FCSTD DOCUMENT  (FreeCAD 1.0R39109 (Git))
Label: handle-5mk3
License: All rights reserved
LicenseURL: https://en.wikipedia.org/wiki/All_rights_reserved
objects: Sketcher::SketchObject×44, PartDesign::Plane×17, PartDesign::Fillet×7, PartDesign::AdditivePipe×4, PartDesign::Pad×2, PartDesign::Body×2, Part::Feature×2, Mesh::Feature×1, PartDesign::SubtractiveLoft×1, PartDesign::Hole×1, Part::Refine×1, PartDesign::Pocket×1
note: 158 computed .brp shape members not serialized (recipe doc carries the construction recipe); baked Part::Feature solids carry a one-line shape summary decoded from their .brp

FEATURE [Sketcher::SketchObject] Sketch  label="draft"
  ArcFitTolerance = 1e-06
  FullyConstrained = false
  MakeInternals = false
  sketch-geometry (31):
    g0: LineSegment StartX=0 StartY=16.8405 StartZ=0 EndX=0 EndY=0 EndZ=0
    g1: ArcOfCircle CenterX=24.2442 CenterY=17 CenterZ=0 NormalX=0 NormalY=0 NormalZ=1 AngleXU=0 Radius=17 StartAngle=4.71239 EndAngle=6.01234
    g2: ArcOfCircle CenterX=12.089 CenterY=21.8405 CenterZ=0 NormalX=0 NormalY=0 NormalZ=1 AngleXU=0 Radius=5 StartAngle=4.71239 EndAngle=6.02249
    g3: ArcOfCircle CenterX=0 CenterY=8.42024 CenterZ=0 NormalX=0 NormalY=0 NormalZ=1 AngleXU=0 Radius=8.42024 StartAngle=1.5708 EndAngle=4.71239
    g4: LineSegment StartX=12.089 StartY=16.8405 StartZ=0 EndX=12.089 EndY=0 EndZ=0
    g5: LineSegment StartX=15.135 StartY=17.8754 StartZ=0 EndX=34.532 EndY=3.46632 EndZ=0
    g6: LineSegment StartX=12.089 StartY=16.8405 StartZ=0 EndX=24.2442 EndY=-0.00123973 EndZ=0
    g7: LineSegment StartX=16.92 StartY=20.5517 StartZ=0 EndX=40.6245 EndY=12.4517 EndZ=0
    g8: LineSegment StartX=12.089 StartY=16.8405 StartZ=0 EndX=17.9725 EndY=-3.6e-15 EndZ=0
    g9: LineSegment StartX=8.25203 StartY=67.8671 StartZ=0 EndX=4.47332 EndY=84.6059 EndZ=0
    g10: ArcOfCircle CenterX=6.36268 CenterY=76.2365 CenterZ=0 NormalX=0 NormalY=0 NormalZ=1 AngleXU=0 Radius=8.58001 StartAngle=1.79282 EndAngle=4.93441
    g11: LineSegment StartX=4.3823 StartY=126.388 StartZ=0 EndX=26.3634 EndY=138.297 EndZ=0
    g12: LineSegment StartX=0 StartY=0 StartZ=0 EndX=24.2442 EndY=0 EndZ=0
    g13: LineSegment StartX=12.089 StartY=16.8405 StartZ=0 EndX=0 EndY=16.8405 EndZ=0
    g14: ArcOfCircle CenterX=-122.373 CenterY=57.711 CenterZ=0 NormalX=0 NormalY=0 NormalZ=1 AngleXU=0 Radius=169.165 StartAngle=6.01234 EndAngle=6.77971
    g15: LineSegment StartX=34.0166 StartY=141.401 StartZ=0 EndX=34.0166 EndY=126.047 EndZ=0
    g16: LineSegment StartX=34.0166 StartY=141.401 StartZ=0 EndX=31.941 EndY=152.351 EndZ=0
    g17: LineSegment StartX=22.7796 StartY=155.606 StartZ=0 EndX=28.011 EndY=155.606 EndZ=0
    g18: LineSegment StartX=18.3769 StartY=88.901 StartZ=0 EndX=4.47332 EndY=84.6059 EndZ=0
    g19: LineSegment StartX=21.1969 StartY=70.7893 StartZ=0 EndX=8.25203 EndY=67.8671 EndZ=0
    g20: LineSegment StartX=18.7796 StartY=146.991 StartZ=0 EndX=18.7796 EndY=151.606 EndZ=0
    g21: LineSegment StartX=15.6305 StartY=135.869 StartZ=0 EndX=18.5135 EndY=145.224 EndZ=0
    g22: ArcOfCircle CenterX=12.7796 CenterY=146.991 CenterZ=0 NormalX=0 NormalY=0 NormalZ=1 AngleXU=0 Radius=6 StartAngle=5.98426 EndAngle=6.28319
    g23: ArcOfCircle CenterX=5.11835 CenterY=139.108 CenterZ=0 NormalX=0 NormalY=0 NormalZ=1 AngleXU=0 Radius=11 StartAngle=5.12409 EndAngle=5.98426
    g24: ArcOfCircle CenterX=27.9086 CenterY=86.9159 CenterZ=0 NormalX=0 NormalY=0 NormalZ=1 AngleXU=0 Radius=45.9511 StartAngle=1.9825 EndAngle=2.10829
    g25: ArcOfCircle CenterX=22.7796 CenterY=151.606 CenterZ=0 NormalX=0 NormalY=0 NormalZ=1 AngleXU=0 Radius=4 StartAngle=1.5708 EndAngle=3.14159
    g26: ArcOfCircle CenterX=28.011 CenterY=151.606 CenterZ=0 NormalX=0 NormalY=0 NormalZ=1 AngleXU=0 Radius=4 StartAngle=0.187333 EndAngle=1.5708
    g27: ArcOfCircle CenterX=54.0166 CenterY=126.047 CenterZ=0 NormalX=0 NormalY=0 NormalZ=1 AngleXU=0 Radius=20 StartAngle=3.14159 EndAngle=3.5112
    g28: ArcOfCircle CenterX=-122.373 CenterY=57.711 CenterZ=0 NormalX=0 NormalY=0 NormalZ=1 AngleXU=0 Radius=144.165 StartAngle=6.02249 EndAngle=6.37403
    g29: ArcOfCircle CenterX=-122.373 CenterY=57.711 CenterZ=0 NormalX=0 NormalY=0 NormalZ=1 AngleXU=0 Radius=144.165 StartAngle=0.218074 EndAngle=0.496528
    g30: ArcOfCircle CenterX=-122.373 CenterY=57.711 CenterZ=0 NormalX=0 NormalY=0 NormalZ=1 AngleXU=0 Radius=156.665 StartAngle=6.01234 EndAngle=6.77971
  constraints (1):
    c: Distance(g6,g6) = 20.77
FEATURE [Sketcher::SketchObject] Sketch001  label="main"
  ArcFitTolerance = 1e-06
  AttachmentSupport = -> [XY_Plane]
  FullyConstrained = false
  MakeInternals = false
  MapMode = 5
  sketch-geometry (33):
    g0: LineSegment StartX=0 StartY=0 StartZ=0 EndX=3e-16 EndY=17 EndZ=0
    g1: LineSegment StartX=3e-16 StartY=17 StartZ=0 EndX=11.9553 EndY=17 EndZ=0
    g2: ArcOfCircle CenterX=0.098169 CenterY=8.5 CenterZ=0 NormalX=0 NormalY=0 NormalZ=1 AngleXU=0 Radius=8.50057 StartAngle=1.58235 EndAngle=4.70084
    g3: LineSegment StartX=4.3731 StartY=126.451 StartZ=0 EndX=26.3546 EndY=138.359 EndZ=0
    g4: ArcOfCircle CenterX=-121.158 CenterY=57.9598 CenterZ=0 NormalX=0 NormalY=0 NormalZ=1 AngleXU=0 Radius=168 StartAngle=6.01838 EndAngle=6.78221
    g5: ArcOfCircle CenterX=-121.158 CenterY=57.9598 CenterZ=0 NormalX=0 NormalY=0 NormalZ=1 AngleXU=0 Radius=143 StartAngle=6.01836 EndAngle=6.78265
    g6: ArcOfCircle CenterX=11.9915 CenterY=22.1177 CenterZ=0 NormalX=0 NormalY=0 NormalZ=1 AngleXU=0 Radius=5.11783 StartAngle=4.70532 EndAngle=5.96793
    g7: LineSegment StartX=40.9861 StartY=13.99 StartZ=0 EndX=16.8571 EndY=20.5309 EndZ=0
    g8: ArcOfCircle CenterX=23.8596 CenterY=17.4727 CenterZ=0 NormalX=0 NormalY=0 NormalZ=1 AngleXU=0 Radius=17.4771 StartAngle=4.73473 EndAngle=6.08257
    g9: LineSegment StartX=33.9499 StartY=141.42 StartZ=0 EndX=32 EndY=152 EndZ=0
    g10: LineSegment StartX=19 StartY=152 StartZ=0 EndX=18.6911 EndY=146 EndZ=0
    g11: LineSegment StartX=22 StartY=155.6 StartZ=0 EndX=29 EndY=155.6 EndZ=0
    g12: ArcOfCircle CenterX=28.2135 CenterY=151.895 CenterZ=0 NormalX=0 NormalY=0 NormalZ=1 AngleXU=0 Radius=3.78792 StartAngle=0.027823 EndAngle=1.36165
    g13: ArcOfCircle CenterX=22.5443 CenterY=152.096 CenterZ=0 NormalX=0 NormalY=0 NormalZ=1 AngleXU=0 Radius=3.5456 StartAngle=1.72492 EndAngle=3.16879
    g14: LineSegment StartX=4.41682 StartY=84.6096 StartZ=0 EndX=8.23235 EndY=68.0434 EndZ=0
    g15: ArcOfCircle CenterX=6.32458 CenterY=76.3265 CenterZ=0 NormalX=0 NormalY=0 NormalZ=1 AngleXU=0 Radius=8.5 StartAngle=1.79717 EndAngle=4.93946
    g16: LineSegment StartX=4.42825 StartY=84.5878 StartZ=0 EndX=18.4319 EndY=88.947 EndZ=0
    g17: LineSegment StartX=8.23235 StartY=68.0434 StartZ=0 EndX=21.1452 EndY=72.063 EndZ=0
    g18: LineSegment StartX=32.5262 StartY=20 StartZ=0 EndX=28.9216 EndY=17.2604 EndZ=0
    g19: LineSegment StartX=11.9553 StartY=17 StartZ=0 EndX=24.25 EndY=5.33e-14 EndZ=0
    g20: LineSegment StartX=14.9929 StartY=17.9724 StartZ=0 EndX=35.0562 EndY=4.05322 EndZ=0
    g21: LineSegment StartX=16.2172 StartY=19.2306 StartZ=0 EndX=39.0494 EndY=8.82884 EndZ=0
    g22: LineSegment StartX=13.6942 StartY=17.2914 StartZ=0 EndX=30.2927 EndY=1.22269 EndZ=0
    g23: LineSegment StartX=10.6374 StartY=17 StartZ=0 EndX=17.3604 EndY=0 EndZ=0
    g24: LineSegment StartX=9.44468 StartY=17 StartZ=0 EndX=12.125 EndY=0 EndZ=0
    g25: LineSegment StartX=8.01497 StartY=17 StartZ=0 EndX=8.01497 EndY=0 EndZ=0
    g26: LineSegment StartX=5.97763 StartY=17 StartZ=0 EndX=5.97763 EndY=0 EndZ=0
    g27: LineSegment StartX=20.8595 StartY=74.6968 StartZ=0 EndX=45.6917 EndY=77.5875 EndZ=0
    g28: LineSegment StartX=0 StartY=0 StartZ=0 EndX=8.01497 EndY=0 EndZ=0
    g29: LineSegment StartX=8.01497 StartY=0 StartZ=0 EndX=24.25 EndY=0 EndZ=0
    g30: LineSegment StartX=15.3638 StartY=132.405 StartZ=0 EndX=18.6911 EndY=146 EndZ=0
    g31: LineSegment StartX=33.9499 StartY=141.42 StartZ=0 EndX=35.5663 EndY=109.757 EndZ=0
    g32: LineSegment StartX=15.3638 StartY=132.405 StartZ=0 EndX=35.5663 EndY=109.757 EndZ=0
  constraints (60):
    c: PointOnObject(g8,g-1)
    c: Distance(g0) = 17
    c: PointOnObject(g0,g-2)
    c: DistanceX(g-1,g8) = 24.25
    c: Coincident(g1,g0)
    c: Horizontal(g1)
    c: Coincident(g2,g0)
    c: Distance(g3) = 25
    c: Coincident(g4,g3)
    c: Radius(g4) = 168
    c: Coincident(g5,g4)
    c: Coincident(g5,g3)
    c: Coincident(g6,g1)
    c: Coincident(g6,g5)
    c: Coincident(g7,g4)
    c: Coincident(g7,g5)
    c: DistanceY(g-1,g4) = 13.99
    c: Coincident(g8,g4)
    c: Horizontal(g11)
    c: Coincident(g12,g11)
    c: Coincident(g12,g9)
    c: Coincident(g13,g11)
    c: Coincident(g13,g10)
    c: Distance(g14) = 17
    c: Symmetric(g14,g14,g15)
    c: Coincident(g15,g14)
    c: Coincident(g17,g14)
    c: PointOnObject(g17,g5)
    c: Parallel(g17,g16)
    c: Symmetric(g7,g7,g18)
    c: Coincident(g19,g1)
    c: PointOnObject(g20,g6)
    c: PointOnObject(g20,g8)
    c: PointOnObject(g21,g6)
    c: PointOnObject(g21,g8)
    c: PointOnObject(g22,g6)
    c: PointOnObject(g22,g8)
    c: PointOnObject(g23,g1)
    c: PointOnObject(g24,g1)
    c: Symmetric(g-1,g8,g24)
    c: PointOnObject(g25,g1)
    c: Vertical(g25)
    c: Symmetric(g1,g1,g26)
    c: Vertical(g26)
    c: PointOnObject(g27,g5)
    c: PointOnObject(g27,g4)
    c: Distance(g19,g19) = 20.98
    c: Distance(g21,g21) = 25.09
    c: Distance(g24,g24) = 17.21
    c: Coincident(g28,g0)
    c: Coincident(g28,g25)
    c: Horizontal(g28)
    c: Coincident(g29,g25)
    c: Coincident(g29,g8)
    c: Horizontal(g29)
    c: Symmetric(g3,g3,g30)
    c: Coincident(g30,g10)
    c: Coincident(g31,g9)
    c: Coincident(g32,g30)
    c: Coincident(g32,g31)
FEATURE [PartDesign::Plane] DatumPlane001
  AttachmentOffset = pos=(0,0,0) rot=(0,1,0;1.5708rad)
  AttachmentSupport = -> [Sketch001]
  Length = 78.1067
  MapMode = 7
  Placement = pos=(40.9861,13.99,0) rot=(0.093727,0.703994,0.703994;2.95468rad)
  ResizeMode = 0
  Width = 61.5385
FEATURE [PartDesign::Plane] DatumPlane002
  AttachmentOffset = pos=(0,0,0) rot=(0,1,0;1.5708rad)
  AttachmentSupport = -> [Sketch001]
  Length = 60
  MapMode = 7
  Placement = pos=(0,0,0) rot=(0.57735,0.57735,0.57735;2.0944rad)
  ResizeMode = 0
  Width = 60
FEATURE [PartDesign::Plane] DatumPlane
  AttachmentOffset = pos=(0,0,0) rot=(0,1,0;1.5708rad)
  AttachmentSupport = -> [Sketch001]
  Length = 111.967
  MapMode = 7
  Placement = pos=(4.3731,126.451,0) rot=(0.941347,0.238607,0.238607;1.6312rad)
  ResizeMode = 0
  Width = 63.9978
FEATURE [Sketcher::SketchObject] Sketch002
  ArcFitTolerance = 1e-06
  AttachmentSupport = -> [DatumPlane]
  FullyConstrained = false
  MakeInternals = false
  MapMode = 5
  Placement = pos=(4.3731,126.451,0) rot=(0.941347,0.238607,0.238607;1.6312rad)
  sketch-geometry (5):
    g0: Ellipse CenterX=12.5 CenterY=0 CenterZ=0 NormalX=0 NormalY=0 NormalZ=1 MajorRadius=18 MinorRadius=12.5 AngleXU=1.5708
    g1: LineSegment [constr] StartX=12.5 StartY=18 StartZ=0 EndX=12.5 EndY=-18 EndZ=0
    g2: LineSegment [constr] StartX=0 StartY=0 StartZ=0 EndX=25 EndY=0 EndZ=0
    g3: GeomPoint [constr] X=12.5 Y=12.9518 Z=0
    g4: GeomPoint [constr] X=12.5 Y=-12.9518 Z=0
  constraints (2):
    c: InternalAlignment(g1-g4 -> g0) x4
    c: PointOnObject(g-1,g0)
FEATURE [Sketcher::SketchObject] Sketch004  label="end"
  ArcFitTolerance = 1e-06
  AttachmentOffset = pos=(0,0,-5) rot=(0,0,1;0rad)
  AttachmentSupport = -> [DatumPlane002]
  FullyConstrained = false
  MakeInternals = false
  MapMode = 5
  Placement = pos=(-5,0,0) rot=(0.57735,0.57735,0.57735;2.0944rad)
  sketch-geometry (5):
    g0: Ellipse CenterX=8.5 CenterY=0 CenterZ=0 NormalX=0 NormalY=0 NormalZ=1 MajorRadius=18 MinorRadius=8.5 AngleXU=1.5708
    g1: LineSegment [constr] StartX=8.5 StartY=18 StartZ=0 EndX=8.5 EndY=-18 EndZ=0
    g2: LineSegment [constr] StartX=0 StartY=0 StartZ=0 EndX=17 EndY=0 EndZ=0
    g3: GeomPoint [constr] X=8.5 Y=15.8666 Z=0
    g4: GeomPoint [constr] X=8.5 Y=-15.8666 Z=0
  constraints (2):
    c: InternalAlignment(g1-g4 -> g0) x4
    c: PointOnObject(g-1,g0)
FEATURE [PartDesign::AdditivePipe] AdditivePipe
  AuxilleryCurvelinear = true
  AuxillerySpineTangent = false
  Binormal = (0,0,0)
  Mode = 0
  Placement = pos=(4.3731,126.451,0) rot=(0.941347,0.238607,0.238607;1.6312rad)
  Profile = -> Sketch002
  Refine = true
  Spine = -> Sketch001 [Edge8]
  SpineTangent = false
  Suppressed = false
  Transformation = 0
  Transition = 0
FEATURE [PartDesign::Plane] DatumPlane004
  AttachmentOffset = pos=(0,0,0) rot=(0,1,0;1.5708rad)
  AttachmentSupport = -> [Sketch001]
  Length = 81.3794
  MapMode = 7
  Placement = pos=(14.9929,17.9724,0) rot=(-0.91446,0.28615,0.28615;4.62309rad)
  ResizeMode = 0
  Width = 61.7968
FEATURE [Sketcher::SketchObject] Sketch006
  ArcFitTolerance = 1e-06
  AttachmentSupport = -> [DatumPlane004]
  FullyConstrained = false
  MakeInternals = false
  MapMode = 5
  Placement = pos=(14.9929,17.9724,0) rot=(0.91446,-0.28615,-0.28615;1.6601rad)
  sketch-geometry (5):
    g0: Ellipse CenterX=12.205 CenterY=0 CenterZ=0 NormalX=0 NormalY=0 NormalZ=1 MajorRadius=18 MinorRadius=12.205 AngleXU=1.5708
    g1: LineSegment [constr] StartX=12.205 StartY=18 StartZ=0 EndX=12.205 EndY=-18 EndZ=0
    g2: LineSegment [constr] StartX=0 StartY=0 StartZ=0 EndX=24.41 EndY=0 EndZ=0
    g3: GeomPoint [constr] X=12.205 Y=13.2302 Z=0
    g4: GeomPoint [constr] X=12.205 Y=-13.2302 Z=0
  constraints (2):
    c: InternalAlignment(g1-g4 -> g0) x4
    c: PointOnObject(g-1,g0)
FEATURE [PartDesign::Plane] DatumPlane005
  AttachmentOffset = pos=(0,0,0) rot=(0,1,0;1.5708rad)
  AttachmentSupport = -> [Sketch001]
  Length = 81.6324
  MapMode = 7
  Placement = pos=(11.9553,17,0) rot=(-0.810565,0.414116,0.414116;4.50389rad)
  ResizeMode = 0
  Width = 61.8166
FEATURE [Sketcher::SketchObject] Sketch007
  ArcFitTolerance = 1e-06
  AttachmentSupport = -> [DatumPlane005]
  FullyConstrained = false
  MakeInternals = false
  MapMode = 5
  Placement = pos=(11.9553,17,0) rot=(0.810565,-0.414116,-0.414116;1.77929rad)
  sketch-geometry (5):
    g0: Ellipse CenterX=10.49 CenterY=0 CenterZ=0 NormalX=0 NormalY=0 NormalZ=1 MajorRadius=18 MinorRadius=10.49 AngleXU=1.5708
    g1: LineSegment [constr] StartX=10.49 StartY=18 StartZ=0 EndX=10.49 EndY=-18 EndZ=0
    g2: LineSegment [constr] StartX=0 StartY=0 StartZ=0 EndX=20.98 EndY=0 EndZ=0
    g3: GeomPoint [constr] X=10.49 Y=14.6274 Z=0
    g4: GeomPoint [constr] X=10.49 Y=-14.6274 Z=0
  constraints (2):
    c: InternalAlignment(g1-g4 -> g0) x4
    c: PointOnObject(g-1,g0)
FEATURE [PartDesign::Plane] DatumPlane006
  AttachmentOffset = pos=(0,0,0) rot=(0,1,0;1.5708rad)
  AttachmentSupport = -> [Sketch001]
  Length = 77.7387
  MapMode = 7
  Placement = pos=(16.2172,19.2306,0) rot=(-0.955975,0.207499,0.207499;4.66738rad)
  ResizeMode = 0
  Width = 61.5091
FEATURE [Sketcher::SketchObject] Sketch008
  ArcFitTolerance = 1e-06
  AttachmentSupport = -> [DatumPlane006]
  FullyConstrained = false
  MakeInternals = false
  MapMode = 5
  Placement = pos=(16.2172,19.2306,0) rot=(0.955975,-0.207499,-0.207499;1.6158rad)
  sketch-geometry (5):
    g0: Ellipse CenterX=12.545 CenterY=0 CenterZ=0 NormalX=0 NormalY=0 NormalZ=1 MajorRadius=18 MinorRadius=12.545 AngleXU=1.5708
    g1: LineSegment [constr] StartX=12.545 StartY=18 StartZ=0 EndX=12.545 EndY=-18 EndZ=0
    g2: LineSegment [constr] StartX=0 StartY=0 StartZ=0 EndX=25.09 EndY=0 EndZ=0
    g3: GeomPoint [constr] X=12.545 Y=12.9083 Z=0
    g4: GeomPoint [constr] X=12.545 Y=-12.9083 Z=0
  constraints (2):
    c: InternalAlignment(g1-g4 -> g0) x4
    c: PointOnObject(g-1,g0)
FEATURE [PartDesign::Plane] DatumPlane007
  AttachmentOffset = pos=(0,0,0) rot=(0,1,0;1.5708rad)
  AttachmentSupport = -> [Sketch001]
  Length = 81.6324
  MapMode = 7
  Placement = pos=(11.9553,17,0) rot=(-0.810565,0.414116,0.414116;4.50389rad)
  ResizeMode = 0
  Width = 61.8166
FEATURE [Sketcher::SketchObject] Sketch009  label="start"
  ArcFitTolerance = 1e-06
  AttachmentSupport = -> [DatumPlane007]
  FullyConstrained = false
  MakeInternals = false
  MapMode = 5
  Placement = pos=(11.9553,17,0) rot=(0.810565,-0.414116,-0.414116;1.77929rad)
  sketch-geometry (5):
    g0: Ellipse CenterX=10.49 CenterY=0 CenterZ=0 NormalX=0 NormalY=0 NormalZ=1 MajorRadius=18 MinorRadius=10.49 AngleXU=1.5708
    g1: LineSegment [constr] StartX=10.49 StartY=18 StartZ=0 EndX=10.49 EndY=-18 EndZ=0
    g2: LineSegment [constr] StartX=0 StartY=0 StartZ=0 EndX=20.98 EndY=0 EndZ=0
    g3: GeomPoint [constr] X=10.49 Y=14.6274 Z=0
    g4: GeomPoint [constr] X=10.49 Y=-14.6274 Z=0
  constraints (2):
    c: InternalAlignment(g1-g4 -> g0) x4
    c: PointOnObject(g-1,g0)
FEATURE [PartDesign::Plane] DatumPlane008
  AttachmentOffset = pos=(0,0,0) rot=(0,1,0;1.5708rad)
  AttachmentSupport = -> [Sketch001]
  Length = 67.8706
  MapMode = 7
  Placement = pos=(9.44468,17,0) rot=(-0.63745,0.54482,0.54482;4.2766rad)
  ResizeMode = 0
  Width = 60.6936
FEATURE [Sketcher::SketchObject] Sketch010
  ArcFitTolerance = 1e-06
  AttachmentOffset = pos=(0,0,2) rot=(0,0,1;0rad)
  AttachmentSupport = -> [DatumPlane008]
  FullyConstrained = false
  MakeInternals = false
  MapMode = 5
  Placement = pos=(7.46909,16.6885,2e-16) rot=(0.63745,-0.54482,-0.54482;2.00659rad)
  sketch-geometry (5):
    g0: Ellipse CenterX=8.605 CenterY=0 CenterZ=0 NormalX=0 NormalY=0 NormalZ=1 MajorRadius=18 MinorRadius=8.605 AngleXU=1.5708
    g1: LineSegment [constr] StartX=8.605 StartY=18 StartZ=0 EndX=8.605 EndY=-18 EndZ=0
    g2: LineSegment [constr] StartX=0 StartY=0 StartZ=0 EndX=17.21 EndY=0 EndZ=0
    g3: GeomPoint [constr] X=8.605 Y=15.8099 Z=0
    g4: GeomPoint [constr] X=8.605 Y=-15.8099 Z=0
  constraints (2):
    c: InternalAlignment(g1-g4 -> g0) x4
    c: PointOnObject(g-1,g0)
FEATURE [PartDesign::Plane] DatumPlane009
  AttachmentOffset = pos=(0,0,0) rot=(0,1,0;1.5708rad)
  AttachmentSupport = -> [Sketch001]
  Length = 60
  MapMode = 7
  Placement = pos=(8.01497,17,0) rot=(-0.57735,0.57735,0.57735;4.18879rad)
  ResizeMode = 0
  Width = 60
FEATURE [Sketcher::SketchObject] Sketch011
  ArcFitTolerance = 1e-06
  AttachmentOffset = pos=(0,0,5) rot=(0,0,1;0rad)
  AttachmentSupport = -> [DatumPlane009]
  FullyConstrained = false
  MakeInternals = false
  MapMode = 5
  Placement = pos=(3.01497,17,0) rot=(0.57735,-0.57735,-0.57735;2.0944rad)
  sketch-geometry (5):
    g0: Ellipse CenterX=8.5 CenterY=0 CenterZ=0 NormalX=0 NormalY=0 NormalZ=1 MajorRadius=18 MinorRadius=8.5 AngleXU=1.5708
    g1: LineSegment [constr] StartX=8.5 StartY=18 StartZ=0 EndX=8.5 EndY=-18 EndZ=0
    g2: LineSegment [constr] StartX=0 StartY=0 StartZ=0 EndX=17 EndY=0 EndZ=0
    g3: GeomPoint [constr] X=8.5 Y=15.8666 Z=0
    g4: GeomPoint [constr] X=8.5 Y=-15.8666 Z=0
  constraints (2):
    c: InternalAlignment(g1-g4 -> g0) x4
    c: PointOnObject(g-1,g0)
FEATURE [Sketcher::SketchObject] Sketch012
  ArcFitTolerance = 1e-06
  AttachmentSupport = -> [XY_Plane]
  FullyConstrained = false
  MakeInternals = false
  MapMode = 5
  sketch-geometry (2):
    g0: ArcOfCircle CenterX=0 CenterY=8.5 CenterZ=0 NormalX=0 NormalY=0 NormalZ=1 AngleXU=0 Radius=8.5 StartAngle=1.5708 EndAngle=4.71239
    g1: LineSegment StartX=-1.6e-15 StartY=17 StartZ=0 EndX=-1.6e-15 EndY=0 EndZ=0
  constraints (4):
    c: Coincident(g0,g-1)
    c: Coincident(g1,g0)
    c: Coincident(g1,g0)
    c: Vertical(g1)
FEATURE [Sketcher::SketchObject] Sketch013  label="hole"
  ArcFitTolerance = 1e-06
  AttachmentOffset = pos=(0,0,19) rot=(0,0,1;0rad)
  AttachmentSupport = -> [XY_Plane]
  FullyConstrained = false
  MakeInternals = false
  MapMode = 5
  Placement = pos=(0,0,19) rot=(0,0,1;0rad)
  sketch-geometry (2):
    g0: Circle CenterX=29.902 CenterY=19.7627 CenterZ=0 NormalX=0 NormalY=0 NormalZ=1 AngleXU=0 Radius=0.75
    g1: Circle CenterX=24.3839 CenterY=114.1 CenterZ=0 NormalX=0 NormalY=0 NormalZ=1 AngleXU=0 Radius=0.75
  constraints (2):
    c: Diameter(g0) = 1.5
    c: Diameter(g1) = 1.5
FEATURE [Sketcher::SketchObject] Sketch014
  ArcFitTolerance = 1e-06
  AttachmentSupport = -> [XY_Plane]
  FullyConstrained = true
  MakeInternals = false
  MapMode = 5
FEATURE [Sketcher::SketchObject] Sketch015
  ArcFitTolerance = 1e-06
  AttachmentSupport = -> [XY_Plane]
  FullyConstrained = false
  MakeInternals = false
  MapMode = 5
  sketch-geometry (8):
    g0: LineSegment StartX=23.8504 StartY=155.6 StartZ=0 EndX=28.2953 EndY=155.6 EndZ=0
    g1: LineSegment StartX=18.9469 StartY=150.935 StartZ=0 EndX=18.7 EndY=145.978 EndZ=0
    g2: LineSegment StartX=18.7 StartY=145.978 StartZ=0 EndX=15.4 EndY=132.3 EndZ=0
    g3: LineSegment StartX=15.4 StartY=132.3 StartZ=0 EndX=34 EndY=110 EndZ=0
    g4: LineSegment StartX=34 StartY=141 StartZ=0 EndX=34 EndY=110 EndZ=0
    g5: LineSegment StartX=34 StartY=141 StartZ=0 EndX=31.8911 EndY=152.599 EndZ=0
    g6: ArcOfCircle CenterX=28.2953 CenterY=151.945 CenterZ=0 NormalX=0 NormalY=0 NormalZ=1 AngleXU=0 Radius=3.65468 StartAngle=0.179853 EndAngle=1.5708
    g7: ArcOfCircle CenterX=23.8504 CenterY=150.69 CenterZ=0 NormalX=0 NormalY=0 NormalZ=1 AngleXU=0 Radius=4.90952 StartAngle=1.5708 EndAngle=3.09181
  constraints (10):
    c: Horizontal(g0)
    c: Coincident(g2,g1)
    c: Coincident(g3,g2)
    c: Coincident(g4,g3)
    c: Vertical(g4)
    c: Coincident(g5,g4)
    c: Tangent(g0,g6) = 1.5708
    c: Tangent(g5,g6) = -1.5708
    c: Tangent(g0,g7) = 1.5708
    c: Tangent(g1,g7) = -1.5708
FEATURE [Sketcher::SketchObject] Sketch016
  ArcFitTolerance = 1e-06
  AttachmentSupport = -> [XY_Plane]
  FullyConstrained = false
  MakeInternals = false
  MapMode = 5
  sketch-geometry (25):
    g0-g6: Circle [constr] x7 (B-spline internal-alignment scaffolding for g7; pole/knot coordinates omitted)
    g7: BSplineCurve PolesCount=7 KnotsCount=5 Degree=3 IsPeriodic=0
    g8-g12: GeomPoint [constr] x5 (B-spline internal-alignment scaffolding for g7; pole/knot coordinates omitted)
    g13-g17: Circle [constr] x5 (B-spline internal-alignment scaffolding for g18; pole/knot coordinates omitted)
    g18: BSplineCurve PolesCount=5 KnotsCount=3 Degree=3 IsPeriodic=0
    g19: GeomPoint [constr] X=-13.6801 Y=65.1223 Z=0
    g20: GeomPoint [constr] X=2.04903 Y=69.1377 Z=0
    g21: GeomPoint [constr] X=32.8092 Y=77.3228 Z=0
    g22: LineSegment StartX=12.6036 StartY=113.182 StartZ=0 EndX=25 EndY=113.182 EndZ=0
    g23: LineSegment StartX=32.8092 StartY=77.3228 StartZ=0 EndX=25 EndY=113.182 EndZ=0
    g24: ArcOfCircle CenterX=27.8804 CenterY=86.9633 CenterZ=0 NormalX=0 NormalY=0 NormalZ=1 AngleXU=0 Radius=46.95 StartAngle=3.20085 EndAngle=3.62545
  constraints (20):
    c: Weight(g0) = 1
    c: Equal(g0, g1-g6) x6
    c: InternalAlignment(g0-g6 -> g7) x7
    c: InternalAlignment(g8-g12 -> g7) x5
    c: Weight(g13) = 1
    c: Equal(g13, g14-g17) x4
    c: InternalAlignment(g13-g17 -> g18) x5
    c: InternalAlignment(g19,g18)
    c: InternalAlignment(g20,g18)
    c: InternalAlignment(g21,g18)
    c: PointOnObject(g15,g-2)
    c: Coincident(g22,g7)
    c: Horizontal(g22)
    c: Coincident(g23,g18)
    c: Coincident(g23,g22)
    c: Coincident(g24,g7)
    c: Coincident(g24,g18)
    c: Radius(g24) = 46.95
    c: DistanceX(g18) = -13.6801
    c: DistanceY(g18) = 65.1223
FEATURE [Mesh::Feature] right_handle
  Placement = pos=(-103,67,0) rot=(0,0,1;0rad)
FEATURE [Sketcher::SketchObject] Sketch017
  ArcFitTolerance = 1e-06
  AttachmentSupport = -> [AdditivePipe]
  FullyConstrained = true
  MakeInternals = false
  MapMode = 5
  Placement = pos=(4.3731,126.451,0) rot=(-0.941347,-0.238607,0.238607;1.6312rad)
FEATURE [Sketcher::SketchObject] Sketch018
  ArcFitTolerance = 1e-06
  AttachmentSupport = -> [DatumPlane001]
  FullyConstrained = false
  MakeInternals = false
  MapMode = 5
  Placement = pos=(40.9861,13.99,0) rot=(0.093727,0.703994,0.703994;2.95468rad)
  sketch-geometry (5):
    g0: Ellipse CenterX=12.5017 CenterY=0 CenterZ=0 NormalX=0 NormalY=0 NormalZ=1 MajorRadius=18 MinorRadius=12.5017 AngleXU=1.5708
    g1: LineSegment [constr] StartX=12.5017 StartY=18 StartZ=0 EndX=12.5017 EndY=-18 EndZ=0
    g2: LineSegment [constr] StartX=0 StartY=0 StartZ=0 EndX=25.0033 EndY=0 EndZ=0
    g3: GeomPoint [constr] X=12.5017 Y=12.9502 Z=0
    g4: GeomPoint [constr] X=12.5017 Y=-12.9502 Z=0
  constraints (3):
    c: InternalAlignment(g1-g4 -> g0) x4
    c: Distance(g0,g1) = 18
    c: PointOnObject(g0,g-1)
FEATURE [PartDesign::AdditivePipe] AdditivePipe001
  AuxilleryCurvelinear = true
  AuxillerySpineTangent = false
  BaseFeature = -> AdditivePipe
  Binormal = (0,0,0)
  Mode = 0
  Placement = pos=(4.3731,126.451,0) rot=(0.941347,0.238607,0.238607;1.6312rad)
  Profile = -> Sketch018
  Refine = true
  Sections = -> [Sketch008,Sketch006,Sketch007]
  Spine = -> Sketch001 [Edge7]
  SpineTangent = false
  Suppressed = false
  Transformation = 1
  Transition = 0
FEATURE [PartDesign::AdditivePipe] AdditivePipe002
  AuxilleryCurvelinear = true
  AuxillerySpineTangent = false
  BaseFeature = -> AdditivePipe001
  Binormal = (0,0,0)
  Mode = 0
  Placement = pos=(4.3731,126.451,0) rot=(0.941347,0.238607,0.238607;1.6312rad)
  Profile = -> Sketch009
  Refine = true
  Sections = -> [Sketch010,Sketch011,Sketch004]
  Spine = -> Sketch001 [Edge6]
  SpineTangent = false
  Suppressed = false
  Transformation = 1
  Transition = 0
FEATURE [PartDesign::Pad] Pad
  BaseFeature = -> AdditivePipe002
  Direction = (0,0,1)
  Length = 25
  Length2 = 10
  Midplane = true
  Placement = pos=(4.3731,126.451,0) rot=(0.941347,0.238607,0.238607;1.6312rad)
  Profile = -> Sketch016
  ReferenceAxis = -> Sketch016 [N_Axis]
  Refine = true
  Suppressed = false
  Type = 0
FEATURE [PartDesign::Fillet] Fillet
  Base = -> Pad [Edge27]
  BaseFeature = -> Pad
  Placement = pos=(4.3731,126.451,0) rot=(0.941347,0.238607,0.238607;1.6312rad)
  Radius = 5
  Refine = true
  SupportTransform = false
  Suppressed = false
  UseAllEdges = false
FEATURE [PartDesign::Fillet] Fillet001
  Base = -> Fillet [Edge26]
  BaseFeature = -> Fillet
  Placement = pos=(4.3731,126.451,0) rot=(0.941347,0.238607,0.238607;1.6312rad)
  Radius = 10
  Refine = true
  SupportTransform = false
  Suppressed = false
  UseAllEdges = false
FEATURE [PartDesign::Fillet] Fillet002
  Base = -> Fillet001 [Edge25]
  BaseFeature = -> Fillet001
  Placement = pos=(4.3731,126.451,0) rot=(0.941347,0.238607,0.238607;1.6312rad)
  Radius = 10
  Refine = true
  SupportTransform = false
  Suppressed = false
  UseAllEdges = false
FEATURE [PartDesign::Fillet] Fillet003
  Base = -> Fillet002 [Edge23]
  BaseFeature = -> Fillet002
  Placement = pos=(4.3731,126.451,0) rot=(0.941347,0.238607,0.238607;1.6312rad)
  Radius = 5
  Refine = true
  SupportTransform = false
  Suppressed = false
  UseAllEdges = false
FEATURE [PartDesign::Fillet] Fillet004
  Base = -> Fillet003 [Edge4]
  BaseFeature = -> Fillet003
  Placement = pos=(4.3731,126.451,0) rot=(0.941347,0.238607,0.238607;1.6312rad)
  Radius = 4
  Refine = true
  SupportTransform = false
  Suppressed = false
  UseAllEdges = false
FEATURE [Sketcher::SketchObject] Sketch020
  ArcFitTolerance = 1e-06
  AttachmentSupport = -> [XY_Plane]
  ExternalGeometry = -> [Sketch004]
  FullyConstrained = false
  MakeInternals = false
  MapMode = 5
  sketch-geometry (8):
    g0: LineSegment StartX=-5 StartY=17 StartZ=0 EndX=-8 EndY=17 EndZ=0
    g1: LineSegment StartX=-5 StartY=0 StartZ=0 EndX=-14 EndY=0 EndZ=0
    g2: ArcOfCircle CenterX=-8.30801 CenterY=31.9434 CenterZ=0 NormalX=0 NormalY=0 NormalZ=1 AngleXU=0 Radius=14.9466 StartAngle=3.50569 EndAngle=4.733
    g3: ArcOfCircle CenterX=-12.819 CenterY=29.0329 CenterZ=0 NormalX=0 NormalY=0 NormalZ=1 AngleXU=0 Radius=29.0569 StartAngle=4.09262 EndAngle=4.67173
    g4: LineSegment StartX=-29.6965 StartY=5.38017 StartZ=0 EndX=-22.2748 EndY=26.6209 EndZ=0
    g5: LineSegment StartX=-15.5855 StartY=18.8882 StartZ=0 EndX=-22.7937 EndY=1.74171 EndZ=0
    g6: LineSegment StartX=-14 StartY=0 StartZ=0 EndX=-10.9422 EndY=17.2308 EndZ=0
    g7: LineSegment StartX=-5 StartY=17 StartZ=0 EndX=-5 EndY=0 EndZ=0
  constraints (19):
    c: Distance(g0) = 3
    c: Coincident(g0,g-3)
    c: Horizontal(g0)
    c: Distance(g1) = 9
    c: Coincident(g1,g-3)
    c: PointOnObject(g1,g-1)
    c: Coincident(g2,g0)
    c: Coincident(g3,g1)
    c: Coincident(g4,g3)
    c: Coincident(g4,g2)
    c: PointOnObject(g5,g2)
    c: PointOnObject(g5,g3)
    c: Coincident(g6,g1)
    c: PointOnObject(g6,g2)
    c: Coincident(g7,g0)
    c: Coincident(g7,g1)
    c: Distance(g6,g6) = 17.5
    c: Distance(g5,g5) = 18.6
    c: Distance(g4,g4) = 22.5
FEATURE [PartDesign::Plane] DatumPlane010
  AttachmentOffset = pos=(0,0,0) rot=(0,1,0;1.5708rad)
  AttachmentSupport = -> [Sketch020]
  Length = 60
  MapMode = 7
  Placement = pos=(-5,17,0) rot=(-0.57735,0.57735,0.57735;4.18879rad)
  ResizeMode = 0
  Width = 60
FEATURE [Sketcher::SketchObject] Sketch022
  ArcFitTolerance = 1e-06
  AttachmentSupport = -> [DatumPlane010]
  FullyConstrained = true
  MakeInternals = false
  MapMode = 5
  Placement = pos=(-5,17,0) rot=(0.57735,-0.57735,-0.57735;2.0944rad)
  sketch-geometry (5):
    g0: Ellipse CenterX=8.5 CenterY=0 CenterZ=0 NormalX=0 NormalY=0 NormalZ=1 MajorRadius=18 MinorRadius=8.5 AngleXU=1.5708
    g1: LineSegment [constr] StartX=8.5 StartY=18 StartZ=0 EndX=8.5 EndY=-18 EndZ=0
    g2: LineSegment [constr] StartX=2.89052e-11 StartY=0 StartZ=0 EndX=17 EndY=0 EndZ=0
    g3: GeomPoint [constr] X=8.5 Y=15.8666 Z=0
    g4: GeomPoint [constr] X=8.5 Y=-15.8666 Z=0
  constraints (6):
    c: InternalAlignment(g1-g4 -> g0) x4
    c: PointOnObject(g-1,g0)
    c: DistanceY(g1,g1) = 36
    c: DistanceX(g2,g2) = 17
    c: DistanceY(g2,g-1) = 0
    c: DistanceY(g-1,g2) = 0
FEATURE [PartDesign::Plane] DatumPlane011
  AttachmentOffset = pos=(0,0,0) rot=(0,1,0;1.5708rad)
  AttachmentSupport = -> [Sketch020]
  Length = 68.7347
  MapMode = 7
  Placement = pos=(-14,-4e-16,0) rot=(0.644821,0.540465,0.540465;1.99614rad)
  ResizeMode = 0
  Width = 60.7673
FEATURE [Sketcher::SketchObject] Sketch023
  ArcFitTolerance = 1e-06
  AttachmentSupport = -> [DatumPlane011]
  FullyConstrained = false
  MakeInternals = false
  MapMode = 5
  Placement = pos=(-14,-4e-16,0) rot=(0.644821,0.540465,0.540465;1.99614rad)
  sketch-geometry (5):
    g0: Ellipse CenterX=8.75 CenterY=0 CenterZ=0 NormalX=0 NormalY=0 NormalZ=1 MajorRadius=10 MinorRadius=8.75 AngleXU=1.56958
    g1: LineSegment [constr] StartX=8.76214 StartY=10 StartZ=0 EndX=8.73786 EndY=-10 EndZ=0
    g2: LineSegment [constr] StartX=7.95936e-06 StartY=0.0106227 StartZ=0 EndX=17.5 EndY=-0.0106227 EndZ=0
    g3: GeomPoint [constr] X=8.75588 Y=4.84124 Z=0
    g4: GeomPoint [constr] X=8.74413 Y=-4.84124 Z=0
  constraints (5):
    c: InternalAlignment(g1-g4 -> g0) x4
    c: PointOnObject(g-1,g0)
    c: DistanceY(g-1,g1) = 10
    c: DistanceX(g-1,g2) = 17.5
    c: DistanceY(g1,g-1) = 10
FEATURE [PartDesign::Plane] DatumPlane012
  AttachmentOffset = pos=(0,0,0) rot=(0,1,0;1.5708rad)
  AttachmentSupport = -> [Sketch020]
  Length = 76.9124
  MapMode = 7
  Placement = pos=(-15.5855,18.8882,0) rot=(-0.425205,0.64,0.64;3.94568rad)
  ResizeMode = 0
  Width = 61.4429
FEATURE [Sketcher::SketchObject] Sketch024
  ArcFitTolerance = 1e-06
  AttachmentSupport = -> [DatumPlane012]
  FullyConstrained = false
  MakeInternals = false
  MapMode = 5
  Placement = pos=(-15.5855,18.8882,0) rot=(-0.425205,0.64,0.64;3.94568rad)
  sketch-geometry (5):
    g0: Ellipse CenterX=9.3 CenterY=0 CenterZ=0 NormalX=0 NormalY=0 NormalZ=1 MajorRadius=9.3 MinorRadius=5 AngleXU=0
    g1: LineSegment [constr] StartX=18.6 StartY=0 StartZ=0 EndX=0 EndY=0 EndZ=0
    g2: LineSegment [constr] StartX=9.3 StartY=5 StartZ=0 EndX=9.3 EndY=-5 EndZ=0
    g3: GeomPoint [constr] X=17.1416 Y=0 Z=0
    g4: GeomPoint [constr] X=1.45844 Y=0 Z=0
  constraints (4):
    c: InternalAlignment(g1-g4 -> g0) x4
    c: PointOnObject(g-1,g0)
    c: DistanceY(g2,g2) = 10
    c: DistanceX(g-1,g1) = 18.6
FEATURE [PartDesign::Plane] DatumPlane013
  AttachmentOffset = pos=(0,0,0) rot=(0,1,0;1.5708rad)
  AttachmentSupport = -> [Sketch020]
  Length = 74.981
  MapMode = 7
  Placement = pos=(-29.6965,5.38017,0) rot=(0.705724,0.500976,0.500976;1.91248rad)
  ResizeMode = 0
  Width = 61.2867
FEATURE [Sketcher::SketchObject] Sketch025
  ArcFitTolerance = 1e-06
  AttachmentSupport = -> [DatumPlane013]
  FullyConstrained = true
  MakeInternals = false
  MapMode = 5
  Placement = pos=(-29.6965,5.38017,0) rot=(0.705724,0.500976,0.500976;1.91248rad)
  sketch-geometry (7):
    g0: LineSegment StartX=0 StartY=0 StartZ=0 EndX=22.5 EndY=0 EndZ=0
    g1: Ellipse CenterX=11.25 CenterY=7.11103e-07 CenterZ=0 NormalX=0 NormalY=0 NormalZ=1 MajorRadius=11.25 MinorRadius=3 AngleXU=-1e-16
    g2: LineSegment [constr] StartX=22.5 StartY=7.11103e-07 StartZ=0 EndX=0 EndY=7.11103e-07 EndZ=0
    g3: LineSegment [constr] StartX=11.25 StartY=3 StartZ=0 EndX=11.25 EndY=-3 EndZ=0
    g4: GeomPoint [constr] X=22.0926 Y=7.11103e-07 Z=0
    g5: GeomPoint [constr] X=0.407376 Y=7.11103e-07 Z=0
    g6: GeomPoint X=11.25 Y=7.11103e-07 Z=0
  constraints (10):
    c: Distance(g0) = 22.5
    c: Coincident(g0,g-1)
    c: Horizontal(g0)
    c: InternalAlignment(g2-g5 -> g1) x4
    c: PointOnObject(g0,g1)
    c: PointOnObject(g0,g1)
    c: Angle(g-1,g3) = 1.5708
    c: DistanceY(g3,g3) = 6
    c: DistanceX(g2,g2) = 22.5
    c: Coincident(g6,g1)
FEATURE [PartDesign::Plane] DatumPlane014
  AttachmentOffset = pos=(0,0,0) rot=(-0.57735,0.57735,0.57735;2.0944rad)
  AttachmentSupport = -> [Fillet004]
  Length = 159.901
  MapMode = 2
  Placement = pos=(15.3638,132.405,-1.1e-15) rot=(-0.388116,-0.651677,0.651677;2.40115rad)
  ResizeMode = 0
  Width = 66.9109
FEATURE [Sketcher::SketchObject] Sketch026
  ArcFitTolerance = 1e-06
  AttachmentSupport = -> [DatumPlane014]
  FullyConstrained = false
  MakeInternals = false
  MapMode = 5
  Placement = pos=(15.3638,132.405,-1.1e-15) rot=(0.388116,0.651677,-0.651677;3.88203rad)
  sketch-geometry (3):
    g0: LineSegment StartX=0 StartY=18.5458 StartZ=0 EndX=-15.6339 EndY=18.5458 EndZ=0
    g1: LineSegment StartX=-15.6339 StartY=18.5458 StartZ=0 EndX=0 EndY=8.71786 EndZ=0
    g2: LineSegment StartX=0 StartY=8.71786 StartZ=0 EndX=0 EndY=18.5458 EndZ=0
  constraints (6):
    c: PointOnObject(g0,g-2)
    c: Horizontal(g0)
    c: Coincident(g0,g1)
    c: PointOnObject(g1,g-2)
    c: Coincident(g1,g2)
    c: Coincident(g2,g0)
FEATURE [PartDesign::Fillet] Fillet005
  Base = -> Fillet004 [Edge11]
  BaseFeature = -> Fillet004
  Placement = pos=(4.3731,126.451,0) rot=(0.941347,0.238607,0.238607;1.6312rad)
  Radius = 7
  Refine = true
  SupportTransform = false
  Suppressed = false
  UseAllEdges = false
FEATURE [PartDesign::Plane] DatumPlane015
  AttachmentOffset = pos=(0,0,0) rot=(0,1,0;1.5708rad)
  AttachmentSupport = -> [Fillet005]
  Length = 159.901
  MapMode = 5
  Placement = pos=(4.3731,126.451,0) rot=(-0.764854,0.455521,-0.455521;1.83571rad)
  ResizeMode = 0
  Width = 66.9109
FEATURE [Sketcher::SketchObject] Sketch027
  ArcFitTolerance = 1e-06
  AttachmentSupport = -> [DatumPlane015]
  FullyConstrained = false
  MakeInternals = false
  MapMode = 5
  Placement = pos=(4.3731,126.451,0) rot=(-0.764854,0.455521,-0.455521;1.83571rad)
  sketch-geometry (3):
    g0: LineSegment StartX=-0.220754 StartY=-5.95898 StartZ=0 EndX=31.1422 EndY=-19.459 EndZ=0
    g1: LineSegment StartX=31.1422 StartY=-19.459 StartZ=0 EndX=-0.220754 EndY=-19.459 EndZ=0
    g2: LineSegment StartX=-0.220754 StartY=-19.459 StartZ=0 EndX=-0.220754 EndY=-5.95898 EndZ=0
  constraints (8):
    c: Coincident(g0,g1)
    c: Horizontal(g1)
    c: Vertical(g2)
    c: DistanceY(g2,g2) = 13.5
    c: DistanceX(g1) = -0.220754
    c: DistanceY(g1) = -19.459
    c: Coincident(g2,g1)
    c: Coincident(g0,g2)
FEATURE [Sketcher::SketchObject] Sketch028
  ArcFitTolerance = 1e-06
  AttachmentOffset = pos=(0,0,25) rot=(0,0,1;0rad)
  AttachmentSupport = -> [DatumPlane015]
  FullyConstrained = false
  MakeInternals = false
  MapMode = 5
  Placement = pos=(26.3546,138.359,0) rot=(-0.764854,0.455521,-0.455521;1.83571rad)
  sketch-geometry (3):
    g0: LineSegment StartX=0 StartY=-5.73 StartZ=0 EndX=29.8293 EndY=-18.73 EndZ=0
    g1: LineSegment StartX=29.8293 StartY=-18.73 StartZ=0 EndX=0 EndY=-18.73 EndZ=0
    g2: LineSegment StartX=0 StartY=-18.73 StartZ=0 EndX=0 EndY=-5.73 EndZ=0
  constraints (8):
    c: Coincident(g0,g1)
    c: Horizontal(g1)
    c: Coincident(g1,g2)
    c: Coincident(g2,g0)
    c: Vertical(g2)
    c: DistanceY(g2,g2) = 13
    c: DistanceX(g1) = 0
    c: DistanceY(g1) = -18.73
FEATURE [PartDesign::SubtractiveLoft] SubtractiveLoft
  BaseFeature = -> Fillet005
  Closed = false
  Placement = pos=(4.3731,126.451,0) rot=(0.941347,0.238607,0.238607;1.6312rad)
  Profile = -> Sketch027
  Refine = true
  Ruled = false
  Sections = -> [Sketch028]
  Suppressed = false
FEATURE [PartDesign::Fillet] Fillet006
  Base = -> SubtractiveLoft [Edge10]
  BaseFeature = -> SubtractiveLoft
  Placement = pos=(4.3731,126.451,0) rot=(0.941347,0.238607,0.238607;1.6312rad)
  Radius = 3
  Refine = true
  SupportTransform = false
  Suppressed = false
  UseAllEdges = false
FEATURE [PartDesign::Hole] Hole
  BaseFeature = -> Fillet006
  CustomThreadClearance = 0
  Depth = 314.154
  DepthType = 1
  Diameter = 3
  DrillForDepth = false
  DrillPoint = 1
  DrillPointAngle = 118
  HoleCutCountersinkAngle = 90
  HoleCutCustomValues = false
  HoleCutDepth = 8
  HoleCutDiameter = 6.1
  HoleCutType = 1
  ModelThread = false
  Placement = pos=(4.3731,126.451,0) rot=(0.941347,0.238607,0.238607;1.6312rad)
  Profile = -> Sketch013
  Refine = true
  Suppressed = false
  Tapered = false
  TaperedAngle = 90
  ThreadClass = 0
  ThreadDepth = 314.154
  ThreadDepthType = 0
  ThreadDirection = 0
  ThreadFit = 0
  ThreadSize = 0
  ThreadType = 0
  Threaded = false
  UseCustomThreadClearance = false
FEATURE [Sketcher::SketchObject] Sketch029
  ArcFitTolerance = 1e-06
  AttachmentSupport = -> [XY_Plane]
  FullyConstrained = true
  MakeInternals = false
  MapMode = 5
FEATURE [Sketcher::SketchObject] Sketch031
  ArcFitTolerance = 1e-06
  AttachmentSupport = -> [XY_Plane]
  FullyConstrained = true
  MakeInternals = false
  MapMode = 5
FEATURE [Sketcher::SketchObject] Sketch032
  ArcFitTolerance = 1e-06
  AttachmentSupport = -> [XY_Plane]
  FullyConstrained = true
  MakeInternals = false
  MapMode = 5
FEATURE [PartDesign::Body] Body
  AllowCompound = false
  Group = -> [Sketch,Sketch001,DatumPlane,DatumPlane001,DatumPlane002,Sketch002,Sketch004,AdditivePipe,DatumPlane004,Sketch006,DatumPlane005,Sketch007,DatumPlane006,Sketch008,DatumPlane007,Sketch009,DatumPlane008,Sketch010,DatumPlane009,Sketch011,Sketch012,Sketch013,Sketch014,Sketch015,Sketch016,Sketch017,Sketch018,AdditivePipe001,AdditivePipe002,Pad,Fillet,Fillet001,Fillet002,Fillet003,Fillet004,Sketch020,+20 more]
  Origin = -> Origin
  Tip = -> Hole
FEATURE [Part::Feature] oledpart001_solid  label="oledpart001 (Solid)"
  shape: bbox 67.74 x 108.1 x 4 mm, 10964 faces (baked)
FEATURE [Part::Refine] oledpart001_solid001  label="oledpart001 (Solid)001"
  Source = -> oledpart001_solid
FEATURE [Sketcher::SketchObject] Sketch035  label="oledsketch"
  ArcFitTolerance = 1e-06
  FullyConstrained = false
  MakeInternals = false
  sketch-geometry (2716):
    g0: LineSegment StartX=-18.9552 StartY=85.2966 StartZ=0 EndX=-18.9671 EndY=88.2448 EndZ=0
    g1: LineSegment StartX=-18.9671 StartY=88.2448 StartZ=0 EndX=-18.7934 EndY=91.1874 EndZ=0
    g2: LineSegment StartX=-18.7934 StartY=91.1874 StartZ=0 EndX=-18.4352 EndY=94.1135 EndZ=0
    g3: LineSegment StartX=-18.4352 StartY=94.1135 StartZ=0 EndX=-17.8933 EndY=97.0116 EndZ=0
    g4: LineSegment StartX=-17.8933 StartY=97.0116 StartZ=0 EndX=-17.1717 EndY=99.8707 EndZ=0
    g5: LineSegment StartX=-17.1717 StartY=99.8707 StartZ=0 EndX=-16.2713 EndY=102.677 EndZ=0
    g6: LineSegment StartX=-16.2713 StartY=102.677 StartZ=0 EndX=-15.197 EndY=105.424 EndZ=0
    g7: LineSegment StartX=-15.197 StartY=105.424 StartZ=0 EndX=-13.9527 EndY=108.096 EndZ=0
    g8: LineSegment StartX=-13.9527 StartY=108.096 StartZ=0 EndX=-12.5424 EndY=110.685 EndZ=0
    g9: LineSegment StartX=-12.5424 StartY=110.685 StartZ=0 EndX=-10.9727 EndY=113.18 EndZ=0
    g10: LineSegment StartX=-10.9727 StartY=113.18 StartZ=0 EndX=-9.24962 EndY=115.572 EndZ=0
    g11: LineSegment StartX=-9.24962 StartY=115.572 StartZ=0 EndX=-7.37994 EndY=117.852 EndZ=0
    g12: LineSegment StartX=-7.37994 StartY=117.852 StartZ=0 EndX=-5.37146 EndY=120.009 EndZ=0
    g13: LineSegment StartX=-5.37146 StartY=120.009 StartZ=0 EndX=-3.23002 EndY=122.037 EndZ=0
    g14: LineSegment StartX=-3.23002 StartY=122.037 StartZ=0 EndX=-0.966374 EndY=123.925 EndZ=0
    g15: LineSegment StartX=-0.966374 StartY=123.925 StartZ=0 EndX=1.41071 EndY=125.669 EndZ=0
    g16: LineSegment StartX=1.41071 StartY=125.669 StartZ=0 EndX=3.89342 EndY=127.258 EndZ=0
    g17: LineSegment StartX=3.89342 StartY=127.258 StartZ=0 EndX=6.47102 EndY=128.689 EndZ=0
    g18: LineSegment StartX=6.47102 StartY=128.689 StartZ=0 EndX=9.13278 EndY=129.957 EndZ=0
    g19: LineSegment StartX=9.13278 StartY=129.957 StartZ=0 EndX=9.6872 EndY=130.22 EndZ=0
    g20: LineSegment StartX=9.6872 StartY=130.22 StartZ=0 EndX=10.225 EndY=130.518 EndZ=0
    g21: LineSegment StartX=10.225 StartY=130.518 StartZ=0 EndX=10.7442 EndY=130.847 EndZ=0
    g22: LineSegment StartX=10.7442 StartY=130.847 StartZ=0 EndX=11.2408 EndY=131.208 EndZ=0
    g23: LineSegment StartX=11.2408 StartY=131.208 StartZ=0 EndX=11.7151 EndY=131.598 EndZ=0
    g24: LineSegment StartX=11.7151 StartY=131.598 StartZ=0 EndX=12.1638 EndY=132.018 EndZ=0
    g25: LineSegment StartX=12.1638 StartY=132.018 StartZ=0 EndX=12.5872 EndY=132.463 EndZ=0
    g26: LineSegment StartX=12.5872 StartY=132.463 StartZ=0 EndX=12.9812 EndY=132.935 EndZ=0
    g27: LineSegment StartX=12.9812 StartY=132.935 StartZ=0 EndX=13.3459 EndY=133.428 EndZ=0
    g28: LineSegment StartX=13.3459 StartY=133.428 StartZ=0 EndX=13.6794 EndY=133.944 EndZ=0
    g29: LineSegment StartX=13.6794 StartY=133.944 StartZ=0 EndX=13.9816 EndY=134.48 EndZ=0
    g30: LineSegment StartX=13.9816 StartY=134.48 StartZ=0 EndX=14.2495 EndY=135.033 EndZ=0
    g31: LineSegment StartX=14.2495 StartY=135.033 StartZ=0 EndX=14.4823 EndY=135.6 EndZ=0
    g32: LineSegment StartX=14.4823 StartY=135.6 StartZ=0 EndX=14.681 EndY=136.181 EndZ=0
    g33: LineSegment StartX=14.681 StartY=136.181 StartZ=0 EndX=17.554 EndY=145.541 EndZ=0
    g34: LineSegment StartX=17.554 StartY=145.541 StartZ=0 EndX=17.6337 EndY=145.832 EndZ=0
    g35: LineSegment StartX=17.6337 StartY=145.832 StartZ=0 EndX=17.6959 EndY=146.128 EndZ=0
    g36: LineSegment StartX=17.6959 StartY=146.128 StartZ=0 EndX=17.7405 EndY=146.427 EndZ=0
    g37: LineSegment StartX=17.7405 StartY=146.427 StartZ=0 EndX=17.7666 EndY=146.728 EndZ=0
    g38: LineSegment StartX=17.7666 StartY=146.728 StartZ=0 EndX=17.7741 EndY=147.029 EndZ=0
    g39: LineSegment StartX=17.7741 StartY=147.029 StartZ=0 EndX=17.764 EndY=147.331 EndZ=0
    g40: LineSegment StartX=17.764 StartY=147.331 StartZ=0 EndX=17.7354 EndY=147.632 EndZ=0
    g41: LineSegment StartX=17.7354 StartY=147.632 StartZ=0 EndX=17.6882 EndY=147.931 EndZ=0
    g42: LineSegment StartX=17.6882 StartY=147.931 StartZ=0 EndX=17.6234 EndY=148.226 EndZ=0
    g43: LineSegment StartX=17.6234 StartY=148.226 StartZ=0 EndX=17.5411 EndY=148.516 EndZ=0
    g44: LineSegment StartX=17.5411 StartY=148.516 StartZ=0 EndX=17.4412 EndY=148.802 EndZ=0
    g45: LineSegment StartX=17.4412 StartY=148.802 StartZ=0 EndX=17.3247 EndY=149.081 EndZ=0
    g46: LineSegment StartX=17.3247 StartY=149.081 StartZ=0 EndX=17.1916 EndY=149.352 EndZ=0
    g47: LineSegment StartX=17.1916 StartY=149.352 StartZ=0 EndX=17.0419 EndY=149.615 EndZ=0
    g48: LineSegment StartX=17.0419 StartY=149.615 StartZ=0 EndX=16.8766 EndY=149.867 EndZ=0
    g49: LineSegment StartX=16.8766 StartY=149.867 StartZ=0 EndX=16.6957 EndY=150.109 EndZ=0
    g50: LineSegment StartX=16.6957 StartY=150.109 StartZ=0 EndX=16.5011 EndY=150.341 EndZ=0
    g51: LineSegment StartX=16.5011 StartY=150.341 StartZ=0 EndX=16.2938 EndY=150.56 EndZ=0
    g52: LineSegment StartX=16.2938 StartY=150.56 StartZ=0 EndX=16.0719 EndY=150.766 EndZ=0
    g53: LineSegment StartX=16.0719 StartY=150.766 StartZ=0 EndX=15.8393 EndY=150.958 EndZ=0
    g54: LineSegment StartX=15.8393 StartY=150.958 StartZ=0 EndX=15.595 EndY=151.137 EndZ=0
    g55: LineSegment StartX=15.595 StartY=151.137 StartZ=0 EndX=15.3409 EndY=151.299 EndZ=0
    g56: LineSegment StartX=15.3409 StartY=151.299 StartZ=0 EndX=15.0771 EndY=151.447 EndZ=0
    g57: LineSegment StartX=15.0771 StartY=151.447 StartZ=0 EndX=14.8045 EndY=151.577 EndZ=0
    g58: LineSegment StartX=14.8045 StartY=151.577 StartZ=0 EndX=14.5251 EndY=151.692 EndZ=0
    g59: LineSegment StartX=14.5251 StartY=151.692 StartZ=0 EndX=0.64951 EndY=156.877 EndZ=0
    g60: LineSegment StartX=0.64951 StartY=156.877 StartZ=0 EndX=0.0887629 EndY=157.068 EndZ=0
    g61: LineSegment StartX=0.0887629 StartY=157.068 StartZ=0 EndX=-0.481714 EndY=157.224 EndZ=0
    g62: LineSegment StartX=-0.481714 StartY=157.224 StartZ=0 EndX=-1.05997 EndY=157.348 EndZ=0
    g63: LineSegment StartX=-1.05997 StartY=157.348 StartZ=0 EndX=-1.64502 EndY=157.436 EndZ=0
    g64: LineSegment StartX=-1.64502 StartY=157.436 StartZ=0 EndX=-2.23395 EndY=157.49 EndZ=0
    g65: LineSegment StartX=-2.23395 StartY=157.49 StartZ=0 EndX=-2.82479 EndY=157.509 EndZ=0
    g66: LineSegment StartX=-2.82479 StartY=157.509 StartZ=0 EndX=-3.41657 EndY=157.494 EndZ=0
    g67: LineSegment StartX=-3.41657 StartY=157.494 StartZ=0 EndX=-4.00636 EndY=157.442 EndZ=0
    g68: LineSegment StartX=-4.00636 StartY=157.442 StartZ=0 EndX=-4.59123 EndY=157.357 EndZ=0
    g69: LineSegment StartX=-4.59123 StartY=157.357 StartZ=0 EndX=-5.17021 EndY=157.237 EndZ=0
    g70: LineSegment StartX=-5.17021 StartY=157.237 StartZ=0 EndX=-5.74133 EndY=157.083 EndZ=0
    g71: LineSegment StartX=-5.74133 StartY=157.083 StartZ=0 EndX=-6.30266 EndY=156.895 EndZ=0
    g72: LineSegment StartX=-6.30266 StartY=156.895 StartZ=0 EndX=-6.85126 EndY=156.675 EndZ=0
    g73: LineSegment StartX=-6.85126 StartY=156.675 StartZ=0 EndX=-7.38615 EndY=156.422 EndZ=0
    g74: LineSegment StartX=-7.38615 StartY=156.422 StartZ=0 EndX=-11.6513 EndY=154.082 EndZ=0
    g75: LineSegment StartX=-11.6513 StartY=154.082 StartZ=0 EndX=-15.7618 EndY=151.48 EndZ=0
    g76: LineSegment StartX=-15.7618 StartY=151.48 StartZ=0 EndX=-19.7012 EndY=148.626 EndZ=0
    g77: LineSegment StartX=-19.7012 StartY=148.626 StartZ=0 EndX=-23.4558 EndY=145.532 EndZ=0
    g78: LineSegment StartX=-23.4558 StartY=145.532 StartZ=0 EndX=-27.01 EndY=142.211 EndZ=0
    g79: LineSegment StartX=-27.01 StartY=142.211 StartZ=0 EndX=-30.35 EndY=138.674 EndZ=0
    g80: LineSegment StartX=-30.35 StartY=138.674 StartZ=0 EndX=-33.4633 EndY=134.936 EndZ=0
    g81: LineSegment StartX=-33.4633 StartY=134.936 StartZ=0 EndX=-36.3371 EndY=131.011 EndZ=0
    g82: LineSegment StartX=-36.3371 StartY=131.011 StartZ=0 EndX=-38.9598 EndY=126.914 EndZ=0
    g83: LineSegment StartX=-38.9598 StartY=126.914 StartZ=0 EndX=-41.3225 EndY=122.662 EndZ=0
    g84: LineSegment StartX=-41.3225 StartY=122.662 StartZ=0 EndX=-43.4156 EndY=118.27 EndZ=0
    g85: LineSegment StartX=-43.4156 StartY=118.27 StartZ=0 EndX=-45.2302 EndY=113.756 EndZ=0
    g86: LineSegment StartX=-45.2302 StartY=113.756 StartZ=0 EndX=-46.7595 EndY=109.139 EndZ=0
    g87: LineSegment StartX=-46.7595 StartY=109.139 StartZ=0 EndX=-47.9987 EndY=104.434 EndZ=0
    g88: LineSegment StartX=-47.9987 StartY=104.434 StartZ=0 EndX=-48.941 EndY=99.6617 EndZ=0
    g89: LineSegment StartX=-48.941 StartY=99.6617 StartZ=0 EndX=-49.5844 EndY=94.8397 EndZ=0
    g90: LineSegment StartX=-49.5844 StartY=94.8397 StartZ=0 EndX=-49.926 EndY=89.9868 EndZ=0
    g91: LineSegment StartX=-49.926 StartY=89.9868 StartZ=0 EndX=-49.9629 EndY=85.1225 EndZ=0
    g92: LineSegment StartX=-49.9629 StartY=85.1225 StartZ=0 EndX=-49.698 EndY=80.2654 EndZ=0
    g93: LineSegment StartX=-49.698 StartY=80.2654 StartZ=0 EndX=-49.1295 EndY=75.4339 EndZ=0
    g94: LineSegment StartX=-49.1295 StartY=75.4339 StartZ=0 EndX=-48.2612 EndY=70.6477 EndZ=0
    g95: LineSegment StartX=-48.2612 StartY=70.6477 StartZ=0 EndX=-47.0961 EndY=65.9243 EndZ=0
    g96: LineSegment StartX=-47.0961 StartY=65.9243 StartZ=0 EndX=-45.6381 EndY=61.2833 EndZ=0
    g97: LineSegment StartX=-45.6381 StartY=61.2833 StartZ=0 EndX=-43.8941 EndY=56.7421 EndZ=0
    g98: LineSegment StartX=-43.8941 StartY=56.7421 StartZ=0 EndX=-43.6347 EndY=56.175 EndZ=0
    g99: LineSegment StartX=-43.6347 StartY=56.175 StartZ=0 EndX=-43.3412 EndY=55.6255 EndZ=0
    g100: LineSegment StartX=-43.3412 StartY=55.6255 StartZ=0 EndX=-43.0125 EndY=55.0956 EndZ=0
    g101: LineSegment StartX=-43.0125 StartY=55.0956 StartZ=0 EndX=-42.6526 EndY=54.5872 EndZ=0
    g102: LineSegment StartX=-42.6526 StartY=54.5872 StartZ=0 EndX=-42.2614 EndY=54.1013 EndZ=0
    g103: LineSegment StartX=-42.2614 StartY=54.1013 StartZ=0 EndX=-41.841 EndY=53.6417 EndZ=0
    g104: LineSegment StartX=-41.841 StartY=53.6417 StartZ=0 EndX=-41.3923 EndY=53.2086 EndZ=0
    g105: LineSegment StartX=-41.3923 StartY=53.2086 StartZ=0 EndX=-40.9183 EndY=52.8048 EndZ=0
    g106: LineSegment StartX=-40.9183 StartY=52.8048 StartZ=0 EndX=-40.4189 EndY=52.4313 EndZ=0
    g107: LineSegment StartX=-40.4189 StartY=52.4313 StartZ=0 EndX=-39.898 EndY=52.0891 EndZ=0
    g108: LineSegment StartX=-39.898 StartY=52.0891 StartZ=0 EndX=-39.3567 EndY=51.7801 EndZ=0
    g109: LineSegment StartX=-39.3567 StartY=51.7801 StartZ=0 EndX=-38.7968 EndY=51.5053 EndZ=0
    g110: LineSegment StartX=-38.7968 StartY=51.5053 StartZ=0 EndX=-38.2214 EndY=51.2666 EndZ=0
    g111: LineSegment StartX=-38.2214 StartY=51.2666 StartZ=0 EndX=-37.6323 EndY=51.0641 EndZ=0
    g112: LineSegment StartX=-37.6323 StartY=51.0641 StartZ=0 EndX=-37.0315 EndY=50.8987 EndZ=0
    g113: LineSegment StartX=-37.0315 StartY=50.8987 StartZ=0 EndX=-36.421 EndY=50.7705 EndZ=0
    g114: LineSegment StartX=-36.421 StartY=50.7705 StartZ=0 EndX=-35.8047 EndY=50.6813 EndZ=0
    g115: LineSegment StartX=-35.8047 StartY=50.6813 StartZ=0 EndX=-25.3386 EndY=49.492 EndZ=0
    g116: LineSegment StartX=-25.3386 StartY=49.492 StartZ=0 EndX=-25.3396 EndY=49.4803 EndZ=0
    g117: LineSegment StartX=-25.3396 StartY=49.4803 StartZ=0 EndX=-25.0339 EndY=49.4552 EndZ=0
    g118: LineSegment StartX=-25.0339 StartY=49.4552 StartZ=0 EndX=-24.7273 EndY=49.4487 EndZ=0
    g119: LineSegment StartX=-24.7273 StartY=49.4487 StartZ=0 EndX=-24.4216 EndY=49.4608 EndZ=0
    g120: LineSegment StartX=-24.4216 StartY=49.4608 StartZ=0 EndX=-24.117 EndY=49.4914 EndZ=0
    g121: LineSegment StartX=-24.117 StartY=49.4914 StartZ=0 EndX=-23.8143 EndY=49.5415 EndZ=0
    g122: LineSegment StartX=-23.8143 StartY=49.5415 StartZ=0 EndX=-23.5155 EndY=49.6092 EndZ=0
    g123: LineSegment StartX=-23.5155 StartY=49.6092 StartZ=0 EndX=-23.2207 EndY=49.6954 EndZ=0
    g124: LineSegment StartX=-23.2207 StartY=49.6954 StartZ=0 EndX=-22.9327 EndY=49.8002 EndZ=0
    g125: LineSegment StartX=-22.9327 StartY=49.8002 StartZ=0 EndX=-22.6516 EndY=49.9216 EndZ=0
    g126: LineSegment StartX=-22.6516 StartY=49.9216 StartZ=0 EndX=-22.3783 EndY=50.0606 EndZ=0
    g127: LineSegment StartX=-22.3783 StartY=50.0606 StartZ=0 EndX=-22.1138 EndY=50.2151 EndZ=0
    g128: LineSegment StartX=-22.1138 StartY=50.2151 StartZ=0 EndX=-21.8591 EndY=50.3863 EndZ=0
    g129: LineSegment StartX=-21.8591 StartY=50.3863 StartZ=0 EndX=-21.6161 EndY=50.5731 EndZ=0
    g130: LineSegment StartX=-21.6161 StartY=50.5731 StartZ=0 EndX=-21.3849 EndY=50.7735 EndZ=0
    g131: LineSegment StartX=-21.3849 StartY=50.7735 StartZ=0 EndX=-21.1654 EndY=50.9886 EndZ=0
    g132: LineSegment StartX=-21.1654 StartY=50.9886 StartZ=0 EndX=-20.9606 EndY=51.2154 EndZ=0
    g133: LineSegment StartX=-20.9606 StartY=51.2154 StartZ=0 EndX=-20.7694 EndY=51.4558 EndZ=0
    g134: LineSegment StartX=-20.7694 StartY=51.4558 StartZ=0 EndX=-14.2327 EndY=60.2058 EndZ=0
    g135: LineSegment StartX=-14.2327 StartY=60.2058 StartZ=0 EndX=-14.0552 EndY=60.4599 EndZ=0
    g136: LineSegment StartX=-14.0552 StartY=60.4599 StartZ=0 EndX=-13.8934 EndY=60.7247 EndZ=0
    g137: LineSegment StartX=-13.8934 StartY=60.7247 StartZ=0 EndX=-13.7481 EndY=60.9983 EndZ=0
    g138: LineSegment StartX=-13.7481 StartY=60.9983 StartZ=0 EndX=-13.6205 EndY=61.2816 EndZ=0
    g139: LineSegment StartX=-13.6205 StartY=61.2816 StartZ=0 EndX=-13.5105 EndY=61.5708 EndZ=0
    g140: LineSegment StartX=-13.5105 StartY=61.5708 StartZ=0 EndX=-13.419 EndY=61.8668 EndZ=0
    g141: LineSegment StartX=-13.419 StartY=61.8668 StartZ=0 EndX=-13.3451 EndY=62.1687 EndZ=0
    g142: LineSegment StartX=-13.3451 StartY=62.1687 StartZ=0 EndX=-13.2907 EndY=62.4734 EndZ=0
    g143: LineSegment StartX=-13.2907 StartY=62.4734 StartZ=0 EndX=-13.2559 EndY=62.782 EndZ=0
    g144: LineSegment StartX=-13.2559 StartY=62.782 StartZ=0 EndX=-13.2396 EndY=63.0916 EndZ=0
    g145: LineSegment StartX=-13.2396 StartY=63.0916 StartZ=0 EndX=-13.2419 EndY=63.4012 EndZ=0
    g146: LineSegment StartX=-13.2419 StartY=63.4012 StartZ=0 EndX=-13.2647 EndY=63.7107 EndZ=0
    g147: LineSegment StartX=-13.2647 StartY=63.7107 StartZ=0 EndX=-13.306 EndY=64.0183 EndZ=0
    g148: LineSegment StartX=-13.306 StartY=64.0183 StartZ=0 EndX=-13.3659 EndY=64.322 EndZ=0
    g149: LineSegment StartX=-13.3659 StartY=64.322 StartZ=0 EndX=-13.4453 EndY=64.6217 EndZ=0
    g150: LineSegment StartX=-13.4453 StartY=64.6217 StartZ=0 EndX=-13.5423 EndY=64.9165 EndZ=0
    g151: LineSegment StartX=-13.5423 StartY=64.9165 StartZ=0 EndX=-13.6578 EndY=65.2045 EndZ=0
    g152: LineSegment StartX=-13.6578 StartY=65.2045 StartZ=0 EndX=-13.7909 EndY=65.4846 EndZ=0
    g153: LineSegment StartX=-13.7909 StartY=65.4846 StartZ=0 EndX=-15.0564 EndY=68.1473 EndZ=0
    g154: LineSegment StartX=-15.0564 StartY=68.1473 StartZ=0 EndX=-16.1511 EndY=70.8845 EndZ=0
    g155: LineSegment StartX=-16.1511 StartY=70.8845 StartZ=0 EndX=-17.072 EndY=73.6853 EndZ=0
    g156: LineSegment StartX=-17.072 StartY=73.6853 StartZ=0 EndX=-17.8162 EndY=76.538 EndZ=0
    g157: LineSegment StartX=-17.8162 StartY=76.538 StartZ=0 EndX=-18.3788 EndY=79.4319 EndZ=0
    g158: LineSegment StartX=-18.3788 StartY=79.4319 StartZ=0 EndX=-18.7598 EndY=82.3554 EndZ=0
    g159: LineSegment StartX=-18.7598 StartY=82.3554 StartZ=0 EndX=-18.9552 EndY=85.2966 EndZ=0
    g160: LineSegment StartX=-20.1558 StartY=79.143 StartZ=0 EndX=-19.5716 EndY=76.1387 EndZ=0
    g161: LineSegment StartX=-19.5716 StartY=76.1387 StartZ=0 EndX=-18.799 EndY=73.1766 EndZ=0
    g162: LineSegment StartX=-18.799 StartY=73.1766 StartZ=0 EndX=-17.8428 EndY=70.2684 EndZ=0
    g163: LineSegment StartX=-17.8428 StartY=70.2684 StartZ=0 EndX=-16.7051 EndY=67.4269 EndZ=0
    g164: LineSegment StartX=-16.7051 StartY=67.4269 StartZ=0 EndX=-15.3916 EndY=64.6616 EndZ=0
    g165: LineSegment StartX=-15.3916 StartY=64.6616 StartZ=0 EndX=-15.3065 EndY=64.482 EndZ=0
    g166: LineSegment StartX=-15.3065 StartY=64.482 StartZ=0 EndX=-15.233 EndY=64.2975 EndZ=0
    g167: LineSegment StartX=-15.233 StartY=64.2975 StartZ=0 EndX=-15.1703 EndY=64.1091 EndZ=0
    g168: LineSegment StartX=-15.1703 StartY=64.1091 StartZ=0 EndX=-15.1203 EndY=63.9178 EndZ=0
    g169: LineSegment StartX=-15.1203 StartY=63.9178 StartZ=0 EndX=-15.0811 EndY=63.7235 EndZ=0
    g170: LineSegment StartX=-15.0811 StartY=63.7235 StartZ=0 EndX=-15.0545 EndY=63.5262 EndZ=0
    g171: LineSegment StartX=-15.0545 StartY=63.5262 StartZ=0 EndX=-15.0406 EndY=63.328 EndZ=0
    g172: LineSegment StartX=-15.0406 StartY=63.328 StartZ=0 EndX=-15.0385 EndY=63.1298 EndZ=0
    g173: LineSegment StartX=-15.0385 StartY=63.1298 StartZ=0 EndX=-15.049 EndY=62.9315 EndZ=0
    g174: LineSegment StartX=-15.049 StartY=62.9315 StartZ=0 EndX=-15.0722 EndY=62.7342 EndZ=0
    g175: LineSegment StartX=-15.0722 StartY=62.7342 StartZ=0 EndX=-15.1072 EndY=62.5389 EndZ=0
    g176: LineSegment StartX=-15.1072 StartY=62.5389 StartZ=0 EndX=-15.1539 EndY=62.3464 EndZ=0
    g177: LineSegment StartX=-15.1539 StartY=62.3464 StartZ=0 EndX=-15.2122 EndY=62.1569 EndZ=0
    g178: LineSegment StartX=-15.2122 StartY=62.1569 StartZ=0 EndX=-15.2824 EndY=61.9713 EndZ=0
    g179: LineSegment StartX=-15.2824 StartY=61.9713 StartZ=0 EndX=-15.3642 EndY=61.7906 EndZ=0
    g180: LineSegment StartX=-15.3642 StartY=61.7906 StartZ=0 EndX=-15.4568 EndY=61.6147 EndZ=0
    g181: LineSegment StartX=-15.4568 StartY=61.6147 StartZ=0 EndX=-15.5611 EndY=61.4456 EndZ=0
    g182: LineSegment StartX=-15.5611 StartY=61.4456 StartZ=0 EndX=-15.6742 EndY=61.2834 EndZ=0
    g183: LineSegment StartX=-15.6742 StartY=61.2834 StartZ=0 EndX=-22.2119 EndY=52.5334 EndZ=0
    g184: LineSegment StartX=-22.2119 StartY=52.5334 StartZ=0 EndX=-22.3338 EndY=52.379 EndZ=0
    g185: LineSegment StartX=-22.3338 StartY=52.379 StartZ=0 EndX=-22.4655 EndY=52.2333 EndZ=0
    g186: LineSegment StartX=-22.4655 StartY=52.2333 StartZ=0 EndX=-22.605 EndY=52.0965 EndZ=0
    g187: LineSegment StartX=-22.605 StartY=52.0965 StartZ=0 EndX=-22.7533 EndY=51.9674 EndZ=0
    g188: LineSegment StartX=-22.7533 StartY=51.9674 StartZ=0 EndX=-22.9095 EndY=51.8481 EndZ=0
    g189: LineSegment StartX=-22.9095 StartY=51.8481 StartZ=0 EndX=-23.0715 EndY=51.7395 EndZ=0
    g190: LineSegment StartX=-23.0715 StartY=51.7395 StartZ=0 EndX=-23.2413 EndY=51.6397 EndZ=0
    g191: LineSegment StartX=-23.2413 StartY=51.6397 StartZ=0 EndX=-23.416 EndY=51.5507 EndZ=0
    g192: LineSegment StartX=-23.416 StartY=51.5507 StartZ=0 EndX=-23.5956 EndY=51.4733 EndZ=0
    g193: LineSegment StartX=-23.5956 StartY=51.4733 StartZ=0 EndX=-23.7801 EndY=51.4067 EndZ=0
    g194: LineSegment StartX=-23.7801 StartY=51.4067 StartZ=0 EndX=-23.9685 EndY=51.3509 EndZ=0
    g195: LineSegment StartX=-23.9685 StartY=51.3509 StartZ=0 EndX=-24.1599 EndY=51.3077 EndZ=0
    g196: LineSegment StartX=-24.1599 StartY=51.3077 StartZ=0 EndX=-24.3532 EndY=51.2763 EndZ=0
    g197: LineSegment StartX=-24.3532 StartY=51.2763 StartZ=0 EndX=-24.5485 EndY=51.2565 EndZ=0
    g198: LineSegment StartX=-24.5485 StartY=51.2565 StartZ=0 EndX=-24.7448 EndY=51.2485 EndZ=0
    g199: LineSegment StartX=-24.7448 StartY=51.2485 StartZ=0 EndX=-24.9411 EndY=51.2522 EndZ=0
    g200: LineSegment StartX=-24.9411 StartY=51.2522 StartZ=0 EndX=-25.1364 EndY=51.2686 EndZ=0
    g201: LineSegment StartX=-25.1364 StartY=51.2686 StartZ=0 EndX=-25.1354 EndY=51.2803 EndZ=0
    g202: LineSegment StartX=-25.1354 StartY=51.2803 StartZ=0 EndX=-35.6015 EndY=52.4696 EndZ=0
    g203: LineSegment StartX=-35.6015 StartY=52.4696 StartZ=0 EndX=-36.1065 EndY=52.5433 EndZ=0
    g204: LineSegment StartX=-36.1065 StartY=52.5433 StartZ=0 EndX=-36.6076 EndY=52.6472 EndZ=0
    g205: LineSegment StartX=-36.6076 StartY=52.6472 StartZ=0 EndX=-37.0999 EndY=52.7834 EndZ=0
    g206: LineSegment StartX=-37.0999 StartY=52.7834 StartZ=0 EndX=-37.5835 EndY=52.9499 EndZ=0
    g207: LineSegment StartX=-37.5835 StartY=52.9499 StartZ=0 EndX=-38.0554 EndY=53.1457 EndZ=0
    g208: LineSegment StartX=-38.0554 StartY=53.1457 StartZ=0 EndX=-38.5136 EndY=53.3708 EndZ=0
    g209: LineSegment StartX=-38.5136 StartY=53.3708 StartZ=0 EndX=-38.9582 EndY=53.6243 EndZ=0
    g210: LineSegment StartX=-38.9582 StartY=53.6243 StartZ=0 EndX=-39.3853 EndY=53.9041 EndZ=0
    g211: LineSegment StartX=-39.3853 StartY=53.9041 StartZ=0 EndX=-39.7948 EndY=54.2113 EndZ=0
    g212: LineSegment StartX=-39.7948 StartY=54.2113 StartZ=0 EndX=-40.1838 EndY=54.5419 EndZ=0
    g213: LineSegment StartX=-40.1838 StartY=54.5419 StartZ=0 EndX=-40.5513 EndY=54.897 EndZ=0
    g214: LineSegment StartX=-40.5513 StartY=54.897 StartZ=0 EndX=-40.8965 EndY=55.2746 EndZ=0
    g215: LineSegment StartX=-40.8965 StartY=55.2746 StartZ=0 EndX=-41.2172 EndY=55.6717 EndZ=0
    g216: LineSegment StartX=-41.2172 StartY=55.6717 StartZ=0 EndX=-41.5125 EndY=56.0894 EndZ=0
    g217: LineSegment StartX=-41.5125 StartY=56.0894 StartZ=0 EndX=-41.7806 EndY=56.5236 EndZ=0
    g218: LineSegment StartX=-41.7806 StartY=56.5236 StartZ=0 EndX=-42.0223 EndY=56.9746 EndZ=0
    g219: LineSegment StartX=-42.0223 StartY=56.9746 StartZ=0 EndX=-42.2347 EndY=57.4392 EndZ=0
    g220: LineSegment StartX=-42.2347 StartY=57.4392 StartZ=0 EndX=-43.9385 EndY=61.8759 EndZ=0
    g221: LineSegment StartX=-43.9385 StartY=61.8759 StartZ=0 EndX=-45.3622 EndY=66.4095 EndZ=0
    g222: LineSegment StartX=-45.3622 StartY=66.4095 StartZ=0 EndX=-46.5008 EndY=71.0236 EndZ=0
    g223: LineSegment StartX=-46.5008 StartY=71.0236 StartZ=0 EndX=-47.3495 EndY=75.6995 EndZ=0
    g224: LineSegment StartX=-47.3495 StartY=75.6995 StartZ=0 EndX=-47.9042 EndY=80.4196 EndZ=0
    g225: LineSegment StartX=-47.9042 StartY=80.4196 StartZ=0 EndX=-48.1641 EndY=85.1644 EndZ=0
    g226: LineSegment StartX=-48.1641 StartY=85.1644 StartZ=0 EndX=-48.1271 EndY=89.9164 EndZ=0
    g227: LineSegment StartX=-48.1271 StartY=89.9164 StartZ=0 EndX=-47.7932 EndY=94.658 EndZ=0
    g228: LineSegment StartX=-47.7932 StartY=94.658 StartZ=0 EndX=-47.1653 EndY=99.3686 EndZ=0
    g229: LineSegment StartX=-47.1653 StartY=99.3686 StartZ=0 EndX=-46.2444 EndY=104.031 EndZ=0
    g230: LineSegment StartX=-46.2444 StartY=104.031 StartZ=0 EndX=-45.0344 EndY=108.626 EndZ=0
    g231: LineSegment StartX=-45.0344 StartY=108.626 StartZ=0 EndX=-43.5401 EndY=113.137 EndZ=0
    g232: LineSegment StartX=-43.5401 StartY=113.137 StartZ=0 EndX=-41.7673 EndY=117.547 EndZ=0
    g233: LineSegment StartX=-41.7673 StartY=117.547 StartZ=0 EndX=-39.723 EndY=121.836 EndZ=0
    g234: LineSegment StartX=-39.723 StartY=121.836 StartZ=0 EndX=-37.4148 EndY=125.991 EndZ=0
    g235: LineSegment StartX=-37.4148 StartY=125.991 StartZ=0 EndX=-34.8517 EndY=129.993 EndZ=0
    g236: LineSegment StartX=-34.8517 StartY=129.993 StartZ=0 EndX=-32.0441 EndY=133.828 EndZ=0
    g237: LineSegment StartX=-32.0441 StartY=133.828 StartZ=0 EndX=-29.004 EndY=137.479 EndZ=0
    g238: LineSegment StartX=-29.004 StartY=137.479 StartZ=0 EndX=-25.741 EndY=140.935 EndZ=0
    g239: LineSegment StartX=-25.741 StartY=140.935 StartZ=0 EndX=-22.2688 EndY=144.18 EndZ=0
    g240: LineSegment StartX=-22.2688 StartY=144.18 StartZ=0 EndX=-18.6011 EndY=147.202 EndZ=0
    g241: LineSegment StartX=-18.6011 StartY=147.202 StartZ=0 EndX=-14.7515 EndY=149.989 EndZ=0
    g242: LineSegment StartX=-14.7515 StartY=149.989 StartZ=0 EndX=-10.7366 EndY=152.531 EndZ=0
    g243: LineSegment StartX=-10.7366 StartY=152.531 StartZ=0 EndX=-6.57002 EndY=154.817 EndZ=0
    g244: LineSegment StartX=-6.57002 StartY=154.817 StartZ=0 EndX=-6.13176 EndY=155.025 EndZ=0
    g245: LineSegment StartX=-6.13176 StartY=155.025 StartZ=0 EndX=-5.68175 EndY=155.205 EndZ=0
    g246: LineSegment StartX=-5.68175 StartY=155.205 StartZ=0 EndX=-5.22097 EndY=155.359 EndZ=0
    g247: LineSegment StartX=-5.22097 StartY=155.359 StartZ=0 EndX=-4.75333 EndY=155.485 EndZ=0
    g248: LineSegment StartX=-4.75333 StartY=155.485 StartZ=0 EndX=-4.27785 EndY=155.584 EndZ=0
    g249: LineSegment StartX=-4.27785 StartY=155.584 StartZ=0 EndX=-3.79843 EndY=155.654 EndZ=0
    g250: LineSegment StartX=-3.79843 StartY=155.654 StartZ=0 EndX=-3.31508 EndY=155.696 EndZ=0
    g251: LineSegment StartX=-3.31508 StartY=155.696 StartZ=0 EndX=-2.82974 EndY=155.709 EndZ=0
    g252: LineSegment StartX=-2.82974 StartY=155.709 StartZ=0 EndX=-2.34535 EndY=155.694 EndZ=0
    g253: LineSegment StartX=-2.34535 StartY=155.694 StartZ=0 EndX=-1.8619 EndY=155.649 EndZ=0
    g254: LineSegment StartX=-1.8619 StartY=155.649 StartZ=0 EndX=-1.38233 EndY=155.577 EndZ=0
    g255: LineSegment StartX=-1.38233 StartY=155.577 StartZ=0 EndX=-0.907618 EndY=155.476 EndZ=0
    g256: LineSegment StartX=-0.907618 StartY=155.476 StartZ=0 EndX=-0.440686 EndY=155.347 EndZ=0
    g257: LineSegment StartX=-0.440686 StartY=155.347 StartZ=0 EndX=0.0194394 EndY=155.191 EndZ=0
    g258: LineSegment StartX=0.0194394 StartY=155.191 StartZ=0 EndX=13.895 EndY=150.006 EndZ=0
    g259: LineSegment StartX=13.895 StartY=150.006 StartZ=0 EndX=14.0738 EndY=149.933 EndZ=0
    g260: LineSegment StartX=14.0738 StartY=149.933 StartZ=0 EndX=14.2477 EndY=149.849 EndZ=0
    g261: LineSegment StartX=14.2477 StartY=149.849 StartZ=0 EndX=14.4167 EndY=149.754 EndZ=0
    g262: LineSegment StartX=14.4167 StartY=149.754 StartZ=0 EndX=14.5799 EndY=149.65 EndZ=0
    g263: LineSegment StartX=14.5799 StartY=149.65 StartZ=0 EndX=14.7363 EndY=149.536 EndZ=0
    g264: LineSegment StartX=14.7363 StartY=149.536 StartZ=0 EndX=14.8849 EndY=149.413 EndZ=0
    g265: LineSegment StartX=14.8849 StartY=149.413 StartZ=0 EndX=15.0266 EndY=149.281 EndZ=0
    g266: LineSegment StartX=15.0266 StartY=149.281 StartZ=0 EndX=15.1596 EndY=149.141 EndZ=0
    g267: LineSegment StartX=15.1596 StartY=149.141 StartZ=0 EndX=15.2847 EndY=148.993 EndZ=0
    g268: LineSegment StartX=15.2847 StartY=148.993 StartZ=0 EndX=15.3991 EndY=148.837 EndZ=0
    g269: LineSegment StartX=15.3991 StartY=148.837 StartZ=0 EndX=15.5058 EndY=148.675 EndZ=0
    g270: LineSegment StartX=15.5058 StartY=148.675 StartZ=0 EndX=15.6007 EndY=148.508 EndZ=0
    g271: LineSegment StartX=15.6007 StartY=148.508 StartZ=0 EndX=15.6868 EndY=148.335 EndZ=0
    g272: LineSegment StartX=15.6868 StartY=148.335 StartZ=0 EndX=15.7612 EndY=148.156 EndZ=0
    g273: LineSegment StartX=15.7612 StartY=148.156 StartZ=0 EndX=15.8249 EndY=147.974 EndZ=0
    g274: LineSegment StartX=15.8249 StartY=147.974 StartZ=0 EndX=15.8778 EndY=147.787 EndZ=0
    g275: LineSegment StartX=15.8778 StartY=147.787 StartZ=0 EndX=15.919 EndY=147.599 EndZ=0
    g276: LineSegment StartX=15.919 StartY=147.599 StartZ=0 EndX=15.9495 EndY=147.407 EndZ=0
    g277: LineSegment StartX=15.9495 StartY=147.407 StartZ=0 EndX=15.9673 EndY=147.215 EndZ=0
    g278: LineSegment StartX=15.9673 StartY=147.215 StartZ=0 EndX=15.9743 EndY=147.022 EndZ=0
    g279: LineSegment StartX=15.9743 StartY=147.022 StartZ=0 EndX=15.9696 EndY=146.828 EndZ=0
    g280: LineSegment StartX=15.9696 StartY=146.828 StartZ=0 EndX=15.9532 EndY=146.636 EndZ=0
    g281: LineSegment StartX=15.9532 StartY=146.636 StartZ=0 EndX=15.9241 EndY=146.444 EndZ=0
    g282: LineSegment StartX=15.9241 StartY=146.444 StartZ=0 EndX=15.8843 EndY=146.255 EndZ=0
    g283: LineSegment StartX=15.8843 StartY=146.255 StartZ=0 EndX=15.8337 EndY=146.068 EndZ=0
    g284: LineSegment StartX=15.8337 StartY=146.068 StartZ=0 EndX=12.9607 EndY=136.71 EndZ=0
    g285: LineSegment StartX=12.9607 StartY=136.71 StartZ=0 EndX=12.7981 EndY=136.233 EndZ=0
    g286: LineSegment StartX=12.7981 StartY=136.233 StartZ=0 EndX=12.6062 EndY=135.767 EndZ=0
    g287: LineSegment StartX=12.6062 StartY=135.767 StartZ=0 EndX=12.3869 EndY=135.314 EndZ=0
    g288: LineSegment StartX=12.3869 StartY=135.314 StartZ=0 EndX=12.1394 EndY=134.875 EndZ=0
    g289: LineSegment StartX=12.1394 StartY=134.875 StartZ=0 EndX=11.8654 EndY=134.452 EndZ=0
    g290: LineSegment StartX=11.8654 StartY=134.452 StartZ=0 EndX=11.566 EndY=134.047 EndZ=0
    g291: LineSegment StartX=11.566 StartY=134.047 StartZ=0 EndX=11.2432 EndY=133.661 EndZ=0
    g292: LineSegment StartX=11.2432 StartY=133.661 StartZ=0 EndX=10.8969 EndY=133.296 EndZ=0
    g293: LineSegment StartX=10.8969 StartY=133.296 StartZ=0 EndX=10.5281 EndY=132.952 EndZ=0
    g294: LineSegment StartX=10.5281 StartY=132.952 StartZ=0 EndX=10.1397 EndY=132.632 EndZ=0
    g295: LineSegment StartX=10.1397 StartY=132.632 StartZ=0 EndX=9.73186 EndY=132.335 EndZ=0
    g296: LineSegment StartX=9.73186 StartY=132.335 StartZ=0 EndX=9.30636 EndY=132.065 EndZ=0
    g297: LineSegment StartX=9.30636 StartY=132.065 StartZ=0 EndX=8.86618 EndY=131.822 EndZ=0
    g298: LineSegment StartX=8.86618 StartY=131.822 StartZ=0 EndX=8.41035 EndY=131.606 EndZ=0
    g299: LineSegment StartX=8.41035 StartY=131.606 StartZ=0 EndX=5.6461 EndY=130.29 EndZ=0
    g300: LineSegment StartX=5.6461 StartY=130.29 StartZ=0 EndX=2.9709 EndY=128.804 EndZ=0
    g301: LineSegment StartX=2.9709 StartY=128.804 StartZ=0 EndX=0.392551 EndY=127.153 EndZ=0
    g302: LineSegment StartX=0.392551 StartY=127.153 StartZ=0 EndX=-2.07626 EndY=125.343 EndZ=0
    g303: LineSegment StartX=-2.07626 StartY=125.343 StartZ=0 EndX=-4.42674 EndY=123.381 EndZ=0
    g304: LineSegment StartX=-4.42674 StartY=123.381 StartZ=0 EndX=-6.64915 EndY=121.277 EndZ=0
    g305: LineSegment StartX=-6.64915 StartY=121.277 StartZ=0 EndX=-8.73567 EndY=119.037 EndZ=0
    g306: LineSegment StartX=-8.73567 StartY=119.037 StartZ=0 EndX=-10.6766 EndY=116.67 EndZ=0
    g307: LineSegment StartX=-10.6766 StartY=116.67 StartZ=0 EndX=-12.4659 EndY=114.186 EndZ=0
    g308: LineSegment StartX=-12.4659 StartY=114.186 StartZ=0 EndX=-14.096 EndY=111.595 EndZ=0
    g309: LineSegment StartX=-14.096 StartY=111.595 StartZ=0 EndX=-15.56 EndY=108.907 EndZ=0
    g310: LineSegment StartX=-15.56 StartY=108.907 StartZ=0 EndX=-16.852 EndY=106.132 EndZ=0
    g311: LineSegment StartX=-16.852 StartY=106.132 StartZ=0 EndX=-17.9672 EndY=103.281 EndZ=0
    g312: LineSegment StartX=-17.9672 StartY=103.281 StartZ=0 EndX=-18.9017 EndY=100.366 EndZ=0
    g313: LineSegment StartX=-18.9017 StartY=100.366 StartZ=0 EndX=-19.6515 EndY=97.3974 EndZ=0
    g314: LineSegment StartX=-19.6515 StartY=97.3974 StartZ=0 EndX=-20.2138 EndY=94.389 EndZ=0
    g315: LineSegment StartX=-20.2138 StartY=94.389 StartZ=0 EndX=-20.5856 EndY=91.3505 EndZ=0
    g316: LineSegment StartX=-20.5856 StartY=91.3505 StartZ=0 EndX=-20.766 EndY=88.2947 EndZ=0
    g317: LineSegment StartX=-20.766 StartY=88.2947 StartZ=0 EndX=-20.755 EndY=85.2332 EndZ=0
    g318: LineSegment StartX=-20.755 StartY=85.2332 StartZ=0 EndX=-20.5506 EndY=82.1787 EndZ=0
    g319: LineSegment StartX=-20.5506 StartY=82.1787 StartZ=0 EndX=-20.1558 EndY=79.143 EndZ=0
    g320: LineSegment StartX=11.6806 StartY=145.84 StartZ=0 EndX=11.6092 EndY=145.912 EndZ=0
    g321: LineSegment StartX=11.6092 StartY=145.912 StartZ=0 EndX=11.5428 EndY=145.987 EndZ=0
    g322: LineSegment StartX=11.5428 StartY=145.987 StartZ=0 EndX=11.4811 EndY=146.066 EndZ=0
    g323: LineSegment StartX=11.4811 StartY=146.066 StartZ=0 EndX=11.4244 EndY=146.149 EndZ=0
    g324: LineSegment StartX=11.4244 StartY=146.149 StartZ=0 EndX=11.3735 EndY=146.236 EndZ=0
    g325: LineSegment StartX=11.3735 StartY=146.236 StartZ=0 EndX=11.3276 EndY=146.325 EndZ=0
    g326: LineSegment StartX=11.3276 StartY=146.325 StartZ=0 EndX=11.2874 EndY=146.417 EndZ=0
    g327: LineSegment StartX=11.2874 StartY=146.417 StartZ=0 EndX=11.2531 EndY=146.512 EndZ=0
    g328: LineSegment StartX=11.2531 StartY=146.512 StartZ=0 EndX=11.2247 EndY=146.608 EndZ=0
    g329: LineSegment StartX=11.2247 StartY=146.608 StartZ=0 EndX=11.2031 EndY=146.706 EndZ=0
    g330: LineSegment StartX=11.2031 StartY=146.706 StartZ=0 EndX=11.1874 EndY=146.806 EndZ=0
    g331: LineSegment StartX=11.1874 StartY=146.806 StartZ=0 EndX=11.1775 EndY=146.905 EndZ=0
    g332: LineSegment StartX=11.1775 StartY=146.905 StartZ=0 EndX=11.1745 EndY=147.006 EndZ=0
    g333: LineSegment StartX=11.1745 StartY=147.006 StartZ=0 EndX=11.1773 EndY=147.106 EndZ=0
    g334: LineSegment StartX=11.1773 StartY=147.106 StartZ=0 EndX=11.187 EndY=147.207 EndZ=0
    g335: LineSegment StartX=11.187 StartY=147.207 StartZ=0 EndX=11.2025 EndY=147.306 EndZ=0
    g336: LineSegment StartX=11.2025 StartY=147.306 StartZ=0 EndX=11.2239 EndY=147.404 EndZ=0
    g337: LineSegment StartX=11.2239 StartY=147.404 StartZ=0 EndX=11.2521 EndY=147.501 EndZ=0
    g338: LineSegment StartX=11.2521 StartY=147.501 StartZ=0 EndX=11.2862 EndY=147.595 EndZ=0
    g339: LineSegment StartX=11.2862 StartY=147.595 StartZ=0 EndX=11.3261 EndY=147.688 EndZ=0
    g340: LineSegment StartX=11.3261 StartY=147.688 StartZ=0 EndX=11.3719 EndY=147.778 EndZ=0
    g341: LineSegment StartX=11.3719 StartY=147.778 StartZ=0 EndX=11.4226 EndY=147.864 EndZ=0
    g342: LineSegment StartX=11.4226 StartY=147.864 StartZ=0 EndX=11.4792 EndY=147.947 EndZ=0
    g343: LineSegment StartX=11.4792 StartY=147.947 StartZ=0 EndX=11.5406 EndY=148.027 EndZ=0
    g344: LineSegment StartX=11.5406 StartY=148.027 StartZ=0 EndX=11.6069 EndY=148.102 EndZ=0
    g345: LineSegment StartX=11.6069 StartY=148.102 StartZ=0 EndX=11.6782 EndY=148.173 EndZ=0
    g346: LineSegment StartX=11.6782 StartY=148.173 StartZ=0 EndX=11.7533 EndY=148.24 EndZ=0
    g347: LineSegment StartX=11.7533 StartY=148.24 StartZ=0 EndX=11.8323 EndY=148.302 EndZ=0
    g348: LineSegment StartX=11.8323 StartY=148.302 StartZ=0 EndX=11.9153 EndY=148.358 EndZ=0
    g349: LineSegment StartX=11.9153 StartY=148.358 StartZ=0 EndX=12.0021 EndY=148.409 EndZ=0
    g350: LineSegment StartX=12.0021 StartY=148.409 StartZ=0 EndX=12.0919 EndY=148.455 EndZ=0
    g351: LineSegment StartX=12.0919 StartY=148.455 StartZ=0 EndX=12.1837 EndY=148.495 EndZ=0
    g352: LineSegment StartX=12.1837 StartY=148.495 StartZ=0 EndX=12.2784 EndY=148.53 EndZ=0
    g353: LineSegment StartX=12.2784 StartY=148.53 StartZ=0 EndX=12.375 EndY=148.557 EndZ=0
    g354: LineSegment StartX=12.375 StartY=148.557 StartZ=0 EndX=12.4727 EndY=148.58 EndZ=0
    g355: LineSegment StartX=12.4727 StartY=148.58 StartZ=0 EndX=12.5723 EndY=148.595 EndZ=0
    g356: LineSegment StartX=12.5723 StartY=148.595 StartZ=0 EndX=12.6719 EndY=148.604 EndZ=0
    g357: LineSegment StartX=12.6719 StartY=148.604 StartZ=0 EndX=12.7724 EndY=148.608 EndZ=0
    g358: LineSegment StartX=12.7724 StartY=148.608 StartZ=0 EndX=12.873 EndY=148.604 EndZ=0
    g359: LineSegment StartX=12.873 StartY=148.604 StartZ=0 EndX=12.9736 EndY=148.596 EndZ=0
    g360: LineSegment StartX=12.9736 StartY=148.596 StartZ=0 EndX=13.0723 EndY=148.58 EndZ=0
    g361: LineSegment StartX=13.0723 StartY=148.58 StartZ=0 EndX=13.1709 EndY=148.558 EndZ=0
    g362: LineSegment StartX=13.1709 StartY=148.558 StartZ=0 EndX=13.2676 EndY=148.531 EndZ=0
    g363: LineSegment StartX=13.2676 StartY=148.531 StartZ=0 EndX=13.3614 EndY=148.496 EndZ=0
    g364: LineSegment StartX=13.3614 StartY=148.496 StartZ=0 EndX=13.4542 EndY=148.457 EndZ=0
    g365: LineSegment StartX=13.4542 StartY=148.457 StartZ=0 EndX=13.5441 EndY=148.411 EndZ=0
    g366: LineSegment StartX=13.5441 StartY=148.411 StartZ=0 EndX=13.6301 EndY=148.36 EndZ=0
    g367: LineSegment StartX=13.6301 StartY=148.36 StartZ=0 EndX=13.7132 EndY=148.303 EndZ=0
    g368: LineSegment StartX=13.7132 StartY=148.303 StartZ=0 EndX=13.7933 EndY=148.242 EndZ=0
    g369: LineSegment StartX=13.7933 StartY=148.242 StartZ=0 EndX=13.8686 EndY=148.176 EndZ=0
    g370: LineSegment StartX=13.8686 StartY=148.176 StartZ=0 EndX=13.94 EndY=148.105 EndZ=0
    g371: LineSegment StartX=13.94 StartY=148.105 StartZ=0 EndX=14.0064 EndY=148.029 EndZ=0
    g372: LineSegment StartX=14.0064 StartY=148.029 StartZ=0 EndX=14.068 EndY=147.949 EndZ=0
    g373: LineSegment StartX=14.068 StartY=147.949 StartZ=0 EndX=14.1248 EndY=147.866 EndZ=0
    g374: LineSegment StartX=14.1248 StartY=147.866 StartZ=0 EndX=14.1756 EndY=147.781 EndZ=0
    g375: LineSegment StartX=14.1756 StartY=147.781 StartZ=0 EndX=14.2216 EndY=147.691 EndZ=0
    g376: LineSegment StartX=14.2216 StartY=147.691 StartZ=0 EndX=14.2618 EndY=147.598 EndZ=0
    g377: LineSegment StartX=14.2618 StartY=147.598 StartZ=0 EndX=14.2961 EndY=147.504 EndZ=0
    g378: LineSegment StartX=14.2961 StartY=147.504 StartZ=0 EndX=14.3235 EndY=147.408 EndZ=0
    g379: LineSegment StartX=14.3235 StartY=147.408 StartZ=0 EndX=14.3461 EndY=147.309 EndZ=0
    g380: LineSegment StartX=14.3461 StartY=147.309 StartZ=0 EndX=14.3618 EndY=147.21 EndZ=0
    g381: LineSegment StartX=14.3618 StartY=147.21 StartZ=0 EndX=14.3717 EndY=147.11 EndZ=0
    g382: LineSegment StartX=14.3717 StartY=147.11 StartZ=0 EndX=14.3747 EndY=147.009 EndZ=0
    g383: LineSegment StartX=14.3747 StartY=147.009 StartZ=0 EndX=14.3719 EndY=146.909 EndZ=0
    g384: LineSegment StartX=14.3719 StartY=146.909 StartZ=0 EndX=14.3622 EndY=146.809 EndZ=0
    g385: LineSegment StartX=14.3622 StartY=146.809 StartZ=0 EndX=14.3467 EndY=146.709 EndZ=0
    g386: LineSegment StartX=14.3467 StartY=146.709 StartZ=0 EndX=14.3243 EndY=146.612 EndZ=0
    g387: LineSegment StartX=14.3243 StartY=146.612 StartZ=0 EndX=14.2971 EndY=146.515 EndZ=0
    g388: LineSegment StartX=14.2971 StartY=146.515 StartZ=0 EndX=14.263 EndY=146.42 EndZ=0
    g389: LineSegment StartX=14.263 StartY=146.42 StartZ=0 EndX=14.2231 EndY=146.328 EndZ=0
    g390: LineSegment StartX=14.2231 StartY=146.328 StartZ=0 EndX=14.1773 EndY=146.239 EndZ=0
    g391: LineSegment StartX=14.1773 StartY=146.239 StartZ=0 EndX=14.1266 EndY=146.152 EndZ=0
    g392: LineSegment StartX=14.1266 StartY=146.152 StartZ=0 EndX=14.07 EndY=146.069 EndZ=0
    g393: LineSegment StartX=14.07 StartY=146.069 StartZ=0 EndX=14.0086 EndY=145.989 EndZ=0
    g394: LineSegment StartX=14.0086 StartY=145.989 StartZ=0 EndX=13.9422 EndY=145.914 EndZ=0
    g395: LineSegment StartX=13.9422 StartY=145.914 StartZ=0 EndX=13.871 EndY=145.843 EndZ=0
    g396: LineSegment StartX=13.871 StartY=145.843 StartZ=0 EndX=13.7959 EndY=145.776 EndZ=0
    g397: LineSegment StartX=13.7959 StartY=145.776 StartZ=0 EndX=13.7159 EndY=145.715 EndZ=0
    g398: LineSegment StartX=13.7159 StartY=145.715 StartZ=0 EndX=13.6329 EndY=145.658 EndZ=0
    g399: LineSegment StartX=13.6329 StartY=145.658 StartZ=0 EndX=13.5471 EndY=145.607 EndZ=0
    ... +2316 more geometry lines
FEATURE [Sketcher::SketchObject] Sketch019  label="mainbodysketch"
  ArcFitTolerance = 1e-06
  FullyConstrained = false
  MakeInternals = false
  Placement = pos=(70.7,403.5,0) rot=(0,0,1;0rad)
  sketch-geometry (2787):
    g0: ArcOfCircle CenterX=-152.069 CenterY=-222.772 CenterZ=0 NormalX=0 NormalY=0 NormalZ=1 AngleXU=0 Radius=77.3239 StartAngle=4.75433 EndAngle=5.19077
    g1: ArcOfCircle CenterX=-280.471 CenterY=-386.318 CenterZ=0 NormalX=0 NormalY=0 NormalZ=1 AngleXU=0 Radius=17 StartAngle=3.40529 EndAngle=4.71239
    g2: LineSegment StartX=-244.178 StartY=-403.318 StartZ=0 EndX=-280.471 EndY=-403.318 EndZ=0
    g3: ArcOfCircle CenterX=-244.178 CenterY=-373.318 CenterZ=0 NormalX=0 NormalY=0 NormalZ=1 AngleXU=0 Radius=30 StartAngle=4.71239 EndAngle=5.10704
    g4: ArcOfCircle CenterX=-288.174 CenterY=-267.685 CenterZ=0 NormalX=0 NormalY=0 NormalZ=1 AngleXU=0 Radius=144.429 StartAngle=5.10704 EndAngle=5.1698
    g5: ArcOfCircle CenterX=-215.558 CenterY=-415.211 CenterZ=0 NormalX=0 NormalY=0 NormalZ=1 AngleXU=0 Radius=20 StartAngle=1.66649 EndAngle=2.0282
    g6: ArcOfCircle CenterX=-163.5 CenterY=-957.553 CenterZ=0 NormalX=0 NormalY=0 NormalZ=1 AngleXU=0 Radius=564.835 StartAngle=1.47229 EndAngle=1.66649
    g7: Circle CenterX=-163.5 CenterY=-354.5 CenterZ=0 NormalX=0 NormalY=0 NormalZ=-1 AngleXU=0 Radius=14.3449
    g8: ArcOfCircle CenterX=-46.5291 CenterY=-386.318 CenterZ=0 NormalX=0 NormalY=0 NormalZ=1 AngleXU=0 Radius=17 StartAngle=4.71239 EndAngle=6.01949
    g9: LineSegment StartX=-82.8222 StartY=-403.318 StartZ=0 EndX=-46.5291 EndY=-403.318 EndZ=0
    g10: ArcOfCircle CenterX=-46.5291 CenterY=-386.318 CenterZ=0 NormalX=0 NormalY=0 NormalZ=1 AngleXU=0 Radius=17 StartAngle=4.71239 EndAngle=6.01949
    g11: ArcOfCircle CenterX=-38.8263 CenterY=-267.685 CenterZ=0 NormalX=0 NormalY=0 NormalZ=1 AngleXU=0 Radius=144.429 StartAngle=4.25498 EndAngle=4.31774
    g12: ArcOfCircle CenterX=-82.8222 CenterY=-373.318 CenterZ=0 NormalX=0 NormalY=0 NormalZ=1 AngleXU=0 Radius=30 StartAngle=4.31774 EndAngle=4.71239
    g13: ArcOfCircle CenterX=-111.442 CenterY=-415.211 CenterZ=0 NormalX=0 NormalY=0 NormalZ=1 AngleXU=0 Radius=20 StartAngle=1.11339 EndAngle=1.4751
    g14: ArcOfCircle CenterX=-248.227 CenterY=-371.478 CenterZ=0 NormalX=0 NormalY=0 NormalZ=1 AngleXU=0 Radius=15 StartAngle=4.71239 EndAngle=6.22689
    g15: ArcOfCircle CenterX=-174.931 CenterY=-222.772 CenterZ=0 NormalX=0 NormalY=0 NormalZ=1 AngleXU=0 Radius=77.3239 StartAngle=4.23401 EndAngle=4.67045
    g16: ArcOfCircle CenterX=-78.7734 CenterY=-371.478 CenterZ=0 NormalX=0 NormalY=0 NormalZ=1 AngleXU=0 Radius=15 StartAngle=3.19789 EndAngle=4.71239
    g17: LineSegment StartX=-148.827 StartY=-300.028 StartZ=0 EndX=-178.173 EndY=-300.028 EndZ=0
    g18: LineSegment StartX=-58.6961 StartY=-386.478 StartZ=0 EndX=-78.7734 EndY=-386.478 EndZ=0
    g19: ArcOfCircle CenterX=-58.6961 CenterY=-381.478 CenterZ=0 NormalX=0 NormalY=0 NormalZ=1 AngleXU=0 Radius=5 StartAngle=4.71239 EndAngle=6.02246
    g20: Circle CenterX=-163.5 CenterY=-382.5 CenterZ=0 NormalX=0 NormalY=0 NormalZ=-1 AngleXU=0 Radius=2.5
    g21: Circle CenterX=-139.251 CenterY=-368.5 CenterZ=0 NormalX=0 NormalY=0 NormalZ=-1 AngleXU=0 Radius=2.5
    g22: Circle CenterX=-139.251 CenterY=-340.5 CenterZ=0 NormalX=0 NormalY=0 NormalZ=-1 AngleXU=0 Radius=2.5
    g23: Circle CenterX=-163.5 CenterY=-326.5 CenterZ=0 NormalX=0 NormalY=0 NormalZ=-1 AngleXU=0 Radius=2.5
    g24: Circle CenterX=-187.749 CenterY=-340.5 CenterZ=0 NormalX=0 NormalY=0 NormalZ=-1 AngleXU=0 Radius=2.5
    g25: Circle CenterX=-187.749 CenterY=-368.5 CenterZ=0 NormalX=0 NormalY=0 NormalZ=-1 AngleXU=0 Radius=2.5
    g26: LineSegment StartX=-56.0985 StartY=-267.155 StartZ=0 EndX=-53.2155 EndY=-257.799 EndZ=0
    g27: ArcOfCircle CenterX=-65.6551 CenterY=-264.21 CenterZ=0 NormalX=0 NormalY=0 NormalZ=1 AngleXU=0 Radius=10 StartAngle=5.12409 EndAngle=5.98426
    g28: ArcOfCircle CenterX=-57.9938 CenterY=-256.327 CenterZ=0 NormalX=0 NormalY=0 NormalZ=1 AngleXU=0 Radius=5 StartAngle=5.98426 EndAngle=8.10068
    g29: ArcOfCircle CenterX=-42.8649 CenterY=-316.402 CenterZ=0 NormalX=0 NormalY=0 NormalZ=1 AngleXU=0 Radius=66.9511 StartAngle=1.8175 EndAngle=3.69281
    g30: ArcOfCircle CenterX=-42.8649 CenterY=-316.402 CenterZ=0 NormalX=0 NormalY=0 NormalZ=1 AngleXU=0 Radius=68.9511 StartAngle=1.8031 EndAngle=2.51892
    g31: ArcOfCircle CenterX=-193.147 CenterY=-345.607 CenterZ=0 NormalX=0 NormalY=0 NormalZ=1 AngleXU=0 Radius=169.165 StartAngle=6.01194 EndAngle=6.87087
    g32: ArcOfCircle CenterX=-193.147 CenterY=-345.607 CenterZ=0 NormalX=0 NormalY=0 NormalZ=1 AngleXU=0 Radius=144.165 StartAngle=6.02246 EndAngle=6.87647
    g33: ArcOfCircle CenterX=-42.8649 CenterY=-316.402 CenterZ=0 NormalX=0 NormalY=0 NormalZ=1 AngleXU=0 Radius=46.9511 StartAngle=1.9825 EndAngle=3.61535
    g34: ArcOfCircle CenterX=-95.6403 CenterY=-348.847 CenterZ=0 NormalX=0 NormalY=0 NormalZ=1 AngleXU=0 Radius=5 StartAngle=3.69281 EndAngle=5.64052
    g35: LineSegment StartX=-85.0916 StartY=-343.1 StartZ=0 EndX=-91.6378 EndY=-351.844 EndZ=0
    g36: ArcOfCircle CenterX=-89.0941 CenterY=-340.104 CenterZ=0 NormalX=0 NormalY=0 NormalZ=1 AngleXU=0 Radius=5 StartAngle=5.64052 EndAngle=6.75694
    g37: ArcOfCircle CenterX=-60.2975 CenterY=-368.87 CenterZ=0 NormalX=0 NormalY=0 NormalZ=1 AngleXU=0 Radius=33.6298 StartAngle=2.9338 EndAngle=3.24442
    g38: LineSegment StartX=-48.5854 StartY=-313.24 StartZ=0 EndX=-88.8881 EndY=-325.69 EndZ=0
    g39: LineSegment StartX=-48.175 StartY=-332.212 StartZ=0 EndX=-74.392 EndY=-338.131 EndZ=0
    g40: LineSegment StartX=-83.0964 StartY=-343.773 StartZ=0 EndX=-87.8643 EndY=-350.141 EndZ=0
    g41: LineSegment StartX=-57.0129 StartY=-247.712 StartZ=0 EndX=-33.4816 EndY=-247.712 EndZ=0
    g42: LineSegment StartX=-36.7568 StartY=-261.917 StartZ=0 EndX=-40.5225 EndY=-242.051 EndZ=0
    g43: LineSegment StartX=-36.7568 StartY=-261.917 StartZ=0 EndX=-36.7568 EndY=-284.959 EndZ=0
    g44: ArcOfCircle CenterX=-284.135 CenterY=-316.402 CenterZ=0 NormalX=0 NormalY=0 NormalZ=1 AngleXU=0 Radius=66.9511 StartAngle=5.73197 EndAngle=7.60728
    g45: ArcOfCircle CenterX=-284.135 CenterY=-316.402 CenterZ=0 NormalX=0 NormalY=0 NormalZ=1 AngleXU=0 Radius=46.9511 StartAngle=5.80943 EndAngle=7.44228
    g46: LineSegment StartX=-241.908 StartY=-343.1 StartZ=0 EndX=-235.362 EndY=-351.844 EndZ=0
    g47: ArcOfCircle CenterX=-237.906 CenterY=-340.104 CenterZ=0 NormalX=0 NormalY=0 NormalZ=1 AngleXU=0 Radius=5 StartAngle=2.66784 EndAngle=3.78426
    g48: ArcOfCircle CenterX=-231.36 CenterY=-348.847 CenterZ=0 NormalX=0 NormalY=0 NormalZ=1 AngleXU=0 Radius=5 StartAngle=3.78426 EndAngle=5.73197
    g49: Circle CenterX=-231.444 CenterY=-338.014 CenterZ=0 NormalX=0 NormalY=0 NormalZ=-1 AngleXU=0 Radius=5
    g50: Circle CenterX=-227.384 CenterY=-321.17 CenterZ=0 NormalX=0 NormalY=0 NormalZ=-1 AngleXU=0 Radius=5
    g51: Circle CenterX=-228.577 CenterY=-303.884 CenterZ=0 NormalX=0 NormalY=0 NormalZ=-1 AngleXU=0 Radius=5
    g52: Circle CenterX=-234.913 CenterY=-287.756 CenterZ=0 NormalX=0 NormalY=0 NormalZ=-1 AngleXU=0 Radius=5
    g53: Circle CenterX=-245.805 CenterY=-274.281 CenterZ=0 NormalX=0 NormalY=0 NormalZ=-1 AngleXU=0 Radius=5
    g54: Circle CenterX=-260.245 CenterY=-264.704 CenterZ=0 NormalX=0 NormalY=0 NormalZ=-1 AngleXU=0 Radius=5
    g55: LineSegment StartX=-270.901 StartY=-267.155 StartZ=0 EndX=-273.784 EndY=-257.799 EndZ=0
    g56: ArcOfCircle CenterX=-269.006 CenterY=-256.327 CenterZ=0 NormalX=0 NormalY=0 NormalZ=1 AngleXU=0 Radius=5 StartAngle=1.32409 EndAngle=3.44052
    g57: ArcOfCircle CenterX=-261.345 CenterY=-264.21 CenterZ=0 NormalX=0 NormalY=0 NormalZ=1 AngleXU=0 Radius=10 StartAngle=3.44052 EndAngle=4.30068
    g58: ArcOfCircle CenterX=-284.135 CenterY=-316.402 CenterZ=0 NormalX=0 NormalY=0 NormalZ=1 AngleXU=0 Radius=68.9511 StartAngle=0.622676 EndAngle=1.3385
    g59: ArcOfCircle CenterX=-284.135 CenterY=-316.402 CenterZ=0 NormalX=0 NormalY=0 NormalZ=1 AngleXU=0 Radius=66.9511 StartAngle=5.73197 EndAngle=7.60728
    g60: LineSegment StartX=-269.987 StartY=-247.712 StartZ=0 EndX=-293.518 EndY=-247.712 EndZ=0
    g61: ArcOfCircle CenterX=-133.853 CenterY=-345.607 CenterZ=0 NormalX=0 NormalY=0 NormalZ=1 AngleXU=0 Radius=169.165 StartAngle=2.5539 EndAngle=3.41284
    g62: ArcOfCircle CenterX=-133.853 CenterY=-345.607 CenterZ=0 NormalX=0 NormalY=0 NormalZ=1 AngleXU=0 Radius=144.165 StartAngle=2.5483 EndAngle=3.40231
    g63: LineSegment StartX=-278.415 StartY=-313.24 StartZ=0 EndX=-238.112 EndY=-325.69 EndZ=0
    g64: LineSegment StartX=-278.825 StartY=-332.212 StartZ=0 EndX=-252.608 EndY=-338.131 EndZ=0
    g65: LineSegment StartX=-243.904 StartY=-343.773 StartZ=0 EndX=-239.136 EndY=-350.141 EndZ=0
    g66: ArcOfCircle CenterX=-266.703 CenterY=-368.87 CenterZ=0 NormalX=0 NormalY=0 NormalZ=1 AngleXU=0 Radius=33.6298 StartAngle=6.18035 EndAngle=6.49098
    g67: LineSegment StartX=-268.304 StartY=-386.478 StartZ=0 EndX=-248.227 EndY=-386.478 EndZ=0
    g68: ArcOfCircle CenterX=-268.304 CenterY=-381.478 CenterZ=0 NormalX=0 NormalY=0 NormalZ=1 AngleXU=0 Radius=5 StartAngle=3.40231 EndAngle=4.71239
    g69: LineSegment StartX=-290.243 StartY=-261.917 StartZ=0 EndX=-286.478 EndY=-242.051 EndZ=0
    g70: LineSegment StartX=-290.243 StartY=-261.917 StartZ=0 EndX=-290.243 EndY=-284.959 EndZ=0
    g71: LineSegment StartX=-18.9552 StartY=85.2966 StartZ=0 EndX=-18.9671 EndY=88.2448 EndZ=0
    g72: LineSegment StartX=-18.9671 StartY=88.2448 StartZ=0 EndX=-18.7934 EndY=91.1874 EndZ=0
    g73: LineSegment StartX=-18.7934 StartY=91.1874 StartZ=0 EndX=-18.4352 EndY=94.1135 EndZ=0
    g74: LineSegment StartX=-18.4352 StartY=94.1135 StartZ=0 EndX=-17.8933 EndY=97.0116 EndZ=0
    g75: LineSegment StartX=-17.8933 StartY=97.0116 StartZ=0 EndX=-17.1717 EndY=99.8707 EndZ=0
    g76: LineSegment StartX=-17.1717 StartY=99.8707 StartZ=0 EndX=-16.2713 EndY=102.677 EndZ=0
    g77: LineSegment StartX=-16.2713 StartY=102.677 StartZ=0 EndX=-15.197 EndY=105.424 EndZ=0
    g78: LineSegment StartX=-15.197 StartY=105.424 StartZ=0 EndX=-13.9527 EndY=108.096 EndZ=0
    g79: LineSegment StartX=-13.9527 StartY=108.096 StartZ=0 EndX=-12.5424 EndY=110.685 EndZ=0
    g80: LineSegment StartX=-12.5424 StartY=110.685 StartZ=0 EndX=-10.9727 EndY=113.18 EndZ=0
    g81: LineSegment StartX=-10.9727 StartY=113.18 StartZ=0 EndX=-9.24962 EndY=115.572 EndZ=0
    g82: LineSegment StartX=-9.24962 StartY=115.572 StartZ=0 EndX=-7.37994 EndY=117.852 EndZ=0
    g83: LineSegment StartX=-7.37994 StartY=117.852 StartZ=0 EndX=-5.37146 EndY=120.009 EndZ=0
    g84: LineSegment StartX=-5.37146 StartY=120.009 StartZ=0 EndX=-3.23002 EndY=122.037 EndZ=0
    g85: LineSegment StartX=-3.23002 StartY=122.037 StartZ=0 EndX=-0.966374 EndY=123.925 EndZ=0
    g86: LineSegment StartX=-0.966374 StartY=123.925 StartZ=0 EndX=1.41071 EndY=125.669 EndZ=0
    g87: LineSegment StartX=1.41071 StartY=125.669 StartZ=0 EndX=3.89342 EndY=127.258 EndZ=0
    g88: LineSegment StartX=3.89342 StartY=127.258 StartZ=0 EndX=6.47102 EndY=128.689 EndZ=0
    g89: LineSegment StartX=6.47102 StartY=128.689 StartZ=0 EndX=9.13278 EndY=129.957 EndZ=0
    g90: LineSegment StartX=9.13278 StartY=129.957 StartZ=0 EndX=9.6872 EndY=130.22 EndZ=0
    g91: LineSegment StartX=9.6872 StartY=130.22 StartZ=0 EndX=10.225 EndY=130.518 EndZ=0
    g92: LineSegment StartX=10.225 StartY=130.518 StartZ=0 EndX=10.7442 EndY=130.847 EndZ=0
    g93: LineSegment StartX=10.7442 StartY=130.847 StartZ=0 EndX=11.2408 EndY=131.208 EndZ=0
    g94: LineSegment StartX=11.2408 StartY=131.208 StartZ=0 EndX=11.7151 EndY=131.598 EndZ=0
    g95: LineSegment StartX=11.7151 StartY=131.598 StartZ=0 EndX=12.1638 EndY=132.018 EndZ=0
    g96: LineSegment StartX=12.1638 StartY=132.018 StartZ=0 EndX=12.5872 EndY=132.463 EndZ=0
    g97: LineSegment StartX=12.5872 StartY=132.463 StartZ=0 EndX=12.9812 EndY=132.935 EndZ=0
    g98: LineSegment StartX=12.9812 StartY=132.935 StartZ=0 EndX=13.3459 EndY=133.428 EndZ=0
    g99: LineSegment StartX=13.3459 StartY=133.428 StartZ=0 EndX=13.6794 EndY=133.944 EndZ=0
    g100: LineSegment StartX=13.6794 StartY=133.944 StartZ=0 EndX=13.9816 EndY=134.48 EndZ=0
    g101: LineSegment StartX=13.9816 StartY=134.48 StartZ=0 EndX=14.2495 EndY=135.033 EndZ=0
    g102: LineSegment StartX=14.2495 StartY=135.033 StartZ=0 EndX=14.4823 EndY=135.6 EndZ=0
    g103: LineSegment StartX=14.4823 StartY=135.6 StartZ=0 EndX=14.681 EndY=136.181 EndZ=0
    g104: LineSegment StartX=14.681 StartY=136.181 StartZ=0 EndX=17.554 EndY=145.541 EndZ=0
    g105: LineSegment StartX=17.554 StartY=145.541 StartZ=0 EndX=17.6337 EndY=145.832 EndZ=0
    g106: LineSegment StartX=17.6337 StartY=145.832 StartZ=0 EndX=17.6959 EndY=146.128 EndZ=0
    g107: LineSegment StartX=17.6959 StartY=146.128 StartZ=0 EndX=17.7405 EndY=146.427 EndZ=0
    g108: LineSegment StartX=17.7405 StartY=146.427 StartZ=0 EndX=17.7666 EndY=146.728 EndZ=0
    g109: LineSegment StartX=17.7666 StartY=146.728 StartZ=0 EndX=17.7741 EndY=147.029 EndZ=0
    g110: LineSegment StartX=17.7741 StartY=147.029 StartZ=0 EndX=17.764 EndY=147.331 EndZ=0
    g111: LineSegment StartX=17.764 StartY=147.331 StartZ=0 EndX=17.7354 EndY=147.632 EndZ=0
    g112: LineSegment StartX=17.7354 StartY=147.632 StartZ=0 EndX=17.6882 EndY=147.931 EndZ=0
    g113: LineSegment StartX=17.6882 StartY=147.931 StartZ=0 EndX=17.6234 EndY=148.226 EndZ=0
    g114: LineSegment StartX=17.6234 StartY=148.226 StartZ=0 EndX=17.5411 EndY=148.516 EndZ=0
    g115: LineSegment StartX=17.5411 StartY=148.516 StartZ=0 EndX=17.4412 EndY=148.802 EndZ=0
    g116: LineSegment StartX=17.4412 StartY=148.802 StartZ=0 EndX=17.3247 EndY=149.081 EndZ=0
    g117: LineSegment StartX=17.3247 StartY=149.081 StartZ=0 EndX=17.1916 EndY=149.352 EndZ=0
    g118: LineSegment StartX=17.1916 StartY=149.352 StartZ=0 EndX=17.0419 EndY=149.615 EndZ=0
    g119: LineSegment StartX=17.0419 StartY=149.615 StartZ=0 EndX=16.8766 EndY=149.867 EndZ=0
    g120: LineSegment StartX=16.8766 StartY=149.867 StartZ=0 EndX=16.6957 EndY=150.109 EndZ=0
    g121: LineSegment StartX=16.6957 StartY=150.109 StartZ=0 EndX=16.5011 EndY=150.341 EndZ=0
    g122: LineSegment StartX=16.5011 StartY=150.341 StartZ=0 EndX=16.2938 EndY=150.56 EndZ=0
    g123: LineSegment StartX=16.2938 StartY=150.56 StartZ=0 EndX=16.0719 EndY=150.766 EndZ=0
    g124: LineSegment StartX=16.0719 StartY=150.766 StartZ=0 EndX=15.8393 EndY=150.958 EndZ=0
    g125: LineSegment StartX=15.8393 StartY=150.958 StartZ=0 EndX=15.595 EndY=151.137 EndZ=0
    g126: LineSegment StartX=15.595 StartY=151.137 StartZ=0 EndX=15.3409 EndY=151.299 EndZ=0
    g127: LineSegment StartX=15.3409 StartY=151.299 StartZ=0 EndX=15.0771 EndY=151.447 EndZ=0
    g128: LineSegment StartX=15.0771 StartY=151.447 StartZ=0 EndX=14.8045 EndY=151.577 EndZ=0
    g129: LineSegment StartX=14.8045 StartY=151.577 StartZ=0 EndX=14.5251 EndY=151.692 EndZ=0
    g130: LineSegment StartX=14.5251 StartY=151.692 StartZ=0 EndX=0.64951 EndY=156.877 EndZ=0
    g131: LineSegment StartX=0.64951 StartY=156.877 StartZ=0 EndX=0.0887629 EndY=157.068 EndZ=0
    g132: LineSegment StartX=0.0887629 StartY=157.068 StartZ=0 EndX=-0.481714 EndY=157.224 EndZ=0
    g133: LineSegment StartX=-0.481714 StartY=157.224 StartZ=0 EndX=-1.05997 EndY=157.348 EndZ=0
    g134: LineSegment StartX=-1.05997 StartY=157.348 StartZ=0 EndX=-1.64502 EndY=157.436 EndZ=0
    g135: LineSegment StartX=-1.64502 StartY=157.436 StartZ=0 EndX=-2.23395 EndY=157.49 EndZ=0
    g136: LineSegment StartX=-2.23395 StartY=157.49 StartZ=0 EndX=-2.82479 EndY=157.509 EndZ=0
    g137: LineSegment StartX=-2.82479 StartY=157.509 StartZ=0 EndX=-3.41657 EndY=157.494 EndZ=0
    g138: LineSegment StartX=-3.41657 StartY=157.494 StartZ=0 EndX=-4.00636 EndY=157.442 EndZ=0
    g139: LineSegment StartX=-4.00636 StartY=157.442 StartZ=0 EndX=-4.59123 EndY=157.357 EndZ=0
    g140: LineSegment StartX=-4.59123 StartY=157.357 StartZ=0 EndX=-5.17021 EndY=157.237 EndZ=0
    g141: LineSegment StartX=-5.17021 StartY=157.237 StartZ=0 EndX=-5.74133 EndY=157.083 EndZ=0
    g142: LineSegment StartX=-5.74133 StartY=157.083 StartZ=0 EndX=-6.30266 EndY=156.895 EndZ=0
    g143: LineSegment StartX=-6.30266 StartY=156.895 StartZ=0 EndX=-6.85126 EndY=156.675 EndZ=0
    g144: LineSegment StartX=-6.85126 StartY=156.675 StartZ=0 EndX=-7.38615 EndY=156.422 EndZ=0
    g145: LineSegment StartX=-7.38615 StartY=156.422 StartZ=0 EndX=-11.6513 EndY=154.082 EndZ=0
    g146: LineSegment StartX=-11.6513 StartY=154.082 StartZ=0 EndX=-15.7618 EndY=151.48 EndZ=0
    g147: LineSegment StartX=-15.7618 StartY=151.48 StartZ=0 EndX=-19.7012 EndY=148.626 EndZ=0
    g148: LineSegment StartX=-19.7012 StartY=148.626 StartZ=0 EndX=-23.4558 EndY=145.532 EndZ=0
    g149: LineSegment StartX=-23.4558 StartY=145.532 StartZ=0 EndX=-27.01 EndY=142.211 EndZ=0
    g150: LineSegment StartX=-27.01 StartY=142.211 StartZ=0 EndX=-30.35 EndY=138.674 EndZ=0
    g151: LineSegment StartX=-30.35 StartY=138.674 StartZ=0 EndX=-33.4633 EndY=134.936 EndZ=0
    g152: LineSegment StartX=-33.4633 StartY=134.936 StartZ=0 EndX=-36.3371 EndY=131.011 EndZ=0
    g153: LineSegment StartX=-36.3371 StartY=131.011 StartZ=0 EndX=-38.9598 EndY=126.914 EndZ=0
    g154: LineSegment StartX=-38.9598 StartY=126.914 StartZ=0 EndX=-41.3225 EndY=122.662 EndZ=0
    g155: LineSegment StartX=-41.3225 StartY=122.662 StartZ=0 EndX=-43.4156 EndY=118.27 EndZ=0
    g156: LineSegment StartX=-43.4156 StartY=118.27 StartZ=0 EndX=-45.2302 EndY=113.756 EndZ=0
    g157: LineSegment StartX=-45.2302 StartY=113.756 StartZ=0 EndX=-46.7595 EndY=109.139 EndZ=0
    g158: LineSegment StartX=-46.7595 StartY=109.139 StartZ=0 EndX=-47.9987 EndY=104.434 EndZ=0
    g159: LineSegment StartX=-47.9987 StartY=104.434 StartZ=0 EndX=-48.941 EndY=99.6617 EndZ=0
    g160: LineSegment StartX=-48.941 StartY=99.6617 StartZ=0 EndX=-49.5844 EndY=94.8397 EndZ=0
    g161: LineSegment StartX=-49.5844 StartY=94.8397 StartZ=0 EndX=-49.926 EndY=89.9868 EndZ=0
    g162: LineSegment StartX=-49.926 StartY=89.9868 StartZ=0 EndX=-49.9629 EndY=85.1225 EndZ=0
    g163: LineSegment StartX=-49.9629 StartY=85.1225 StartZ=0 EndX=-49.698 EndY=80.2654 EndZ=0
    g164: LineSegment StartX=-49.698 StartY=80.2654 StartZ=0 EndX=-49.1295 EndY=75.4339 EndZ=0
    g165: LineSegment StartX=-49.1295 StartY=75.4339 StartZ=0 EndX=-48.2612 EndY=70.6477 EndZ=0
    g166: LineSegment StartX=-48.2612 StartY=70.6477 StartZ=0 EndX=-47.0961 EndY=65.9243 EndZ=0
    g167: LineSegment StartX=-47.0961 StartY=65.9243 StartZ=0 EndX=-45.6381 EndY=61.2833 EndZ=0
    g168: LineSegment StartX=-45.6381 StartY=61.2833 StartZ=0 EndX=-43.8941 EndY=56.7421 EndZ=0
    g169: LineSegment StartX=-43.8941 StartY=56.7421 StartZ=0 EndX=-43.6347 EndY=56.175 EndZ=0
    g170: LineSegment StartX=-43.6347 StartY=56.175 StartZ=0 EndX=-43.3412 EndY=55.6255 EndZ=0
    g171: LineSegment StartX=-43.3412 StartY=55.6255 StartZ=0 EndX=-43.0125 EndY=55.0956 EndZ=0
    g172: LineSegment StartX=-43.0125 StartY=55.0956 StartZ=0 EndX=-42.6526 EndY=54.5872 EndZ=0
    g173: LineSegment StartX=-42.6526 StartY=54.5872 StartZ=0 EndX=-42.2614 EndY=54.1013 EndZ=0
    g174: LineSegment StartX=-42.2614 StartY=54.1013 StartZ=0 EndX=-41.841 EndY=53.6417 EndZ=0
    g175: LineSegment StartX=-41.841 StartY=53.6417 StartZ=0 EndX=-41.3923 EndY=53.2086 EndZ=0
    g176: LineSegment StartX=-41.3923 StartY=53.2086 StartZ=0 EndX=-40.9183 EndY=52.8048 EndZ=0
    g177: LineSegment StartX=-40.9183 StartY=52.8048 StartZ=0 EndX=-40.4189 EndY=52.4313 EndZ=0
    g178: LineSegment StartX=-40.4189 StartY=52.4313 StartZ=0 EndX=-39.898 EndY=52.0891 EndZ=0
    g179: LineSegment StartX=-39.898 StartY=52.0891 StartZ=0 EndX=-39.3567 EndY=51.7801 EndZ=0
    g180: LineSegment StartX=-39.3567 StartY=51.7801 StartZ=0 EndX=-38.7968 EndY=51.5053 EndZ=0
    g181: LineSegment StartX=-38.7968 StartY=51.5053 StartZ=0 EndX=-38.2214 EndY=51.2666 EndZ=0
    g182: LineSegment StartX=-38.2214 StartY=51.2666 StartZ=0 EndX=-37.6323 EndY=51.0641 EndZ=0
    g183: LineSegment StartX=-37.6323 StartY=51.0641 StartZ=0 EndX=-37.0315 EndY=50.8987 EndZ=0
    g184: LineSegment StartX=-37.0315 StartY=50.8987 StartZ=0 EndX=-36.421 EndY=50.7705 EndZ=0
    g185: LineSegment StartX=-36.421 StartY=50.7705 StartZ=0 EndX=-35.8047 EndY=50.6813 EndZ=0
    g186: LineSegment StartX=-35.8047 StartY=50.6813 StartZ=0 EndX=-25.3386 EndY=49.492 EndZ=0
    g187: LineSegment StartX=-25.3386 StartY=49.492 StartZ=0 EndX=-25.3396 EndY=49.4803 EndZ=0
    g188: LineSegment StartX=-25.3396 StartY=49.4803 StartZ=0 EndX=-25.0339 EndY=49.4552 EndZ=0
    g189: LineSegment StartX=-25.0339 StartY=49.4552 StartZ=0 EndX=-24.7273 EndY=49.4487 EndZ=0
    g190: LineSegment StartX=-24.7273 StartY=49.4487 StartZ=0 EndX=-24.4216 EndY=49.4608 EndZ=0
    g191: LineSegment StartX=-24.4216 StartY=49.4608 StartZ=0 EndX=-24.117 EndY=49.4914 EndZ=0
    g192: LineSegment StartX=-24.117 StartY=49.4914 StartZ=0 EndX=-23.8143 EndY=49.5415 EndZ=0
    g193: LineSegment StartX=-23.8143 StartY=49.5415 StartZ=0 EndX=-23.5155 EndY=49.6092 EndZ=0
    g194: LineSegment StartX=-23.5155 StartY=49.6092 StartZ=0 EndX=-23.2207 EndY=49.6954 EndZ=0
    g195: LineSegment StartX=-23.2207 StartY=49.6954 StartZ=0 EndX=-22.9327 EndY=49.8002 EndZ=0
    g196: LineSegment StartX=-22.9327 StartY=49.8002 StartZ=0 EndX=-22.6516 EndY=49.9216 EndZ=0
    g197: LineSegment StartX=-22.6516 StartY=49.9216 StartZ=0 EndX=-22.3783 EndY=50.0606 EndZ=0
    g198: LineSegment StartX=-22.3783 StartY=50.0606 StartZ=0 EndX=-22.1138 EndY=50.2151 EndZ=0
    g199: LineSegment StartX=-22.1138 StartY=50.2151 StartZ=0 EndX=-21.8591 EndY=50.3863 EndZ=0
    g200: LineSegment StartX=-21.8591 StartY=50.3863 StartZ=0 EndX=-21.6161 EndY=50.5731 EndZ=0
    g201: LineSegment StartX=-21.6161 StartY=50.5731 StartZ=0 EndX=-21.3849 EndY=50.7735 EndZ=0
    g202: LineSegment StartX=-21.3849 StartY=50.7735 StartZ=0 EndX=-21.1654 EndY=50.9886 EndZ=0
    g203: LineSegment StartX=-21.1654 StartY=50.9886 StartZ=0 EndX=-20.9606 EndY=51.2154 EndZ=0
    g204: LineSegment StartX=-20.9606 StartY=51.2154 StartZ=0 EndX=-20.7694 EndY=51.4558 EndZ=0
    g205: LineSegment StartX=-20.7694 StartY=51.4558 StartZ=0 EndX=-14.2327 EndY=60.2058 EndZ=0
    g206: LineSegment StartX=-14.2327 StartY=60.2058 StartZ=0 EndX=-14.0552 EndY=60.4599 EndZ=0
    g207: LineSegment StartX=-14.0552 StartY=60.4599 StartZ=0 EndX=-13.8934 EndY=60.7247 EndZ=0
    g208: LineSegment StartX=-13.8934 StartY=60.7247 StartZ=0 EndX=-13.7481 EndY=60.9983 EndZ=0
    g209: LineSegment StartX=-13.7481 StartY=60.9983 StartZ=0 EndX=-13.6205 EndY=61.2816 EndZ=0
    g210: LineSegment StartX=-13.6205 StartY=61.2816 StartZ=0 EndX=-13.5105 EndY=61.5708 EndZ=0
    g211: LineSegment StartX=-13.5105 StartY=61.5708 StartZ=0 EndX=-13.419 EndY=61.8668 EndZ=0
    g212: LineSegment StartX=-13.419 StartY=61.8668 StartZ=0 EndX=-13.3451 EndY=62.1687 EndZ=0
    g213: LineSegment StartX=-13.3451 StartY=62.1687 StartZ=0 EndX=-13.2907 EndY=62.4734 EndZ=0
    g214: LineSegment StartX=-13.2907 StartY=62.4734 StartZ=0 EndX=-13.2559 EndY=62.782 EndZ=0
    g215: LineSegment StartX=-13.2559 StartY=62.782 StartZ=0 EndX=-13.2396 EndY=63.0916 EndZ=0
    g216: LineSegment StartX=-13.2396 StartY=63.0916 StartZ=0 EndX=-13.2419 EndY=63.4012 EndZ=0
    g217: LineSegment StartX=-13.2419 StartY=63.4012 StartZ=0 EndX=-13.2647 EndY=63.7107 EndZ=0
    g218: LineSegment StartX=-13.2647 StartY=63.7107 StartZ=0 EndX=-13.306 EndY=64.0183 EndZ=0
    g219: LineSegment StartX=-13.306 StartY=64.0183 StartZ=0 EndX=-13.3659 EndY=64.322 EndZ=0
    g220: LineSegment StartX=-13.3659 StartY=64.322 StartZ=0 EndX=-13.4453 EndY=64.6217 EndZ=0
    g221: LineSegment StartX=-13.4453 StartY=64.6217 StartZ=0 EndX=-13.5423 EndY=64.9165 EndZ=0
    g222: LineSegment StartX=-13.5423 StartY=64.9165 StartZ=0 EndX=-13.6578 EndY=65.2045 EndZ=0
    g223: LineSegment StartX=-13.6578 StartY=65.2045 StartZ=0 EndX=-13.7909 EndY=65.4846 EndZ=0
    g224: LineSegment StartX=-13.7909 StartY=65.4846 StartZ=0 EndX=-15.0564 EndY=68.1473 EndZ=0
    g225: LineSegment StartX=-15.0564 StartY=68.1473 StartZ=0 EndX=-16.1511 EndY=70.8845 EndZ=0
    g226: LineSegment StartX=-16.1511 StartY=70.8845 StartZ=0 EndX=-17.072 EndY=73.6853 EndZ=0
    g227: LineSegment StartX=-17.072 StartY=73.6853 StartZ=0 EndX=-17.8162 EndY=76.538 EndZ=0
    g228: LineSegment StartX=-17.8162 StartY=76.538 StartZ=0 EndX=-18.3788 EndY=79.4319 EndZ=0
    g229: LineSegment StartX=-18.3788 StartY=79.4319 StartZ=0 EndX=-18.7598 EndY=82.3554 EndZ=0
    g230: LineSegment StartX=-18.7598 StartY=82.3554 StartZ=0 EndX=-18.9552 EndY=85.2966 EndZ=0
    g231: LineSegment StartX=-20.1558 StartY=79.143 StartZ=0 EndX=-19.5716 EndY=76.1387 EndZ=0
    g232: LineSegment StartX=-19.5716 StartY=76.1387 StartZ=0 EndX=-18.799 EndY=73.1766 EndZ=0
    g233: LineSegment StartX=-18.799 StartY=73.1766 StartZ=0 EndX=-17.8428 EndY=70.2684 EndZ=0
    g234: LineSegment StartX=-17.8428 StartY=70.2684 StartZ=0 EndX=-16.7051 EndY=67.4269 EndZ=0
    g235: LineSegment StartX=-16.7051 StartY=67.4269 StartZ=0 EndX=-15.3916 EndY=64.6616 EndZ=0
    g236: LineSegment StartX=-15.3916 StartY=64.6616 StartZ=0 EndX=-15.3065 EndY=64.482 EndZ=0
    g237: LineSegment StartX=-15.3065 StartY=64.482 StartZ=0 EndX=-15.233 EndY=64.2975 EndZ=0
    g238: LineSegment StartX=-15.233 StartY=64.2975 StartZ=0 EndX=-15.1703 EndY=64.1091 EndZ=0
    g239: LineSegment StartX=-15.1703 StartY=64.1091 StartZ=0 EndX=-15.1203 EndY=63.9178 EndZ=0
    g240: LineSegment StartX=-15.1203 StartY=63.9178 StartZ=0 EndX=-15.0811 EndY=63.7235 EndZ=0
    g241: LineSegment StartX=-15.0811 StartY=63.7235 StartZ=0 EndX=-15.0545 EndY=63.5262 EndZ=0
    g242: LineSegment StartX=-15.0545 StartY=63.5262 StartZ=0 EndX=-15.0406 EndY=63.328 EndZ=0
    g243: LineSegment StartX=-15.0406 StartY=63.328 StartZ=0 EndX=-15.0385 EndY=63.1298 EndZ=0
    g244: LineSegment StartX=-15.0385 StartY=63.1298 StartZ=0 EndX=-15.049 EndY=62.9315 EndZ=0
    g245: LineSegment StartX=-15.049 StartY=62.9315 StartZ=0 EndX=-15.0722 EndY=62.7342 EndZ=0
    g246: LineSegment StartX=-15.0722 StartY=62.7342 StartZ=0 EndX=-15.1072 EndY=62.5389 EndZ=0
    g247: LineSegment StartX=-15.1072 StartY=62.5389 StartZ=0 EndX=-15.1539 EndY=62.3464 EndZ=0
    g248: LineSegment StartX=-15.1539 StartY=62.3464 StartZ=0 EndX=-15.2122 EndY=62.1569 EndZ=0
    g249: LineSegment StartX=-15.2122 StartY=62.1569 StartZ=0 EndX=-15.2824 EndY=61.9713 EndZ=0
    g250: LineSegment StartX=-15.2824 StartY=61.9713 StartZ=0 EndX=-15.3642 EndY=61.7906 EndZ=0
    g251: LineSegment StartX=-15.3642 StartY=61.7906 StartZ=0 EndX=-15.4568 EndY=61.6147 EndZ=0
    g252: LineSegment StartX=-15.4568 StartY=61.6147 StartZ=0 EndX=-15.5611 EndY=61.4456 EndZ=0
    g253: LineSegment StartX=-15.5611 StartY=61.4456 StartZ=0 EndX=-15.6742 EndY=61.2834 EndZ=0
    g254: LineSegment StartX=-15.6742 StartY=61.2834 StartZ=0 EndX=-22.2119 EndY=52.5334 EndZ=0
    g255: LineSegment StartX=-22.2119 StartY=52.5334 StartZ=0 EndX=-22.3338 EndY=52.379 EndZ=0
    g256: LineSegment StartX=-22.3338 StartY=52.379 StartZ=0 EndX=-22.4655 EndY=52.2333 EndZ=0
    g257: LineSegment StartX=-22.4655 StartY=52.2333 StartZ=0 EndX=-22.605 EndY=52.0965 EndZ=0
    g258: LineSegment StartX=-22.605 StartY=52.0965 StartZ=0 EndX=-22.7533 EndY=51.9674 EndZ=0
    g259: LineSegment StartX=-22.7533 StartY=51.9674 StartZ=0 EndX=-22.9095 EndY=51.8481 EndZ=0
    g260: LineSegment StartX=-22.9095 StartY=51.8481 StartZ=0 EndX=-23.0715 EndY=51.7395 EndZ=0
    g261: LineSegment StartX=-23.0715 StartY=51.7395 StartZ=0 EndX=-23.2413 EndY=51.6397 EndZ=0
    g262: LineSegment StartX=-23.2413 StartY=51.6397 StartZ=0 EndX=-23.416 EndY=51.5507 EndZ=0
    g263: LineSegment StartX=-23.416 StartY=51.5507 StartZ=0 EndX=-23.5956 EndY=51.4733 EndZ=0
    g264: LineSegment StartX=-23.5956 StartY=51.4733 StartZ=0 EndX=-23.7801 EndY=51.4067 EndZ=0
    g265: LineSegment StartX=-23.7801 StartY=51.4067 StartZ=0 EndX=-23.9685 EndY=51.3509 EndZ=0
    g266: LineSegment StartX=-23.9685 StartY=51.3509 StartZ=0 EndX=-24.1599 EndY=51.3077 EndZ=0
    g267: LineSegment StartX=-24.1599 StartY=51.3077 StartZ=0 EndX=-24.3532 EndY=51.2763 EndZ=0
    g268: LineSegment StartX=-24.3532 StartY=51.2763 StartZ=0 EndX=-24.5485 EndY=51.2565 EndZ=0
    g269: LineSegment StartX=-24.5485 StartY=51.2565 StartZ=0 EndX=-24.7448 EndY=51.2485 EndZ=0
    g270: LineSegment StartX=-24.7448 StartY=51.2485 StartZ=0 EndX=-24.9411 EndY=51.2522 EndZ=0
    g271: LineSegment StartX=-24.9411 StartY=51.2522 StartZ=0 EndX=-25.1364 EndY=51.2686 EndZ=0
    g272: LineSegment StartX=-25.1364 StartY=51.2686 StartZ=0 EndX=-25.1354 EndY=51.2803 EndZ=0
    g273: LineSegment StartX=-25.1354 StartY=51.2803 StartZ=0 EndX=-35.6015 EndY=52.4696 EndZ=0
    g274: LineSegment StartX=-35.6015 StartY=52.4696 StartZ=0 EndX=-36.1065 EndY=52.5433 EndZ=0
    g275: LineSegment StartX=-36.1065 StartY=52.5433 StartZ=0 EndX=-36.6076 EndY=52.6472 EndZ=0
    g276: LineSegment StartX=-36.6076 StartY=52.6472 StartZ=0 EndX=-37.0999 EndY=52.7834 EndZ=0
    g277: LineSegment StartX=-37.0999 StartY=52.7834 StartZ=0 EndX=-37.5835 EndY=52.9499 EndZ=0
    g278: LineSegment StartX=-37.5835 StartY=52.9499 StartZ=0 EndX=-38.0554 EndY=53.1457 EndZ=0
    g279: LineSegment StartX=-38.0554 StartY=53.1457 StartZ=0 EndX=-38.5136 EndY=53.3708 EndZ=0
    g280: LineSegment StartX=-38.5136 StartY=53.3708 StartZ=0 EndX=-38.9582 EndY=53.6243 EndZ=0
    g281: LineSegment StartX=-38.9582 StartY=53.6243 StartZ=0 EndX=-39.3853 EndY=53.9041 EndZ=0
    g282: LineSegment StartX=-39.3853 StartY=53.9041 StartZ=0 EndX=-39.7948 EndY=54.2113 EndZ=0
    g283: LineSegment StartX=-39.7948 StartY=54.2113 StartZ=0 EndX=-40.1838 EndY=54.5419 EndZ=0
    g284: LineSegment StartX=-40.1838 StartY=54.5419 StartZ=0 EndX=-40.5513 EndY=54.897 EndZ=0
    g285: LineSegment StartX=-40.5513 StartY=54.897 StartZ=0 EndX=-40.8965 EndY=55.2746 EndZ=0
    g286: LineSegment StartX=-40.8965 StartY=55.2746 StartZ=0 EndX=-41.2172 EndY=55.6717 EndZ=0
    g287: LineSegment StartX=-41.2172 StartY=55.6717 StartZ=0 EndX=-41.5125 EndY=56.0894 EndZ=0
    g288: LineSegment StartX=-41.5125 StartY=56.0894 StartZ=0 EndX=-41.7806 EndY=56.5236 EndZ=0
    g289: LineSegment StartX=-41.7806 StartY=56.5236 StartZ=0 EndX=-42.0223 EndY=56.9746 EndZ=0
    g290: LineSegment StartX=-42.0223 StartY=56.9746 StartZ=0 EndX=-42.2347 EndY=57.4392 EndZ=0
    g291: LineSegment StartX=-42.2347 StartY=57.4392 StartZ=0 EndX=-43.9385 EndY=61.8759 EndZ=0
    g292: LineSegment StartX=-43.9385 StartY=61.8759 StartZ=0 EndX=-45.3622 EndY=66.4095 EndZ=0
    g293: LineSegment StartX=-45.3622 StartY=66.4095 StartZ=0 EndX=-46.5008 EndY=71.0236 EndZ=0
    g294: LineSegment StartX=-46.5008 StartY=71.0236 StartZ=0 EndX=-47.3495 EndY=75.6995 EndZ=0
    g295: LineSegment StartX=-47.3495 StartY=75.6995 StartZ=0 EndX=-47.9042 EndY=80.4196 EndZ=0
    g296: LineSegment StartX=-47.9042 StartY=80.4196 StartZ=0 EndX=-48.1641 EndY=85.1644 EndZ=0
    g297: LineSegment StartX=-48.1641 StartY=85.1644 StartZ=0 EndX=-48.1271 EndY=89.9164 EndZ=0
    g298: LineSegment StartX=-48.1271 StartY=89.9164 StartZ=0 EndX=-47.7932 EndY=94.658 EndZ=0
    g299: LineSegment StartX=-47.7932 StartY=94.658 StartZ=0 EndX=-47.1653 EndY=99.3686 EndZ=0
    g300: LineSegment StartX=-47.1653 StartY=99.3686 StartZ=0 EndX=-46.2444 EndY=104.031 EndZ=0
    g301: LineSegment StartX=-46.2444 StartY=104.031 StartZ=0 EndX=-45.0344 EndY=108.626 EndZ=0
    g302: LineSegment StartX=-45.0344 StartY=108.626 StartZ=0 EndX=-43.5401 EndY=113.137 EndZ=0
    g303: LineSegment StartX=-43.5401 StartY=113.137 StartZ=0 EndX=-41.7673 EndY=117.547 EndZ=0
    g304: LineSegment StartX=-41.7673 StartY=117.547 StartZ=0 EndX=-39.723 EndY=121.836 EndZ=0
    g305: LineSegment StartX=-39.723 StartY=121.836 StartZ=0 EndX=-37.4148 EndY=125.991 EndZ=0
    g306: LineSegment StartX=-37.4148 StartY=125.991 StartZ=0 EndX=-34.8517 EndY=129.993 EndZ=0
    g307: LineSegment StartX=-34.8517 StartY=129.993 StartZ=0 EndX=-32.0441 EndY=133.828 EndZ=0
    g308: LineSegment StartX=-32.0441 StartY=133.828 StartZ=0 EndX=-29.004 EndY=137.479 EndZ=0
    g309: LineSegment StartX=-29.004 StartY=137.479 StartZ=0 EndX=-25.741 EndY=140.935 EndZ=0
    g310: LineSegment StartX=-25.741 StartY=140.935 StartZ=0 EndX=-22.2688 EndY=144.18 EndZ=0
    g311: LineSegment StartX=-22.2688 StartY=144.18 StartZ=0 EndX=-18.6011 EndY=147.202 EndZ=0
    g312: LineSegment StartX=-18.6011 StartY=147.202 StartZ=0 EndX=-14.7515 EndY=149.989 EndZ=0
    g313: LineSegment StartX=-14.7515 StartY=149.989 StartZ=0 EndX=-10.7366 EndY=152.531 EndZ=0
    g314: LineSegment StartX=-10.7366 StartY=152.531 StartZ=0 EndX=-6.57002 EndY=154.817 EndZ=0
    g315: LineSegment StartX=-6.57002 StartY=154.817 StartZ=0 EndX=-6.13176 EndY=155.025 EndZ=0
    g316: LineSegment StartX=-6.13176 StartY=155.025 StartZ=0 EndX=-5.68175 EndY=155.205 EndZ=0
    g317: LineSegment StartX=-5.68175 StartY=155.205 StartZ=0 EndX=-5.22097 EndY=155.359 EndZ=0
    g318: LineSegment StartX=-5.22097 StartY=155.359 StartZ=0 EndX=-4.75333 EndY=155.485 EndZ=0
    g319: LineSegment StartX=-4.75333 StartY=155.485 StartZ=0 EndX=-4.27785 EndY=155.584 EndZ=0
    g320: LineSegment StartX=-4.27785 StartY=155.584 StartZ=0 EndX=-3.79843 EndY=155.654 EndZ=0
    g321: LineSegment StartX=-3.79843 StartY=155.654 StartZ=0 EndX=-3.31508 EndY=155.696 EndZ=0
    g322: LineSegment StartX=-3.31508 StartY=155.696 StartZ=0 EndX=-2.82974 EndY=155.709 EndZ=0
    g323: LineSegment StartX=-2.82974 StartY=155.709 StartZ=0 EndX=-2.34535 EndY=155.694 EndZ=0
    g324: LineSegment StartX=-2.34535 StartY=155.694 StartZ=0 EndX=-1.8619 EndY=155.649 EndZ=0
    g325: LineSegment StartX=-1.8619 StartY=155.649 StartZ=0 EndX=-1.38233 EndY=155.577 EndZ=0
    g326: LineSegment StartX=-1.38233 StartY=155.577 StartZ=0 EndX=-0.907618 EndY=155.476 EndZ=0
    g327: LineSegment StartX=-0.907618 StartY=155.476 StartZ=0 EndX=-0.440686 EndY=155.347 EndZ=0
    g328: LineSegment StartX=-0.440686 StartY=155.347 StartZ=0 EndX=0.0194394 EndY=155.191 EndZ=0
    g329: LineSegment StartX=0.0194394 StartY=155.191 StartZ=0 EndX=13.895 EndY=150.006 EndZ=0
    g330: LineSegment StartX=13.895 StartY=150.006 StartZ=0 EndX=14.0738 EndY=149.933 EndZ=0
    g331: LineSegment StartX=14.0738 StartY=149.933 StartZ=0 EndX=14.2477 EndY=149.849 EndZ=0
    g332: LineSegment StartX=14.2477 StartY=149.849 StartZ=0 EndX=14.4167 EndY=149.754 EndZ=0
    g333: LineSegment StartX=14.4167 StartY=149.754 StartZ=0 EndX=14.5799 EndY=149.65 EndZ=0
    g334: LineSegment StartX=14.5799 StartY=149.65 StartZ=0 EndX=14.7363 EndY=149.536 EndZ=0
    g335: LineSegment StartX=14.7363 StartY=149.536 StartZ=0 EndX=14.8849 EndY=149.413 EndZ=0
    g336: LineSegment StartX=14.8849 StartY=149.413 StartZ=0 EndX=15.0266 EndY=149.281 EndZ=0
    g337: LineSegment StartX=15.0266 StartY=149.281 StartZ=0 EndX=15.1596 EndY=149.141 EndZ=0
    g338: LineSegment StartX=15.1596 StartY=149.141 StartZ=0 EndX=15.2847 EndY=148.993 EndZ=0
    g339: LineSegment StartX=15.2847 StartY=148.993 StartZ=0 EndX=15.3991 EndY=148.837 EndZ=0
    g340: LineSegment StartX=15.3991 StartY=148.837 StartZ=0 EndX=15.5058 EndY=148.675 EndZ=0
    g341: LineSegment StartX=15.5058 StartY=148.675 StartZ=0 EndX=15.6007 EndY=148.508 EndZ=0
    g342: LineSegment StartX=15.6007 StartY=148.508 StartZ=0 EndX=15.6868 EndY=148.335 EndZ=0
    g343: LineSegment StartX=15.6868 StartY=148.335 StartZ=0 EndX=15.7612 EndY=148.156 EndZ=0
    g344: LineSegment StartX=15.7612 StartY=148.156 StartZ=0 EndX=15.8249 EndY=147.974 EndZ=0
    g345: LineSegment StartX=15.8249 StartY=147.974 StartZ=0 EndX=15.8778 EndY=147.787 EndZ=0
    g346: LineSegment StartX=15.8778 StartY=147.787 StartZ=0 EndX=15.919 EndY=147.599 EndZ=0
    g347: LineSegment StartX=15.919 StartY=147.599 StartZ=0 EndX=15.9495 EndY=147.407 EndZ=0
    g348: LineSegment StartX=15.9495 StartY=147.407 StartZ=0 EndX=15.9673 EndY=147.215 EndZ=0
    g349: LineSegment StartX=15.9673 StartY=147.215 StartZ=0 EndX=15.9743 EndY=147.022 EndZ=0
    g350: LineSegment StartX=15.9743 StartY=147.022 StartZ=0 EndX=15.9696 EndY=146.828 EndZ=0
    g351: LineSegment StartX=15.9696 StartY=146.828 StartZ=0 EndX=15.9532 EndY=146.636 EndZ=0
    g352: LineSegment StartX=15.9532 StartY=146.636 StartZ=0 EndX=15.9241 EndY=146.444 EndZ=0
    g353: LineSegment StartX=15.9241 StartY=146.444 StartZ=0 EndX=15.8843 EndY=146.255 EndZ=0
    g354: LineSegment StartX=15.8843 StartY=146.255 StartZ=0 EndX=15.8337 EndY=146.068 EndZ=0
    g355: LineSegment StartX=15.8337 StartY=146.068 StartZ=0 EndX=12.9607 EndY=136.71 EndZ=0
    g356: LineSegment StartX=12.9607 StartY=136.71 StartZ=0 EndX=12.7981 EndY=136.233 EndZ=0
    g357: LineSegment StartX=12.7981 StartY=136.233 StartZ=0 EndX=12.6062 EndY=135.767 EndZ=0
    g358: LineSegment StartX=12.6062 StartY=135.767 StartZ=0 EndX=12.3869 EndY=135.314 EndZ=0
    g359: LineSegment StartX=12.3869 StartY=135.314 StartZ=0 EndX=12.1394 EndY=134.875 EndZ=0
    g360: LineSegment StartX=12.1394 StartY=134.875 StartZ=0 EndX=11.8654 EndY=134.452 EndZ=0
    g361: LineSegment StartX=11.8654 StartY=134.452 StartZ=0 EndX=11.566 EndY=134.047 EndZ=0
    g362: LineSegment StartX=11.566 StartY=134.047 StartZ=0 EndX=11.2432 EndY=133.661 EndZ=0
    g363: LineSegment StartX=11.2432 StartY=133.661 StartZ=0 EndX=10.8969 EndY=133.296 EndZ=0
    g364: LineSegment StartX=10.8969 StartY=133.296 StartZ=0 EndX=10.5281 EndY=132.952 EndZ=0
    g365: LineSegment StartX=10.5281 StartY=132.952 StartZ=0 EndX=10.1397 EndY=132.632 EndZ=0
    g366: LineSegment StartX=10.1397 StartY=132.632 StartZ=0 EndX=9.73186 EndY=132.335 EndZ=0
    g367: LineSegment StartX=9.73186 StartY=132.335 StartZ=0 EndX=9.30636 EndY=132.065 EndZ=0
    g368: LineSegment StartX=9.30636 StartY=132.065 StartZ=0 EndX=8.86618 EndY=131.822 EndZ=0
    g369: LineSegment StartX=8.86618 StartY=131.822 StartZ=0 EndX=8.41035 EndY=131.606 EndZ=0
    g370: LineSegment StartX=8.41035 StartY=131.606 StartZ=0 EndX=5.6461 EndY=130.29 EndZ=0
    g371: LineSegment StartX=5.6461 StartY=130.29 StartZ=0 EndX=2.9709 EndY=128.804 EndZ=0
    g372: LineSegment StartX=2.9709 StartY=128.804 StartZ=0 EndX=0.392551 EndY=127.153 EndZ=0
    g373: LineSegment StartX=0.392551 StartY=127.153 StartZ=0 EndX=-2.07626 EndY=125.343 EndZ=0
    g374: LineSegment StartX=-2.07626 StartY=125.343 StartZ=0 EndX=-4.42674 EndY=123.381 EndZ=0
    g375: LineSegment StartX=-4.42674 StartY=123.381 StartZ=0 EndX=-6.64915 EndY=121.277 EndZ=0
    g376: LineSegment StartX=-6.64915 StartY=121.277 StartZ=0 EndX=-8.73567 EndY=119.037 EndZ=0
    g377: LineSegment StartX=-8.73567 StartY=119.037 StartZ=0 EndX=-10.6766 EndY=116.67 EndZ=0
    g378: LineSegment StartX=-10.6766 StartY=116.67 StartZ=0 EndX=-12.4659 EndY=114.186 EndZ=0
    g379: LineSegment StartX=-12.4659 StartY=114.186 StartZ=0 EndX=-14.096 EndY=111.595 EndZ=0
    g380: LineSegment StartX=-14.096 StartY=111.595 StartZ=0 EndX=-15.56 EndY=108.907 EndZ=0
    g381: LineSegment StartX=-15.56 StartY=108.907 StartZ=0 EndX=-16.852 EndY=106.132 EndZ=0
    g382: LineSegment StartX=-16.852 StartY=106.132 StartZ=0 EndX=-17.9672 EndY=103.281 EndZ=0
    g383: LineSegment StartX=-17.9672 StartY=103.281 StartZ=0 EndX=-18.9017 EndY=100.366 EndZ=0
    g384: LineSegment StartX=-18.9017 StartY=100.366 StartZ=0 EndX=-19.6515 EndY=97.3974 EndZ=0
    g385: LineSegment StartX=-19.6515 StartY=97.3974 StartZ=0 EndX=-20.2138 EndY=94.389 EndZ=0
    g386: LineSegment StartX=-20.2138 StartY=94.389 StartZ=0 EndX=-20.5856 EndY=91.3505 EndZ=0
    g387: LineSegment StartX=-20.5856 StartY=91.3505 StartZ=0 EndX=-20.766 EndY=88.2947 EndZ=0
    g388: LineSegment StartX=-20.766 StartY=88.2947 StartZ=0 EndX=-20.755 EndY=85.2332 EndZ=0
    g389: LineSegment StartX=-20.755 StartY=85.2332 StartZ=0 EndX=-20.5506 EndY=82.1787 EndZ=0
    g390: LineSegment StartX=-20.5506 StartY=82.1787 StartZ=0 EndX=-20.1558 EndY=79.143 EndZ=0
    g391: LineSegment StartX=11.6806 StartY=145.84 StartZ=0 EndX=11.6092 EndY=145.912 EndZ=0
    g392: LineSegment StartX=11.6092 StartY=145.912 StartZ=0 EndX=11.5428 EndY=145.987 EndZ=0
    g393: LineSegment StartX=11.5428 StartY=145.987 StartZ=0 EndX=11.4811 EndY=146.066 EndZ=0
    g394: LineSegment StartX=11.4811 StartY=146.066 StartZ=0 EndX=11.4244 EndY=146.149 EndZ=0
    g395: LineSegment StartX=11.4244 StartY=146.149 StartZ=0 EndX=11.3735 EndY=146.236 EndZ=0
    g396: LineSegment StartX=11.3735 StartY=146.236 StartZ=0 EndX=11.3276 EndY=146.325 EndZ=0
    g397: LineSegment StartX=11.3276 StartY=146.325 StartZ=0 EndX=11.2874 EndY=146.417 EndZ=0
    g398: LineSegment StartX=11.2874 StartY=146.417 StartZ=0 EndX=11.2531 EndY=146.512 EndZ=0
    g399: LineSegment StartX=11.2531 StartY=146.512 StartZ=0 EndX=11.2247 EndY=146.608 EndZ=0
    ... +2387 more geometry lines
FEATURE [Sketcher::SketchObject] Sketch037  label="new-main-orig"
  ArcFitTolerance = 1e-06
  FullyConstrained = false
  MakeInternals = false
  sketch-geometry (151):
    g0: ArcOfCircle CenterX=6.91631 CenterY=35.2156 CenterZ=0 NormalX=0 NormalY=0 NormalZ=1 AngleXU=0 Radius=30 StartAngle=2.49893 EndAngle=2.9338
    g1: ArcOfCircle CenterX=13.4083 CenterY=148.194 CenterZ=0 NormalX=0 NormalY=0 NormalZ=1 AngleXU=0 Radius=6 StartAngle=0.587689 EndAngle=1.8031
    g2: ArcOfCircle CenterX=-116.743 CenterY=156.308 CenterZ=0 NormalX=0 NormalY=0 NormalZ=1 AngleXU=0 Radius=50 StartAngle=3.76427 EndAngle=4.23401
    g3: ArcOfCircle CenterX=-198.877 CenterY=148.194 CenterZ=0 NormalX=0 NormalY=0 NormalZ=1 AngleXU=0 Radius=6 StartAngle=1.3385 EndAngle=2.5539
    g4: ArcOfCircle CenterX=-185.146 CenterY=50.5737 CenterZ=0 NormalX=0 NormalY=0 NormalZ=1 AngleXU=0 Radius=15 StartAngle=0.642664 EndAngle=1.34877
    g5: ArcOfCircle CenterX=-192.385 CenterY=35.2156 CenterZ=0 NormalX=0 NormalY=0 NormalZ=1 AngleXU=0 Radius=30 StartAngle=0.207795 EndAngle=0.642664
    g6: Circle CenterX=12.7717 CenterY=147.009 CenterZ=0 NormalX=0 NormalY=0 NormalZ=-1 AngleXU=0 Radius=1.6
    g7: Circle CenterX=-7.97108 CenterY=132.586 CenterZ=0 NormalX=0 NormalY=0 NormalZ=-1 AngleXU=0 Radius=0.4
    g8: Circle CenterX=-2.3874 CenterY=136.467 CenterZ=0 NormalX=0 NormalY=0 NormalZ=-1 AngleXU=0 Radius=0.4
    g9: Circle CenterX=-16.7911 CenterY=144.662 CenterZ=0 NormalX=0 NormalY=0 NormalZ=-1 AngleXU=0 Radius=0.3
    g10: Circle CenterX=-14.7382 CenterY=146.089 CenterZ=0 NormalX=0 NormalY=0 NormalZ=-1 AngleXU=0 Radius=0.3
    g11: Circle CenterX=-12.6854 CenterY=147.516 CenterZ=0 NormalX=0 NormalY=0 NormalZ=-1 AngleXU=0 Radius=0.3
    g12: Circle CenterX=-10.6326 CenterY=148.943 CenterZ=0 NormalX=0 NormalY=0 NormalZ=-1 AngleXU=0 Radius=0.3
    g13: Circle CenterX=-32.5224 CenterY=127.909 CenterZ=0 NormalX=0 NormalY=0 NormalZ=-1 AngleXU=0 Radius=0.3
    g14: Circle CenterX=-33.8174 CenterY=125.77 CenterZ=0 NormalX=0 NormalY=0 NormalZ=-1 AngleXU=0 Radius=0.3
    g15: Circle CenterX=-36.4074 CenterY=121.494 CenterZ=0 NormalX=0 NormalY=0 NormalZ=-1 AngleXU=0 Radius=0.3
    g16: Circle CenterX=-35.1124 CenterY=123.632 CenterZ=0 NormalX=0 NormalY=0 NormalZ=-1 AngleXU=0 Radius=0.3
    g17: Circle CenterX=-19.9157 CenterY=119.865 CenterZ=0 NormalX=0 NormalY=0 NormalZ=-1 AngleXU=0 Radius=0.4
    g18: Circle CenterX=-23.4381 CenterY=114.049 CenterZ=0 NormalX=0 NormalY=0 NormalZ=-1 AngleXU=0 Radius=0.4
    g19: Circle CenterX=-43.9645 CenterY=99.7902 CenterZ=0 NormalX=0 NormalY=0 NormalZ=-1 AngleXU=0 Radius=0.3
    g20: Circle CenterX=-44.2777 CenterY=97.3099 CenterZ=0 NormalX=0 NormalY=0 NormalZ=-1 AngleXU=0 Radius=0.3
    g21: Circle CenterX=-44.591 CenterY=94.8296 CenterZ=0 NormalX=0 NormalY=0 NormalZ=-1 AngleXU=0 Radius=0.3
    g22: Circle CenterX=-44.9042 CenterY=92.3493 CenterZ=0 NormalX=0 NormalY=0 NormalZ=-1 AngleXU=0 Radius=0.3
    g23: Circle CenterX=-29.1761 CenterY=97.5697 CenterZ=0 NormalX=0 NormalY=0 NormalZ=-1 AngleXU=0 Radius=0.4
    g24: Circle CenterX=-30.0282 CenterY=90.8233 CenterZ=0 NormalX=0 NormalY=0 NormalZ=-1 AngleXU=0 Radius=0.4
    g25: Circle CenterX=-28.5675 CenterY=73.435 CenterZ=0 NormalX=0 NormalY=0 NormalZ=-1 AngleXU=0 Radius=0.4
    g26: Circle CenterX=-26.6018 CenterY=66.9252 CenterZ=0 NormalX=0 NormalY=0 NormalZ=-1 AngleXU=0 Radius=0.4
    g27: Circle CenterX=-24.8748 CenterY=54.489 CenterZ=0 NormalX=0 NormalY=0 NormalZ=-1 AngleXU=0 Radius=1.6
    g28: Circle CenterX=-40.8125 CenterY=62.2687 CenterZ=0 NormalX=0 NormalY=0 NormalZ=-1 AngleXU=0 Radius=0.3
    g29: Circle CenterX=-41.5351 CenterY=64.662 CenterZ=0 NormalX=0 NormalY=0 NormalZ=-1 AngleXU=0 Radius=0.3
    g30: Circle CenterX=-42.2578 CenterY=67.0552 CenterZ=0 NormalX=0 NormalY=0 NormalZ=-1 AngleXU=0 Radius=0.3
    g31: Circle CenterX=-42.9804 CenterY=69.4485 CenterZ=0 NormalX=0 NormalY=0 NormalZ=-1 AngleXU=0 Radius=0.3
    g32: LineSegment StartX=-6.24247 StartY=153.577 StartZ=0 EndX=8.02604 EndY=133.049 EndZ=0
    g33: LineSegment StartX=-6.24247 StartY=153.577 StartZ=0 EndX=-22.6651 EndY=142.162 EndZ=0
    g34: LineSegment StartX=-22.6651 StartY=142.162 StartZ=0 EndX=-8.39657 EndY=121.634 EndZ=0
    g35: LineSegment StartX=8.02604 StartY=133.049 StartZ=0 EndX=-8.39657 EndY=121.634 EndZ=0
    g36: LineSegment StartX=-30.3969 StartY=133.928 StartZ=0 EndX=-9.01234 EndY=120.978 EndZ=0
    g37: LineSegment StartX=-9.01234 StartY=120.978 StartZ=0 EndX=-19.3723 EndY=103.871 EndZ=0
    g38: LineSegment StartX=-40.7568 StartY=116.821 StartZ=0 EndX=-19.3723 EndY=103.871 EndZ=0
    g39: LineSegment StartX=-21.6198 StartY=120.43 StartZ=0 EndX=-24.7278 EndY=115.297 EndZ=0
    g40: LineSegment StartX=-21.6198 StartY=120.43 StartZ=0 EndX=-18.626 EndY=118.617 EndZ=0
    g41: LineSegment StartX=-18.626 StartY=118.617 StartZ=0 EndX=-21.734 EndY=113.484 EndZ=0
    g42: LineSegment StartX=-24.7278 StartY=115.297 StartZ=0 EndX=-21.734 EndY=113.484 EndZ=0
    g43: LineSegment StartX=-30.3969 StartY=133.928 StartZ=0 EndX=-40.7568 EndY=116.821 EndZ=0
    g44: LineSegment StartX=-44.4711 StartY=106.154 StartZ=0 EndX=-19.6681 EndY=103.021 EndZ=0
    g45: LineSegment StartX=-19.6681 StartY=103.021 StartZ=0 EndX=-22.1741 EndY=83.1789 EndZ=0
    g46: LineSegment StartX=-27.4901 StartY=96.9536 StartZ=0 EndX=-28.2419 EndY=91.0008 EndZ=0
    g47: LineSegment StartX=-30.9625 StartY=97.3921 StartZ=0 EndX=-27.4901 EndY=96.9536 EndZ=0
    g48: LineSegment StartX=-30.9625 StartY=97.3921 StartZ=0 EndX=-31.7143 EndY=91.4394 EndZ=0
    g49: LineSegment StartX=-31.7143 StartY=91.4394 StartZ=0 EndX=-28.2419 EndY=91.0008 EndZ=0
    g50: LineSegment StartX=-44.4711 StartY=106.154 StartZ=0 EndX=-46.9771 EndY=86.3114 EndZ=0
    g51: LineSegment StartX=-46.9771 StartY=86.3114 StartZ=0 EndX=-22.1741 EndY=83.1789 EndZ=0
    g52: LineSegment StartX=-46.0316 StartY=75.0559 StartZ=0 EndX=-22.0988 EndY=82.2825 EndZ=0
    g53: LineSegment StartX=-22.0988 StartY=82.2825 StartZ=0 EndX=-16.3176 EndY=63.1363 EndZ=0
    g54: LineSegment StartX=-40.2503 StartY=55.9097 StartZ=0 EndX=-16.3176 EndY=63.1363 EndZ=0
    g55: LineSegment StartX=-28.3928 StartY=66.8023 StartZ=0 EndX=-25.0422 EndY=67.814 EndZ=0
    g56: LineSegment StartX=-30.1271 StartY=72.5462 StartZ=0 EndX=-28.3928 EndY=66.8023 EndZ=0
    g57: LineSegment StartX=-26.7766 StartY=73.5579 StartZ=0 EndX=-25.0422 EndY=67.814 EndZ=0
    g58: LineSegment StartX=-30.1271 StartY=72.5462 StartZ=0 EndX=-26.7766 EndY=73.5579 EndZ=0
    g59: LineSegment StartX=-46.0316 StartY=75.0559 StartZ=0 EndX=-40.2503 EndY=55.9097 EndZ=0
    g60: LineSegment StartX=-35.7029 StartY=52.5216 StartZ=0 EndX=-25.238 EndY=51.3215 EndZ=0
    g61: ArcOfCircle CenterX=-24.8748 CenterY=54.489 CenterZ=0 NormalX=0 NormalY=0 NormalZ=1 AngleXU=0 Radius=3.2 StartAngle=4.59821 EndAngle=5.64052
    g62: ArcOfCircle CenterX=-34.7687 CenterY=60.6682 CenterZ=0 NormalX=0 NormalY=0 NormalZ=1 AngleXU=0 Radius=8.2 StartAngle=3.53847 EndAngle=4.59821
    g63: LineSegment StartX=-15.767 StartY=61.3147 StartZ=0 EndX=-22.3132 EndY=52.5712 EndZ=0
    g64: ArcOfCircle CenterX=-18.3286 CenterY=63.2325 CenterZ=0 NormalX=0 NormalY=0 NormalZ=1 AngleXU=0 Radius=3.2 StartAngle=5.64052 EndAngle=6.75694
    g65: ArcOfCircle CenterX=27.9007 CenterY=86.9341 CenterZ=0 NormalX=0 NormalY=0 NormalZ=1 AngleXU=0 Radius=48.7511 StartAngle=1.9825 EndAngle=3.61535
    g66: ArcOfCircle CenterX=27.9007 CenterY=86.9341 CenterZ=0 NormalX=0 NormalY=0 NormalZ=1 AngleXU=0 Radius=76.1511 StartAngle=2.04047 EndAngle=3.53847
    g67: ArcOfCircle CenterX=-2.85354 CenterY=147.527 CenterZ=0 NormalX=0 NormalY=0 NormalZ=1 AngleXU=0 Radius=8.2 StartAngle=1.21213 EndAngle=2.04047
    g68: LineSegment StartX=0.0248341 StartY=155.205 StartZ=0 EndX=13.895 EndY=150.006 EndZ=0
    g69: ArcOfCircle CenterX=12.7717 CenterY=147.009 CenterZ=0 NormalX=0 NormalY=0 NormalZ=1 AngleXU=0 Radius=3.2 StartAngle=5.98426 EndAngle=7.49532
    g70: LineSegment StartX=12.9468 StartY=136.711 StartZ=0 EndX=15.8298 EndY=146.067 EndZ=0
    g71: ArcOfCircle CenterX=5.11046 CenterY=139.126 CenterZ=0 NormalX=0 NormalY=0 NormalZ=1 AngleXU=0 Radius=8.2 StartAngle=5.12409 EndAngle=5.98426
    g72: LineSegment StartX=14.667 StartY=136.181 StartZ=0 EndX=17.55 EndY=145.537 EndZ=0
    g73: ArcOfCircle CenterX=5.11046 CenterY=139.126 CenterZ=0 NormalX=0 NormalY=0 NormalZ=1 AngleXU=0 Radius=10 StartAngle=5.12409 EndAngle=5.98426
    g74: ArcOfCircle CenterX=12.7717 CenterY=147.009 CenterZ=0 NormalX=0 NormalY=0 NormalZ=1 AngleXU=0 Radius=5 StartAngle=5.98426 EndAngle=7.49532
    g75: ArcOfCircle CenterX=27.9007 CenterY=86.9341 CenterZ=0 NormalX=0 NormalY=0 NormalZ=1 AngleXU=0 Radius=46.9511 StartAngle=1.9825 EndAngle=3.61535
    g76: ArcOfCircle CenterX=-24.8748 CenterY=54.489 CenterZ=0 NormalX=0 NormalY=0 NormalZ=1 AngleXU=0 Radius=5 StartAngle=4.59821 EndAngle=5.64052
    g77: LineSegment StartX=-14.3261 StartY=60.2359 StartZ=0 EndX=-20.8723 EndY=51.4924 EndZ=0
    g78: ArcOfCircle CenterX=-18.3286 CenterY=63.2325 CenterZ=0 NormalX=0 NormalY=0 NormalZ=1 AngleXU=0 Radius=5 StartAngle=5.64052 EndAngle=6.75694
    g79: ArcOfCircle CenterX=27.9007 CenterY=86.9341 CenterZ=0 NormalX=0 NormalY=0 NormalZ=1 AngleXU=0 Radius=77.9511 StartAngle=2.04047 EndAngle=3.53847
    g80: LineSegment StartX=0.656673 StartY=156.891 StartZ=0 EndX=14.5268 EndY=151.691 EndZ=0
    g81: ArcOfCircle CenterX=-2.85354 CenterY=147.527 CenterZ=0 NormalX=0 NormalY=0 NormalZ=1 AngleXU=0 Radius=10 StartAngle=1.21213 EndAngle=2.04047
    g82: LineSegment StartX=-35.908 StartY=50.7333 StartZ=0 EndX=-25.4431 EndY=49.5332 EndZ=0
    g83: ArcOfCircle CenterX=-34.7687 CenterY=60.6682 CenterZ=0 NormalX=0 NormalY=0 NormalZ=1 AngleXU=0 Radius=10 StartAngle=3.53847 EndAngle=4.59821
    g84: ArcOfCircle CenterX=-81.3039 CenterY=180.564 CenterZ=0 NormalX=0 NormalY=0 NormalZ=1 AngleXU=0 Radius=77.3239 StartAngle=4.75433 EndAngle=5.19077
    g85: ArcOfCircle CenterX=-209.705 CenterY=17.0182 CenterZ=0 NormalX=0 NormalY=0 NormalZ=1 AngleXU=0 Radius=17 StartAngle=3.40529 EndAngle=4.71239
    g86: LineSegment StartX=-173.412 StartY=0.0182067 StartZ=0 EndX=-209.705 EndY=0.0182067 EndZ=0
    g87: ArcOfCircle CenterX=-173.412 CenterY=30.0182 CenterZ=0 NormalX=0 NormalY=0 NormalZ=1 AngleXU=0 Radius=30 StartAngle=4.71239 EndAngle=5.10704
    g88: ArcOfCircle CenterX=-217.408 CenterY=135.651 CenterZ=0 NormalX=0 NormalY=0 NormalZ=1 AngleXU=0 Radius=144.429 StartAngle=5.10704 EndAngle=5.1698
    g89: ArcOfCircle CenterX=-144.792 CenterY=-11.8744 CenterZ=0 NormalX=0 NormalY=0 NormalZ=1 AngleXU=0 Radius=20 StartAngle=1.66649 EndAngle=2.0282
    g90: ArcOfCircle CenterX=-92.7345 CenterY=-554.217 CenterZ=0 NormalX=0 NormalY=0 NormalZ=1 AngleXU=0 Radius=564.835 StartAngle=1.47229 EndAngle=1.66649
    g91: Circle CenterX=-92.7345 CenterY=48.8363 CenterZ=0 NormalX=0 NormalY=0 NormalZ=-1 AngleXU=0 Radius=14.3449
    g92: ArcOfCircle CenterX=24.2365 CenterY=17.0182 CenterZ=0 NormalX=0 NormalY=0 NormalZ=1 AngleXU=0 Radius=17 StartAngle=4.71239 EndAngle=6.01949
    g93: LineSegment StartX=-12.0567 StartY=0.0182067 StartZ=0 EndX=24.2365 EndY=0.0182067 EndZ=0
    g94: ArcOfCircle CenterX=24.2365 CenterY=17.0182 CenterZ=0 NormalX=0 NormalY=0 NormalZ=1 AngleXU=0 Radius=17 StartAngle=4.71239 EndAngle=6.01949
    g95: ArcOfCircle CenterX=31.9393 CenterY=135.651 CenterZ=0 NormalX=0 NormalY=0 NormalZ=1 AngleXU=0 Radius=144.429 StartAngle=4.25498 EndAngle=4.31774
    g96: ArcOfCircle CenterX=-12.0567 CenterY=30.0182 CenterZ=0 NormalX=0 NormalY=0 NormalZ=1 AngleXU=0 Radius=30 StartAngle=4.31774 EndAngle=4.71239
    g97: ArcOfCircle CenterX=-40.6765 CenterY=-11.8744 CenterZ=0 NormalX=0 NormalY=0 NormalZ=1 AngleXU=0 Radius=20 StartAngle=1.11339 EndAngle=1.4751
    g98: ArcOfCircle CenterX=-177.461 CenterY=31.8587 CenterZ=0 NormalX=0 NormalY=0 NormalZ=1 AngleXU=0 Radius=15 StartAngle=4.71239 EndAngle=6.22689
    g99: ArcOfCircle CenterX=-104.165 CenterY=180.564 CenterZ=0 NormalX=0 NormalY=0 NormalZ=1 AngleXU=0 Radius=77.3239 StartAngle=4.23401 EndAngle=4.67045
    g100: ArcOfCircle CenterX=-8.0079 CenterY=31.8587 CenterZ=0 NormalX=0 NormalY=0 NormalZ=1 AngleXU=0 Radius=15 StartAngle=3.19789 EndAngle=4.71239
    g101: LineSegment StartX=-78.0619 StartY=103.308 StartZ=0 EndX=-107.407 EndY=103.308 EndZ=0
    g102: LineSegment StartX=12.0694 StartY=16.8587 StartZ=0 EndX=-8.0079 EndY=16.8587 EndZ=0
    g103: ArcOfCircle CenterX=12.0694 CenterY=21.8587 CenterZ=0 NormalX=0 NormalY=0 NormalZ=1 AngleXU=0 Radius=5 StartAngle=4.71239 EndAngle=6.02246
    g104: Circle CenterX=-92.7345 CenterY=20.8363 CenterZ=0 NormalX=0 NormalY=0 NormalZ=-1 AngleXU=0 Radius=2.5
    g105: Circle CenterX=-68.4858 CenterY=34.8363 CenterZ=0 NormalX=0 NormalY=0 NormalZ=-1 AngleXU=0 Radius=2.5
    g106: Circle CenterX=-68.4858 CenterY=62.8363 CenterZ=0 NormalX=0 NormalY=0 NormalZ=-1 AngleXU=0 Radius=2.5
    g107: Circle CenterX=-92.7345 CenterY=76.8363 CenterZ=0 NormalX=0 NormalY=0 NormalZ=-1 AngleXU=0 Radius=2.5
    g108: Circle CenterX=-116.983 CenterY=62.8363 CenterZ=0 NormalX=0 NormalY=0 NormalZ=-1 AngleXU=0 Radius=2.5
    g109: Circle CenterX=-116.983 CenterY=34.8363 CenterZ=0 NormalX=0 NormalY=0 NormalZ=-1 AngleXU=0 Radius=2.5
    g110: LineSegment StartX=14.667 StartY=136.181 StartZ=0 EndX=17.55 EndY=145.537 EndZ=0
    g111: ArcOfCircle CenterX=5.11046 CenterY=139.126 CenterZ=0 NormalX=0 NormalY=0 NormalZ=1 AngleXU=0 Radius=10 StartAngle=5.12409 EndAngle=5.98426
    g112: ArcOfCircle CenterX=12.7717 CenterY=147.009 CenterZ=0 NormalX=0 NormalY=0 NormalZ=1 AngleXU=0 Radius=5 StartAngle=5.98426 EndAngle=8.10068
    g113: ArcOfCircle CenterX=-122.381 CenterY=57.7293 CenterZ=0 NormalX=0 NormalY=0 NormalZ=1 AngleXU=0 Radius=169.165 StartAngle=6.01194 EndAngle=6.87087
    g114: ArcOfCircle CenterX=-122.381 CenterY=57.7293 CenterZ=0 NormalX=0 NormalY=0 NormalZ=1 AngleXU=0 Radius=144.165 StartAngle=6.02246 EndAngle=6.87647
    g115: ArcOfCircle CenterX=27.9007 CenterY=86.9341 CenterZ=0 NormalX=0 NormalY=0 NormalZ=1 AngleXU=0 Radius=46.9511 StartAngle=1.9825 EndAngle=3.61535
    g116: ArcOfCircle CenterX=-24.8748 CenterY=54.489 CenterZ=0 NormalX=0 NormalY=0 NormalZ=1 AngleXU=0 Radius=5 StartAngle=3.69281 EndAngle=5.64052
    g117: LineSegment StartX=-14.3261 StartY=60.2359 StartZ=0 EndX=-20.8723 EndY=51.4924 EndZ=0
    g118: ArcOfCircle CenterX=-18.3286 CenterY=63.2325 CenterZ=0 NormalX=0 NormalY=0 NormalZ=1 AngleXU=0 Radius=5 StartAngle=5.64052 EndAngle=6.75694
    g119: ArcOfCircle CenterX=10.468 CenterY=34.4667 CenterZ=0 NormalX=0 NormalY=0 NormalZ=1 AngleXU=0 Radius=33.6298 StartAngle=2.9338 EndAngle=3.24442
    g120: LineSegment StartX=22.1801 StartY=90.0965 StartZ=0 EndX=-18.1225 EndY=77.6462 EndZ=0
    g121: LineSegment StartX=13.7526 StartY=155.624 StartZ=0 EndX=37.2839 EndY=155.624 EndZ=0
    g122: LineSegment StartX=34.0087 StartY=141.42 StartZ=0 EndX=30.243 EndY=161.285 EndZ=0
    g123: LineSegment StartX=34.0087 StartY=141.42 StartZ=0 EndX=34.0087 EndY=118.377 EndZ=0
    g124: ArcOfCircle CenterX=-213.37 CenterY=86.9341 CenterZ=0 NormalX=0 NormalY=0 NormalZ=1 AngleXU=0 Radius=66.9511 StartAngle=5.73197 EndAngle=7.60728
    g125: ArcOfCircle CenterX=-213.37 CenterY=86.9341 CenterZ=0 NormalX=0 NormalY=0 NormalZ=1 AngleXU=0 Radius=46.9511 StartAngle=5.80943 EndAngle=7.44228
    g126: LineSegment StartX=-171.143 StartY=60.2359 StartZ=0 EndX=-164.597 EndY=51.4924 EndZ=0
    g127: ArcOfCircle CenterX=-167.14 CenterY=63.2325 CenterZ=0 NormalX=0 NormalY=0 NormalZ=1 AngleXU=0 Radius=5 StartAngle=2.66784 EndAngle=3.78426
    g128: ArcOfCircle CenterX=-160.594 CenterY=54.489 CenterZ=0 NormalX=0 NormalY=0 NormalZ=1 AngleXU=0 Radius=5 StartAngle=3.78426 EndAngle=5.73197
    g129: Circle CenterX=-160.679 CenterY=65.3219 CenterZ=0 NormalX=0 NormalY=0 NormalZ=-1 AngleXU=0 Radius=5
    g130: Circle CenterX=-156.618 CenterY=82.1667 CenterZ=0 NormalX=0 NormalY=0 NormalZ=-1 AngleXU=0 Radius=5
    g131: Circle CenterX=-157.811 CenterY=99.4527 CenterZ=0 NormalX=0 NormalY=0 NormalZ=-1 AngleXU=0 Radius=5
    g132: Circle CenterX=-164.147 CenterY=115.58 CenterZ=0 NormalX=0 NormalY=0 NormalZ=-1 AngleXU=0 Radius=5
    g133: Circle CenterX=-175.039 CenterY=129.056 CenterZ=0 NormalX=0 NormalY=0 NormalZ=-1 AngleXU=0 Radius=5
    g134: Circle CenterX=-189.48 CenterY=138.632 CenterZ=0 NormalX=0 NormalY=0 NormalZ=-1 AngleXU=0 Radius=5
    g135: LineSegment StartX=-200.136 StartY=136.181 StartZ=0 EndX=-203.019 EndY=145.537 EndZ=0
    g136: ArcOfCircle CenterX=-198.241 CenterY=147.009 CenterZ=0 NormalX=0 NormalY=0 NormalZ=1 AngleXU=0 Radius=5 StartAngle=1.32409 EndAngle=3.44052
    g137: ArcOfCircle CenterX=-190.579 CenterY=139.126 CenterZ=0 NormalX=0 NormalY=0 NormalZ=1 AngleXU=0 Radius=10 StartAngle=3.44052 EndAngle=4.30068
    g138: ArcOfCircle CenterX=-213.37 CenterY=86.9341 CenterZ=0 NormalX=0 NormalY=0 NormalZ=1 AngleXU=0 Radius=68.9511 StartAngle=0.622676 EndAngle=1.3385
    g139: ArcOfCircle CenterX=-213.37 CenterY=86.9341 CenterZ=0 NormalX=0 NormalY=0 NormalZ=1 AngleXU=0 Radius=66.9511 StartAngle=5.73197 EndAngle=7.60728
    g140: LineSegment StartX=-199.222 StartY=155.624 StartZ=0 EndX=-222.753 EndY=155.624 EndZ=0
    g141: ArcOfCircle CenterX=-63.0876 CenterY=57.7293 CenterZ=0 NormalX=0 NormalY=0 NormalZ=1 AngleXU=0 Radius=169.165 StartAngle=2.5539 EndAngle=3.41284
    g142: ArcOfCircle CenterX=-63.0876 CenterY=57.7293 CenterZ=0 NormalX=0 NormalY=0 NormalZ=1 AngleXU=0 Radius=144.165 StartAngle=2.5483 EndAngle=3.40231
    g143: LineSegment StartX=-207.649 StartY=90.0965 StartZ=0 EndX=-167.346 EndY=77.6462 EndZ=0
    g144: LineSegment StartX=-208.059 StartY=71.1239 StartZ=0 EndX=-181.843 EndY=65.2056 EndZ=0
    g145: LineSegment StartX=-173.138 StartY=59.5637 StartZ=0 EndX=-168.37 EndY=53.1955 EndZ=0
    g146: ArcOfCircle CenterX=-195.937 CenterY=34.4667 CenterZ=0 NormalX=0 NormalY=0 NormalZ=1 AngleXU=0 Radius=33.6298 StartAngle=6.18035 EndAngle=6.49098
    g147: LineSegment StartX=-197.538 StartY=16.8587 StartZ=0 EndX=-177.461 EndY=16.8587 EndZ=0
    g148: ArcOfCircle CenterX=-197.538 CenterY=21.8587 CenterZ=0 NormalX=0 NormalY=0 NormalZ=1 AngleXU=0 Radius=5 StartAngle=3.40231 EndAngle=4.71239
    g149: LineSegment StartX=-219.478 StartY=141.42 StartZ=0 EndX=-215.712 EndY=161.285 EndZ=0
    g150: LineSegment StartX=-219.478 StartY=141.42 StartZ=0 EndX=-219.478 EndY=118.377 EndZ=0
FEATURE [Sketcher::SketchObject] Sketch039  label="new-main002"
  ArcFitTolerance = 1e-06
  FullyConstrained = false
  MakeInternals = false
  sketch-geometry (151):
    g0: ArcOfCircle CenterX=6.91631 CenterY=35.2156 CenterZ=0 NormalX=0 NormalY=0 NormalZ=1 AngleXU=0 Radius=30 StartAngle=2.49893 EndAngle=2.9338
    g1: ArcOfCircle CenterX=13.4083 CenterY=148.194 CenterZ=0 NormalX=0 NormalY=0 NormalZ=1 AngleXU=0 Radius=6 StartAngle=0.587689 EndAngle=1.8031
    g2: ArcOfCircle CenterX=-116.743 CenterY=156.308 CenterZ=0 NormalX=0 NormalY=0 NormalZ=1 AngleXU=0 Radius=50 StartAngle=3.76427 EndAngle=4.23401
    g3: ArcOfCircle CenterX=-198.877 CenterY=148.194 CenterZ=0 NormalX=0 NormalY=0 NormalZ=1 AngleXU=0 Radius=6 StartAngle=1.3385 EndAngle=2.5539
    g4: ArcOfCircle CenterX=-185.146 CenterY=50.5737 CenterZ=0 NormalX=0 NormalY=0 NormalZ=1 AngleXU=0 Radius=15 StartAngle=0.642664 EndAngle=1.34877
    g5: ArcOfCircle CenterX=-192.385 CenterY=35.2156 CenterZ=0 NormalX=0 NormalY=0 NormalZ=1 AngleXU=0 Radius=30 StartAngle=0.207795 EndAngle=0.642664
    g6: Circle CenterX=12.7717 CenterY=147.009 CenterZ=0 NormalX=0 NormalY=0 NormalZ=-1 AngleXU=0 Radius=1.6
    g7: Circle CenterX=-7.97108 CenterY=132.586 CenterZ=0 NormalX=0 NormalY=0 NormalZ=-1 AngleXU=0 Radius=0.4
    g8: Circle CenterX=-2.3874 CenterY=136.467 CenterZ=0 NormalX=0 NormalY=0 NormalZ=-1 AngleXU=0 Radius=0.4
    g9: Circle CenterX=-16.7911 CenterY=144.662 CenterZ=0 NormalX=0 NormalY=0 NormalZ=-1 AngleXU=0 Radius=0.3
    g10: Circle CenterX=-14.7382 CenterY=146.089 CenterZ=0 NormalX=0 NormalY=0 NormalZ=-1 AngleXU=0 Radius=0.3
    g11: Circle CenterX=-12.6854 CenterY=147.516 CenterZ=0 NormalX=0 NormalY=0 NormalZ=-1 AngleXU=0 Radius=0.3
    g12: Circle CenterX=-10.6326 CenterY=148.943 CenterZ=0 NormalX=0 NormalY=0 NormalZ=-1 AngleXU=0 Radius=0.3
    g13: Circle CenterX=-32.5224 CenterY=127.909 CenterZ=0 NormalX=0 NormalY=0 NormalZ=-1 AngleXU=0 Radius=0.3
    g14: Circle CenterX=-33.8174 CenterY=125.77 CenterZ=0 NormalX=0 NormalY=0 NormalZ=-1 AngleXU=0 Radius=0.3
    g15: Circle CenterX=-36.4074 CenterY=121.494 CenterZ=0 NormalX=0 NormalY=0 NormalZ=-1 AngleXU=0 Radius=0.3
    g16: Circle CenterX=-35.1124 CenterY=123.632 CenterZ=0 NormalX=0 NormalY=0 NormalZ=-1 AngleXU=0 Radius=0.3
    g17: Circle CenterX=-19.9157 CenterY=119.865 CenterZ=0 NormalX=0 NormalY=0 NormalZ=-1 AngleXU=0 Radius=0.4
    g18: Circle CenterX=-23.4381 CenterY=114.049 CenterZ=0 NormalX=0 NormalY=0 NormalZ=-1 AngleXU=0 Radius=0.4
    g19: Circle CenterX=-43.9645 CenterY=99.7902 CenterZ=0 NormalX=0 NormalY=0 NormalZ=-1 AngleXU=0 Radius=0.3
    g20: Circle CenterX=-44.2777 CenterY=97.3099 CenterZ=0 NormalX=0 NormalY=0 NormalZ=-1 AngleXU=0 Radius=0.3
    g21: Circle CenterX=-44.591 CenterY=94.8296 CenterZ=0 NormalX=0 NormalY=0 NormalZ=-1 AngleXU=0 Radius=0.3
    g22: Circle CenterX=-44.9042 CenterY=92.3493 CenterZ=0 NormalX=0 NormalY=0 NormalZ=-1 AngleXU=0 Radius=0.3
    g23: Circle CenterX=-29.1761 CenterY=97.5697 CenterZ=0 NormalX=0 NormalY=0 NormalZ=-1 AngleXU=0 Radius=0.4
    g24: Circle CenterX=-30.0282 CenterY=90.8233 CenterZ=0 NormalX=0 NormalY=0 NormalZ=-1 AngleXU=0 Radius=0.4
    g25: Circle CenterX=-28.5675 CenterY=73.435 CenterZ=0 NormalX=0 NormalY=0 NormalZ=-1 AngleXU=0 Radius=0.4
    g26: Circle CenterX=-26.6018 CenterY=66.9252 CenterZ=0 NormalX=0 NormalY=0 NormalZ=-1 AngleXU=0 Radius=0.4
    g27: Circle CenterX=-24.8748 CenterY=54.489 CenterZ=0 NormalX=0 NormalY=0 NormalZ=-1 AngleXU=0 Radius=1.6
    g28: Circle CenterX=-40.8125 CenterY=62.2687 CenterZ=0 NormalX=0 NormalY=0 NormalZ=-1 AngleXU=0 Radius=0.3
    g29: Circle CenterX=-41.5351 CenterY=64.662 CenterZ=0 NormalX=0 NormalY=0 NormalZ=-1 AngleXU=0 Radius=0.3
    g30: Circle CenterX=-42.2578 CenterY=67.0552 CenterZ=0 NormalX=0 NormalY=0 NormalZ=-1 AngleXU=0 Radius=0.3
    g31: Circle CenterX=-42.9804 CenterY=69.4485 CenterZ=0 NormalX=0 NormalY=0 NormalZ=-1 AngleXU=0 Radius=0.3
    g32: LineSegment StartX=-6.24247 StartY=153.577 StartZ=0 EndX=8.02604 EndY=133.049 EndZ=0
    g33: LineSegment StartX=-6.24247 StartY=153.577 StartZ=0 EndX=-22.6651 EndY=142.162 EndZ=0
    g34: LineSegment StartX=-22.6651 StartY=142.162 StartZ=0 EndX=-8.39657 EndY=121.634 EndZ=0
    g35: LineSegment StartX=8.02604 StartY=133.049 StartZ=0 EndX=-8.39657 EndY=121.634 EndZ=0
    g36: LineSegment StartX=-30.3969 StartY=133.928 StartZ=0 EndX=-9.01234 EndY=120.978 EndZ=0
    g37: LineSegment StartX=-9.01234 StartY=120.978 StartZ=0 EndX=-19.3723 EndY=103.871 EndZ=0
    g38: LineSegment StartX=-40.7568 StartY=116.821 StartZ=0 EndX=-19.3723 EndY=103.871 EndZ=0
    g39: LineSegment StartX=-21.6198 StartY=120.43 StartZ=0 EndX=-24.7278 EndY=115.297 EndZ=0
    g40: LineSegment StartX=-21.6198 StartY=120.43 StartZ=0 EndX=-18.626 EndY=118.617 EndZ=0
    g41: LineSegment StartX=-18.626 StartY=118.617 StartZ=0 EndX=-21.734 EndY=113.484 EndZ=0
    g42: LineSegment StartX=-24.7278 StartY=115.297 StartZ=0 EndX=-21.734 EndY=113.484 EndZ=0
    g43: LineSegment StartX=-30.3969 StartY=133.928 StartZ=0 EndX=-40.7568 EndY=116.821 EndZ=0
    g44: LineSegment StartX=-44.4711 StartY=106.154 StartZ=0 EndX=-19.6681 EndY=103.021 EndZ=0
    g45: LineSegment StartX=-19.6681 StartY=103.021 StartZ=0 EndX=-22.1741 EndY=83.1789 EndZ=0
    g46: LineSegment StartX=-27.4901 StartY=96.9536 StartZ=0 EndX=-28.2419 EndY=91.0008 EndZ=0
    g47: LineSegment StartX=-30.9625 StartY=97.3921 StartZ=0 EndX=-27.4901 EndY=96.9536 EndZ=0
    g48: LineSegment StartX=-30.9625 StartY=97.3921 StartZ=0 EndX=-31.7143 EndY=91.4394 EndZ=0
    g49: LineSegment StartX=-31.7143 StartY=91.4394 StartZ=0 EndX=-28.2419 EndY=91.0008 EndZ=0
    g50: LineSegment StartX=-44.4711 StartY=106.154 StartZ=0 EndX=-46.9771 EndY=86.3114 EndZ=0
    g51: LineSegment StartX=-46.9771 StartY=86.3114 StartZ=0 EndX=-22.1741 EndY=83.1789 EndZ=0
    g52: LineSegment StartX=-46.0316 StartY=75.0559 StartZ=0 EndX=-22.0988 EndY=82.2825 EndZ=0
    g53: LineSegment StartX=-22.0988 StartY=82.2825 StartZ=0 EndX=-16.3176 EndY=63.1363 EndZ=0
    g54: LineSegment StartX=-40.2503 StartY=55.9097 StartZ=0 EndX=-16.3176 EndY=63.1363 EndZ=0
    g55: LineSegment StartX=-28.3928 StartY=66.8023 StartZ=0 EndX=-25.0422 EndY=67.814 EndZ=0
    g56: LineSegment StartX=-30.1271 StartY=72.5462 StartZ=0 EndX=-28.3928 EndY=66.8023 EndZ=0
    g57: LineSegment StartX=-26.7766 StartY=73.5579 StartZ=0 EndX=-25.0422 EndY=67.814 EndZ=0
    g58: LineSegment StartX=-30.1271 StartY=72.5462 StartZ=0 EndX=-26.7766 EndY=73.5579 EndZ=0
    g59: LineSegment StartX=-46.0316 StartY=75.0559 StartZ=0 EndX=-40.2503 EndY=55.9097 EndZ=0
    g60: LineSegment StartX=-35.7029 StartY=52.5216 StartZ=0 EndX=-25.238 EndY=51.3215 EndZ=0
    g61: ArcOfCircle CenterX=-24.8748 CenterY=54.489 CenterZ=0 NormalX=0 NormalY=0 NormalZ=1 AngleXU=0 Radius=3.2 StartAngle=4.59821 EndAngle=5.64052
    g62: ArcOfCircle CenterX=-34.7687 CenterY=60.6682 CenterZ=0 NormalX=0 NormalY=0 NormalZ=1 AngleXU=0 Radius=8.2 StartAngle=3.53847 EndAngle=4.59821
    g63: LineSegment StartX=-15.767 StartY=61.3147 StartZ=0 EndX=-22.3132 EndY=52.5712 EndZ=0
    g64: ArcOfCircle CenterX=-18.3286 CenterY=63.2325 CenterZ=0 NormalX=0 NormalY=0 NormalZ=1 AngleXU=0 Radius=3.2 StartAngle=5.64052 EndAngle=6.75694
    g65: ArcOfCircle CenterX=27.9007 CenterY=86.9341 CenterZ=0 NormalX=0 NormalY=0 NormalZ=1 AngleXU=0 Radius=48.7511 StartAngle=1.9825 EndAngle=3.61535
    g66: ArcOfCircle CenterX=27.9007 CenterY=86.9341 CenterZ=0 NormalX=0 NormalY=0 NormalZ=1 AngleXU=0 Radius=76.1511 StartAngle=2.04047 EndAngle=3.53847
    g67: ArcOfCircle CenterX=-2.85354 CenterY=147.527 CenterZ=0 NormalX=0 NormalY=0 NormalZ=1 AngleXU=0 Radius=8.2 StartAngle=1.21213 EndAngle=2.04047
    g68: LineSegment StartX=0.0248341 StartY=155.205 StartZ=0 EndX=13.895 EndY=150.006 EndZ=0
    g69: ArcOfCircle CenterX=12.7717 CenterY=147.009 CenterZ=0 NormalX=0 NormalY=0 NormalZ=1 AngleXU=0 Radius=3.2 StartAngle=5.98426 EndAngle=7.49532
    g70: LineSegment StartX=12.9468 StartY=136.711 StartZ=0 EndX=15.8298 EndY=146.067 EndZ=0
    g71: ArcOfCircle CenterX=5.11046 CenterY=139.126 CenterZ=0 NormalX=0 NormalY=0 NormalZ=1 AngleXU=0 Radius=8.2 StartAngle=5.12409 EndAngle=5.98426
    g72: LineSegment StartX=14.667 StartY=136.181 StartZ=0 EndX=17.55 EndY=145.537 EndZ=0
    g73: ArcOfCircle CenterX=5.11046 CenterY=139.126 CenterZ=0 NormalX=0 NormalY=0 NormalZ=1 AngleXU=0 Radius=10 StartAngle=5.12409 EndAngle=5.98426
    g74: ArcOfCircle CenterX=12.7717 CenterY=147.009 CenterZ=0 NormalX=0 NormalY=0 NormalZ=1 AngleXU=0 Radius=5 StartAngle=5.98426 EndAngle=7.49532
    g75: ArcOfCircle CenterX=27.9007 CenterY=86.9341 CenterZ=0 NormalX=0 NormalY=0 NormalZ=1 AngleXU=0 Radius=46.9511 StartAngle=1.9825 EndAngle=3.61535
    g76: ArcOfCircle CenterX=-24.8748 CenterY=54.489 CenterZ=0 NormalX=0 NormalY=0 NormalZ=1 AngleXU=0 Radius=5 StartAngle=4.59821 EndAngle=5.64052
    g77: LineSegment StartX=-14.3261 StartY=60.2359 StartZ=0 EndX=-20.8723 EndY=51.4924 EndZ=0
    g78: ArcOfCircle CenterX=-18.3286 CenterY=63.2325 CenterZ=0 NormalX=0 NormalY=0 NormalZ=1 AngleXU=0 Radius=5 StartAngle=5.64052 EndAngle=6.75694
    g79: ArcOfCircle CenterX=27.9007 CenterY=86.9341 CenterZ=0 NormalX=0 NormalY=0 NormalZ=1 AngleXU=0 Radius=77.9511 StartAngle=2.04047 EndAngle=3.53847
    g80: LineSegment StartX=0.656673 StartY=156.891 StartZ=0 EndX=14.5268 EndY=151.691 EndZ=0
    g81: ArcOfCircle CenterX=-2.85354 CenterY=147.527 CenterZ=0 NormalX=0 NormalY=0 NormalZ=1 AngleXU=0 Radius=10 StartAngle=1.21213 EndAngle=2.04047
    g82: LineSegment StartX=-35.908 StartY=50.7333 StartZ=0 EndX=-25.4431 EndY=49.5332 EndZ=0
    g83: ArcOfCircle CenterX=-34.7687 CenterY=60.6682 CenterZ=0 NormalX=0 NormalY=0 NormalZ=1 AngleXU=0 Radius=10 StartAngle=3.53847 EndAngle=4.59821
    g84: ArcOfCircle CenterX=-81.3039 CenterY=180.564 CenterZ=0 NormalX=0 NormalY=0 NormalZ=1 AngleXU=0 Radius=77.3239 StartAngle=4.75433 EndAngle=5.19077
    g85: ArcOfCircle CenterX=-209.705 CenterY=17.0182 CenterZ=0 NormalX=0 NormalY=0 NormalZ=1 AngleXU=0 Radius=17 StartAngle=3.40529 EndAngle=4.71239
    g86: LineSegment StartX=-173.412 StartY=0.0182067 StartZ=0 EndX=-209.705 EndY=0.0182067 EndZ=0
    g87: ArcOfCircle CenterX=-173.412 CenterY=30.0182 CenterZ=0 NormalX=0 NormalY=0 NormalZ=1 AngleXU=0 Radius=30 StartAngle=4.71239 EndAngle=5.10704
    g88: ArcOfCircle CenterX=-217.408 CenterY=135.651 CenterZ=0 NormalX=0 NormalY=0 NormalZ=1 AngleXU=0 Radius=144.429 StartAngle=5.10704 EndAngle=5.1698
    g89: ArcOfCircle CenterX=-144.792 CenterY=-11.8744 CenterZ=0 NormalX=0 NormalY=0 NormalZ=1 AngleXU=0 Radius=20 StartAngle=1.66649 EndAngle=2.0282
    g90: ArcOfCircle CenterX=-92.7345 CenterY=-554.217 CenterZ=0 NormalX=0 NormalY=0 NormalZ=1 AngleXU=0 Radius=564.835 StartAngle=1.47229 EndAngle=1.66649
    g91: Circle CenterX=-92.7345 CenterY=48.8363 CenterZ=0 NormalX=0 NormalY=0 NormalZ=-1 AngleXU=0 Radius=14.3449
    g92: ArcOfCircle CenterX=24.2365 CenterY=17.0182 CenterZ=0 NormalX=0 NormalY=0 NormalZ=1 AngleXU=0 Radius=17 StartAngle=4.71239 EndAngle=6.01949
    g93: LineSegment StartX=-12.0567 StartY=0.0182067 StartZ=0 EndX=24.2365 EndY=0.0182067 EndZ=0
    g94: ArcOfCircle CenterX=24.2365 CenterY=17.0182 CenterZ=0 NormalX=0 NormalY=0 NormalZ=1 AngleXU=0 Radius=17 StartAngle=4.71239 EndAngle=6.01949
    g95: ArcOfCircle CenterX=31.9393 CenterY=135.651 CenterZ=0 NormalX=0 NormalY=0 NormalZ=1 AngleXU=0 Radius=144.429 StartAngle=4.25498 EndAngle=4.31774
    g96: ArcOfCircle CenterX=-12.0567 CenterY=30.0182 CenterZ=0 NormalX=0 NormalY=0 NormalZ=1 AngleXU=0 Radius=30 StartAngle=4.31774 EndAngle=4.71239
    g97: ArcOfCircle CenterX=-40.6765 CenterY=-11.8744 CenterZ=0 NormalX=0 NormalY=0 NormalZ=1 AngleXU=0 Radius=20 StartAngle=1.11339 EndAngle=1.4751
    g98: ArcOfCircle CenterX=-177.461 CenterY=31.8587 CenterZ=0 NormalX=0 NormalY=0 NormalZ=1 AngleXU=0 Radius=15 StartAngle=4.71239 EndAngle=6.22689
    g99: ArcOfCircle CenterX=-104.165 CenterY=180.564 CenterZ=0 NormalX=0 NormalY=0 NormalZ=1 AngleXU=0 Radius=77.3239 StartAngle=4.23401 EndAngle=4.67045
    g100: ArcOfCircle CenterX=-8.0079 CenterY=31.8587 CenterZ=0 NormalX=0 NormalY=0 NormalZ=1 AngleXU=0 Radius=15 StartAngle=3.19789 EndAngle=4.71239
    g101: LineSegment StartX=-78.0619 StartY=103.308 StartZ=0 EndX=-107.407 EndY=103.308 EndZ=0
    g102: LineSegment StartX=12.0694 StartY=16.8587 StartZ=0 EndX=-8.0079 EndY=16.8587 EndZ=0
    g103: ArcOfCircle CenterX=12.0694 CenterY=21.8587 CenterZ=0 NormalX=0 NormalY=0 NormalZ=1 AngleXU=0 Radius=5 StartAngle=4.71239 EndAngle=6.02246
    g104: Circle CenterX=-92.7345 CenterY=20.8363 CenterZ=0 NormalX=0 NormalY=0 NormalZ=-1 AngleXU=0 Radius=2.5
    g105: Circle CenterX=-68.4858 CenterY=34.8363 CenterZ=0 NormalX=0 NormalY=0 NormalZ=-1 AngleXU=0 Radius=2.5
    g106: Circle CenterX=-68.4858 CenterY=62.8363 CenterZ=0 NormalX=0 NormalY=0 NormalZ=-1 AngleXU=0 Radius=2.5
    g107: Circle CenterX=-92.7345 CenterY=76.8363 CenterZ=0 NormalX=0 NormalY=0 NormalZ=-1 AngleXU=0 Radius=2.5
    g108: Circle CenterX=-116.983 CenterY=62.8363 CenterZ=0 NormalX=0 NormalY=0 NormalZ=-1 AngleXU=0 Radius=2.5
    g109: Circle CenterX=-116.983 CenterY=34.8363 CenterZ=0 NormalX=0 NormalY=0 NormalZ=-1 AngleXU=0 Radius=2.5
    g110: LineSegment StartX=14.667 StartY=136.181 StartZ=0 EndX=17.55 EndY=145.537 EndZ=0
    g111: ArcOfCircle CenterX=5.11046 CenterY=139.126 CenterZ=0 NormalX=0 NormalY=0 NormalZ=1 AngleXU=0 Radius=10 StartAngle=5.12409 EndAngle=5.98426
    g112: ArcOfCircle CenterX=12.7717 CenterY=147.009 CenterZ=0 NormalX=0 NormalY=0 NormalZ=1 AngleXU=0 Radius=5 StartAngle=5.98426 EndAngle=8.10068
    g113: ArcOfCircle CenterX=-122.381 CenterY=57.7293 CenterZ=0 NormalX=0 NormalY=0 NormalZ=1 AngleXU=0 Radius=169.165 StartAngle=6.01194 EndAngle=6.87087
    g114: ArcOfCircle CenterX=-122.381 CenterY=57.7293 CenterZ=0 NormalX=0 NormalY=0 NormalZ=1 AngleXU=0 Radius=144.165 StartAngle=6.02246 EndAngle=6.87647
    g115: ArcOfCircle CenterX=27.9007 CenterY=86.9341 CenterZ=0 NormalX=0 NormalY=0 NormalZ=1 AngleXU=0 Radius=46.9511 StartAngle=1.9825 EndAngle=3.61535
    g116: ArcOfCircle CenterX=-24.8748 CenterY=54.489 CenterZ=0 NormalX=0 NormalY=0 NormalZ=1 AngleXU=0 Radius=5 StartAngle=3.69281 EndAngle=5.64052
    g117: LineSegment StartX=-14.3261 StartY=60.2359 StartZ=0 EndX=-20.8723 EndY=51.4924 EndZ=0
    g118: ArcOfCircle CenterX=-18.3286 CenterY=63.2325 CenterZ=0 NormalX=0 NormalY=0 NormalZ=1 AngleXU=0 Radius=5 StartAngle=5.64052 EndAngle=6.75694
    g119: ArcOfCircle CenterX=10.468 CenterY=34.4667 CenterZ=0 NormalX=0 NormalY=0 NormalZ=1 AngleXU=0 Radius=33.6298 StartAngle=2.9338 EndAngle=3.24442
    g120: LineSegment StartX=22.1801 StartY=90.0965 StartZ=0 EndX=-18.1225 EndY=77.6462 EndZ=0
    g121: LineSegment StartX=13.7526 StartY=155.624 StartZ=0 EndX=37.2839 EndY=155.624 EndZ=0
    g122: LineSegment StartX=34.0087 StartY=141.42 StartZ=0 EndX=30.243 EndY=161.285 EndZ=0
    g123: LineSegment StartX=34.0087 StartY=141.42 StartZ=0 EndX=34.0087 EndY=118.377 EndZ=0
    g124: ArcOfCircle CenterX=-213.37 CenterY=86.9341 CenterZ=0 NormalX=0 NormalY=0 NormalZ=1 AngleXU=0 Radius=66.9511 StartAngle=5.73197 EndAngle=7.60728
    g125: ArcOfCircle CenterX=-213.37 CenterY=86.9341 CenterZ=0 NormalX=0 NormalY=0 NormalZ=1 AngleXU=0 Radius=46.9511 StartAngle=5.80943 EndAngle=7.44228
    g126: LineSegment StartX=-171.143 StartY=60.2359 StartZ=0 EndX=-164.597 EndY=51.4924 EndZ=0
    g127: ArcOfCircle CenterX=-167.14 CenterY=63.2325 CenterZ=0 NormalX=0 NormalY=0 NormalZ=1 AngleXU=0 Radius=5 StartAngle=2.66784 EndAngle=3.78426
    g128: ArcOfCircle CenterX=-160.594 CenterY=54.489 CenterZ=0 NormalX=0 NormalY=0 NormalZ=1 AngleXU=0 Radius=5 StartAngle=3.78426 EndAngle=5.73197
    g129: Circle CenterX=-160.679 CenterY=65.3219 CenterZ=0 NormalX=0 NormalY=0 NormalZ=-1 AngleXU=0 Radius=5
    g130: Circle CenterX=-156.618 CenterY=82.1667 CenterZ=0 NormalX=0 NormalY=0 NormalZ=-1 AngleXU=0 Radius=5
    g131: Circle CenterX=-157.811 CenterY=99.4527 CenterZ=0 NormalX=0 NormalY=0 NormalZ=-1 AngleXU=0 Radius=5
    g132: Circle CenterX=-164.147 CenterY=115.58 CenterZ=0 NormalX=0 NormalY=0 NormalZ=-1 AngleXU=0 Radius=5
    g133: Circle CenterX=-175.039 CenterY=129.056 CenterZ=0 NormalX=0 NormalY=0 NormalZ=-1 AngleXU=0 Radius=5
    g134: Circle CenterX=-189.48 CenterY=138.632 CenterZ=0 NormalX=0 NormalY=0 NormalZ=-1 AngleXU=0 Radius=5
    g135: LineSegment StartX=-200.136 StartY=136.181 StartZ=0 EndX=-203.019 EndY=145.537 EndZ=0
    g136: ArcOfCircle CenterX=-198.241 CenterY=147.009 CenterZ=0 NormalX=0 NormalY=0 NormalZ=1 AngleXU=0 Radius=5 StartAngle=1.32409 EndAngle=3.44052
    g137: ArcOfCircle CenterX=-190.579 CenterY=139.126 CenterZ=0 NormalX=0 NormalY=0 NormalZ=1 AngleXU=0 Radius=10 StartAngle=3.44052 EndAngle=4.30068
    g138: ArcOfCircle CenterX=-213.37 CenterY=86.9341 CenterZ=0 NormalX=0 NormalY=0 NormalZ=1 AngleXU=0 Radius=68.9511 StartAngle=0.622676 EndAngle=1.3385
    g139: ArcOfCircle CenterX=-213.37 CenterY=86.9341 CenterZ=0 NormalX=0 NormalY=0 NormalZ=1 AngleXU=0 Radius=66.9511 StartAngle=5.73197 EndAngle=7.60728
    g140: LineSegment StartX=-199.222 StartY=155.624 StartZ=0 EndX=-222.753 EndY=155.624 EndZ=0
    g141: ArcOfCircle CenterX=-63.0876 CenterY=57.7293 CenterZ=0 NormalX=0 NormalY=0 NormalZ=1 AngleXU=0 Radius=169.165 StartAngle=2.5539 EndAngle=3.41284
    g142: ArcOfCircle CenterX=-63.0876 CenterY=57.7293 CenterZ=0 NormalX=0 NormalY=0 NormalZ=1 AngleXU=0 Radius=144.165 StartAngle=2.5483 EndAngle=3.40231
    g143: LineSegment StartX=-207.649 StartY=90.0965 StartZ=0 EndX=-167.346 EndY=77.6462 EndZ=0
    g144: LineSegment StartX=-208.059 StartY=71.1239 StartZ=0 EndX=-181.843 EndY=65.2056 EndZ=0
    g145: LineSegment StartX=-173.138 StartY=59.5637 StartZ=0 EndX=-168.37 EndY=53.1955 EndZ=0
    g146: ArcOfCircle CenterX=-195.937 CenterY=34.4667 CenterZ=0 NormalX=0 NormalY=0 NormalZ=1 AngleXU=0 Radius=33.6298 StartAngle=6.18035 EndAngle=6.49098
    g147: LineSegment StartX=-197.538 StartY=16.8587 StartZ=0 EndX=-177.461 EndY=16.8587 EndZ=0
    g148: ArcOfCircle CenterX=-197.538 CenterY=21.8587 CenterZ=0 NormalX=0 NormalY=0 NormalZ=1 AngleXU=0 Radius=5 StartAngle=3.40231 EndAngle=4.71239
    g149: LineSegment StartX=-219.478 StartY=141.42 StartZ=0 EndX=-215.712 EndY=161.285 EndZ=0
    g150: LineSegment StartX=-219.478 StartY=141.42 StartZ=0 EndX=-219.478 EndY=118.377 EndZ=0
FEATURE [Sketcher::SketchObject] Sketch040  label="new-mainoledonly"
  ArcFitTolerance = 1e-06
  FullyConstrained = false
  MakeInternals = false
  sketch-geometry (85):
    g0: Circle CenterX=12.7717 CenterY=147.009 CenterZ=0 NormalX=0 NormalY=0 NormalZ=-1 AngleXU=0 Radius=1.6
    g1: Circle CenterX=-7.97108 CenterY=132.586 CenterZ=0 NormalX=0 NormalY=0 NormalZ=-1 AngleXU=0 Radius=0.4
    g2: Circle CenterX=-2.3874 CenterY=136.467 CenterZ=0 NormalX=0 NormalY=0 NormalZ=-1 AngleXU=0 Radius=0.4
    g3: Circle CenterX=-16.7911 CenterY=144.662 CenterZ=0 NormalX=0 NormalY=0 NormalZ=-1 AngleXU=0 Radius=0.3
    g4: Circle CenterX=-14.7382 CenterY=146.089 CenterZ=0 NormalX=0 NormalY=0 NormalZ=-1 AngleXU=0 Radius=0.3
    g5: Circle CenterX=-12.6854 CenterY=147.516 CenterZ=0 NormalX=0 NormalY=0 NormalZ=-1 AngleXU=0 Radius=0.3
    g6: Circle CenterX=-10.6326 CenterY=148.943 CenterZ=0 NormalX=0 NormalY=0 NormalZ=-1 AngleXU=0 Radius=0.3
    g7: Circle CenterX=-32.5224 CenterY=127.909 CenterZ=0 NormalX=0 NormalY=0 NormalZ=-1 AngleXU=0 Radius=0.3
    g8: Circle CenterX=-33.8174 CenterY=125.77 CenterZ=0 NormalX=0 NormalY=0 NormalZ=-1 AngleXU=0 Radius=0.3
    g9: Circle CenterX=-36.4074 CenterY=121.494 CenterZ=0 NormalX=0 NormalY=0 NormalZ=-1 AngleXU=0 Radius=0.3
    g10: Circle CenterX=-35.1124 CenterY=123.632 CenterZ=0 NormalX=0 NormalY=0 NormalZ=-1 AngleXU=0 Radius=0.3
    g11: Circle CenterX=-19.9157 CenterY=119.865 CenterZ=0 NormalX=0 NormalY=0 NormalZ=-1 AngleXU=0 Radius=0.4
    g12: Circle CenterX=-23.4381 CenterY=114.049 CenterZ=0 NormalX=0 NormalY=0 NormalZ=-1 AngleXU=0 Radius=0.4
    g13: Circle CenterX=-43.9645 CenterY=99.7902 CenterZ=0 NormalX=0 NormalY=0 NormalZ=-1 AngleXU=0 Radius=0.3
    g14: Circle CenterX=-44.2777 CenterY=97.3099 CenterZ=0 NormalX=0 NormalY=0 NormalZ=-1 AngleXU=0 Radius=0.3
    g15: Circle CenterX=-44.591 CenterY=94.8296 CenterZ=0 NormalX=0 NormalY=0 NormalZ=-1 AngleXU=0 Radius=0.3
    g16: Circle CenterX=-44.9042 CenterY=92.3493 CenterZ=0 NormalX=0 NormalY=0 NormalZ=-1 AngleXU=0 Radius=0.3
    g17: Circle CenterX=-29.1761 CenterY=97.5697 CenterZ=0 NormalX=0 NormalY=0 NormalZ=-1 AngleXU=0 Radius=0.4
    g18: Circle CenterX=-30.0282 CenterY=90.8233 CenterZ=0 NormalX=0 NormalY=0 NormalZ=-1 AngleXU=0 Radius=0.4
    g19: Circle CenterX=-28.5675 CenterY=73.435 CenterZ=0 NormalX=0 NormalY=0 NormalZ=-1 AngleXU=0 Radius=0.4
    g20: Circle CenterX=-26.6018 CenterY=66.9252 CenterZ=0 NormalX=0 NormalY=0 NormalZ=-1 AngleXU=0 Radius=0.4
    g21: Circle CenterX=-24.8748 CenterY=54.489 CenterZ=0 NormalX=0 NormalY=0 NormalZ=-1 AngleXU=0 Radius=1.6
    g22: Circle CenterX=-40.8125 CenterY=62.2687 CenterZ=0 NormalX=0 NormalY=0 NormalZ=-1 AngleXU=0 Radius=0.3
    g23: Circle CenterX=-41.5351 CenterY=64.662 CenterZ=0 NormalX=0 NormalY=0 NormalZ=-1 AngleXU=0 Radius=0.3
    g24: Circle CenterX=-42.2578 CenterY=67.0552 CenterZ=0 NormalX=0 NormalY=0 NormalZ=-1 AngleXU=0 Radius=0.3
    g25: Circle CenterX=-42.9804 CenterY=69.4485 CenterZ=0 NormalX=0 NormalY=0 NormalZ=-1 AngleXU=0 Radius=0.3
    g26: LineSegment StartX=-6.24247 StartY=153.577 StartZ=0 EndX=8.02604 EndY=133.049 EndZ=0
    g27: LineSegment StartX=-6.24247 StartY=153.577 StartZ=0 EndX=-22.6651 EndY=142.162 EndZ=0
    g28: LineSegment StartX=-22.6651 StartY=142.162 StartZ=0 EndX=-8.39657 EndY=121.634 EndZ=0
    g29: LineSegment StartX=8.02604 StartY=133.049 StartZ=0 EndX=-8.39657 EndY=121.634 EndZ=0
    g30: LineSegment StartX=-30.3969 StartY=133.928 StartZ=0 EndX=-9.01234 EndY=120.978 EndZ=0
    g31: LineSegment StartX=-9.01234 StartY=120.978 StartZ=0 EndX=-19.3723 EndY=103.871 EndZ=0
    g32: LineSegment StartX=-40.7568 StartY=116.821 StartZ=0 EndX=-19.3723 EndY=103.871 EndZ=0
    g33: LineSegment StartX=-21.6198 StartY=120.43 StartZ=0 EndX=-24.7278 EndY=115.297 EndZ=0
    g34: LineSegment StartX=-21.6198 StartY=120.43 StartZ=0 EndX=-18.626 EndY=118.617 EndZ=0
    g35: LineSegment StartX=-18.626 StartY=118.617 StartZ=0 EndX=-21.734 EndY=113.484 EndZ=0
    g36: LineSegment StartX=-24.7278 StartY=115.297 StartZ=0 EndX=-21.734 EndY=113.484 EndZ=0
    g37: LineSegment StartX=-30.3969 StartY=133.928 StartZ=0 EndX=-40.7568 EndY=116.821 EndZ=0
    g38: LineSegment StartX=-44.4711 StartY=106.154 StartZ=0 EndX=-19.6681 EndY=103.021 EndZ=0
    g39: LineSegment StartX=-19.6681 StartY=103.021 StartZ=0 EndX=-22.1741 EndY=83.1789 EndZ=0
    g40: LineSegment StartX=-27.4901 StartY=96.9536 StartZ=0 EndX=-28.2419 EndY=91.0008 EndZ=0
    g41: LineSegment StartX=-30.9625 StartY=97.3921 StartZ=0 EndX=-27.4901 EndY=96.9536 EndZ=0
    g42: LineSegment StartX=-30.9625 StartY=97.3921 StartZ=0 EndX=-31.7143 EndY=91.4394 EndZ=0
    g43: LineSegment StartX=-31.7143 StartY=91.4394 StartZ=0 EndX=-28.2419 EndY=91.0008 EndZ=0
    g44: LineSegment StartX=-44.4711 StartY=106.154 StartZ=0 EndX=-46.9771 EndY=86.3114 EndZ=0
    g45: LineSegment StartX=-46.9771 StartY=86.3114 StartZ=0 EndX=-22.1741 EndY=83.1789 EndZ=0
    g46: LineSegment StartX=-46.0316 StartY=75.0559 StartZ=0 EndX=-22.0988 EndY=82.2825 EndZ=0
    g47: LineSegment StartX=-22.0988 StartY=82.2825 StartZ=0 EndX=-16.3176 EndY=63.1363 EndZ=0
    g48: LineSegment StartX=-40.2503 StartY=55.9097 StartZ=0 EndX=-16.3176 EndY=63.1363 EndZ=0
    g49: LineSegment StartX=-28.3928 StartY=66.8023 StartZ=0 EndX=-25.0422 EndY=67.814 EndZ=0
    g50: LineSegment StartX=-30.1271 StartY=72.5462 StartZ=0 EndX=-28.3928 EndY=66.8023 EndZ=0
    g51: LineSegment StartX=-26.7766 StartY=73.5579 StartZ=0 EndX=-25.0422 EndY=67.814 EndZ=0
    g52: LineSegment StartX=-30.1271 StartY=72.5462 StartZ=0 EndX=-26.7766 EndY=73.5579 EndZ=0
    g53: LineSegment StartX=-46.0316 StartY=75.0559 StartZ=0 EndX=-40.2503 EndY=55.9097 EndZ=0
    g54: LineSegment StartX=-35.7029 StartY=52.5216 StartZ=0 EndX=-25.238 EndY=51.3215 EndZ=0
    g55: ArcOfCircle CenterX=-24.8748 CenterY=54.489 CenterZ=0 NormalX=0 NormalY=0 NormalZ=1 AngleXU=0 Radius=3.2 StartAngle=4.59821 EndAngle=5.64052
    g56: ArcOfCircle CenterX=-34.7687 CenterY=60.6682 CenterZ=0 NormalX=0 NormalY=0 NormalZ=1 AngleXU=0 Radius=8.2 StartAngle=3.53847 EndAngle=4.59821
    g57: LineSegment StartX=-15.767 StartY=61.3147 StartZ=0 EndX=-22.3132 EndY=52.5712 EndZ=0
    g58: ArcOfCircle CenterX=-18.3286 CenterY=63.2325 CenterZ=0 NormalX=0 NormalY=0 NormalZ=1 AngleXU=0 Radius=3.2 StartAngle=5.64052 EndAngle=6.75694
    g59: ArcOfCircle CenterX=27.9007 CenterY=86.9341 CenterZ=0 NormalX=0 NormalY=0 NormalZ=1 AngleXU=0 Radius=48.7511 StartAngle=1.9825 EndAngle=3.61535
    g60: ArcOfCircle CenterX=27.9007 CenterY=86.9341 CenterZ=0 NormalX=0 NormalY=0 NormalZ=1 AngleXU=0 Radius=76.1511 StartAngle=2.04047 EndAngle=3.53847
    g61: ArcOfCircle CenterX=-2.85354 CenterY=147.527 CenterZ=0 NormalX=0 NormalY=0 NormalZ=1 AngleXU=0 Radius=8.2 StartAngle=1.21213 EndAngle=2.04047
    g62: LineSegment StartX=0.0248341 StartY=155.205 StartZ=0 EndX=13.895 EndY=150.006 EndZ=0
    g63: ArcOfCircle CenterX=12.7717 CenterY=147.009 CenterZ=0 NormalX=0 NormalY=0 NormalZ=1 AngleXU=0 Radius=3.2 StartAngle=5.98426 EndAngle=7.49532
    g64: LineSegment StartX=12.9468 StartY=136.711 StartZ=0 EndX=15.8298 EndY=146.067 EndZ=0
    g65: ArcOfCircle CenterX=5.11046 CenterY=139.126 CenterZ=0 NormalX=0 NormalY=0 NormalZ=1 AngleXU=0 Radius=8.2 StartAngle=5.12409 EndAngle=5.98426
    g66: LineSegment StartX=14.667 StartY=136.181 StartZ=0 EndX=17.55 EndY=145.537 EndZ=0
    g67: ArcOfCircle CenterX=5.11046 CenterY=139.126 CenterZ=0 NormalX=0 NormalY=0 NormalZ=1 AngleXU=0 Radius=10 StartAngle=5.12409 EndAngle=5.98426
    g68: ArcOfCircle CenterX=12.7717 CenterY=147.009 CenterZ=0 NormalX=0 NormalY=0 NormalZ=1 AngleXU=0 Radius=5 StartAngle=5.98426 EndAngle=7.49532
    g69: ArcOfCircle CenterX=27.9007 CenterY=86.9341 CenterZ=0 NormalX=0 NormalY=0 NormalZ=1 AngleXU=0 Radius=46.9511 StartAngle=1.9825 EndAngle=3.61535
    g70: ArcOfCircle CenterX=-24.8748 CenterY=54.489 CenterZ=0 NormalX=0 NormalY=0 NormalZ=1 AngleXU=0 Radius=5 StartAngle=4.59821 EndAngle=5.64052
    g71: LineSegment StartX=-14.3261 StartY=60.2359 StartZ=0 EndX=-20.8723 EndY=51.4924 EndZ=0
    g72: ArcOfCircle CenterX=-18.3286 CenterY=63.2325 CenterZ=0 NormalX=0 NormalY=0 NormalZ=1 AngleXU=0 Radius=5 StartAngle=5.64052 EndAngle=6.75694
    g73: ArcOfCircle CenterX=27.9007 CenterY=86.9341 CenterZ=0 NormalX=0 NormalY=0 NormalZ=1 AngleXU=0 Radius=77.9511 StartAngle=2.04047 EndAngle=3.53847
    g74: LineSegment StartX=0.656673 StartY=156.891 StartZ=0 EndX=14.5268 EndY=151.691 EndZ=0
    g75: ArcOfCircle CenterX=-2.85354 CenterY=147.527 CenterZ=0 NormalX=0 NormalY=0 NormalZ=1 AngleXU=0 Radius=10 StartAngle=1.21213 EndAngle=2.04047
    g76: LineSegment StartX=-35.908 StartY=50.7333 StartZ=0 EndX=-25.4431 EndY=49.5332 EndZ=0
    g77: ArcOfCircle CenterX=-34.7687 CenterY=60.6682 CenterZ=0 NormalX=0 NormalY=0 NormalZ=1 AngleXU=0 Radius=10 StartAngle=3.53847 EndAngle=4.59821
    g78: LineSegment StartX=14.667 StartY=136.181 StartZ=0 EndX=17.55 EndY=145.537 EndZ=0
    g79: ArcOfCircle CenterX=5.11046 CenterY=139.126 CenterZ=0 NormalX=0 NormalY=0 NormalZ=1 AngleXU=0 Radius=10 StartAngle=5.12409 EndAngle=5.98426
    g80: ArcOfCircle CenterX=12.7717 CenterY=147.009 CenterZ=0 NormalX=0 NormalY=0 NormalZ=1 AngleXU=0 Radius=5 StartAngle=5.98426 EndAngle=8.10068
    g81: ArcOfCircle CenterX=27.9007 CenterY=86.9341 CenterZ=0 NormalX=0 NormalY=0 NormalZ=1 AngleXU=0 Radius=46.9511 StartAngle=1.9825 EndAngle=3.61535
    g82: ArcOfCircle CenterX=-24.8748 CenterY=54.489 CenterZ=0 NormalX=0 NormalY=0 NormalZ=1 AngleXU=0 Radius=5 StartAngle=3.69281 EndAngle=5.64052
    g83: LineSegment StartX=-14.3261 StartY=60.2359 StartZ=0 EndX=-20.8723 EndY=51.4924 EndZ=0
    g84: ArcOfCircle CenterX=-18.3286 CenterY=63.2325 CenterZ=0 NormalX=0 NormalY=0 NormalZ=1 AngleXU=0 Radius=5 StartAngle=5.64052 EndAngle=6.75694
FEATURE [Sketcher::SketchObject] Sketch038  label="new-main1"
  ArcFitTolerance = 1e-06
  ExternalGeometry = -> [Hole,Sketch004]
  FullyConstrained = false
  MakeInternals = false
  sketch-geometry (20):
    g0: ArcOfCircle CenterX=27.9007 CenterY=86.6766 CenterZ=0 NormalX=0 NormalY=0 NormalZ=1 AngleXU=0 Radius=46.8342 StartAngle=1.98229 EndAngle=3.61045
    g1: ArcOfCircle CenterX=-18.3286 CenterY=63.2325 CenterZ=0 NormalX=0 NormalY=0 NormalZ=1 AngleXU=0 Radius=5 StartAngle=5.83507 EndAngle=6.75694
    g2: ArcOfCircle CenterX=27.9007 CenterY=86.9341 CenterZ=0 NormalX=0 NormalY=0 NormalZ=1 AngleXU=0 Radius=77.9511 StartAngle=2.04047 EndAngle=2.81723
    g3: LineSegment StartX=0.656673 StartY=156.891 StartZ=0 EndX=19.7284 EndY=149.498 EndZ=0
    g4: ArcOfCircle CenterX=-2.85354 CenterY=147.527 CenterZ=0 NormalX=0 NormalY=0 NormalZ=1 AngleXU=0 Radius=10 StartAngle=1.21213 EndAngle=2.04047
    g5: ArcOfCircle CenterX=-92.7379 CenterY=-554.275 CenterZ=0 NormalX=0 NormalY=0 NormalZ=1 AngleXU=0 Radius=564.875 StartAngle=1.4751 EndAngle=1.51212
    g6: ArcOfCircle CenterX=-40.6765 CenterY=-11.8744 CenterZ=0 NormalX=0 NormalY=0 NormalZ=1 AngleXU=0 Radius=19.9818 StartAngle=1.11294 EndAngle=1.47501
    g7: ArcOfCircle CenterX=-122.339 CenterY=57.7727 CenterZ=0 NormalX=0 NormalY=0 NormalZ=1 AngleXU=0 Radius=169.106 StartAngle=0.499917 EndAngle=0.573308
    g8: ArcOfCircle CenterX=10.468 CenterY=34.4667 CenterZ=0 NormalX=0 NormalY=0 NormalZ=1 AngleXU=0 Radius=33.6298 StartAngle=2.9338 EndAngle=3.24442
    g9: LineSegment StartX=-13.8223 StartY=61.0662 StartZ=0 EndX=-19.2146 EndY=49.9524 EndZ=0
    g10: LineSegment StartX=-19.2146 StartY=49.9524 StartZ=0 EndX=-22.4383 EndY=41.4047 EndZ=0
    g11: LineSegment StartX=9.16812 StartY=129.601 StartZ=0 EndX=26.0717 EndY=138.834 EndZ=0
    g12: LineSegment StartX=-22.9841 StartY=31.0146 StartZ=0 EndX=-31.844 EndY=6.04929 EndZ=0
    g13: Circle CenterX=-68.4703 CenterY=62.8597 CenterZ=0 NormalX=0 NormalY=0 NormalZ=1 AngleXU=0 Radius=2.5
    g14: Circle CenterX=-68.4603 CenterY=34.8426 CenterZ=0 NormalX=0 NormalY=0 NormalZ=1 AngleXU=0 Radius=2.5
    g15: Circle CenterX=-24.8924 CenterY=54.4937 CenterZ=0 NormalX=0 NormalY=0 NormalZ=1 AngleXU=0 Radius=1.6
    g16: Circle CenterX=12.779 CenterY=147.001 CenterZ=0 NormalX=0 NormalY=0 NormalZ=1 AngleXU=0 Radius=1.6
    g17: LineSegment StartX=-45.9854 StartY=111.778 StartZ=0 EndX=-76.6293 EndY=63.0474 EndZ=0
    g18: LineSegment StartX=-76.6293 StartY=63.0474 StartZ=0 EndX=-76.6293 EndY=32.6027 EndZ=0
    g19: LineSegment StartX=-76.6293 StartY=32.6027 StartZ=0 EndX=-59.6127 EndY=9.62807 EndZ=0
  constraints (21):
    c: Coincident(g9,g1)
    c: Coincident(g10,g9)
    c: Coincident(g10,g8)
    c: Coincident(g5,g6)
    c: Coincident(g11,g0)
    c: Coincident(g7,g3)
    c: Perpendicular(g7,g11) = 4.71239
    c: Coincident(g2,g4)
    c: Coincident(g3,g4)
    c: Coincident(g0,g1)
    c: Coincident(g12,g8)
    c: Coincident(g12,g6)
    c: Diameter(g13) = 5
    c: Diameter(g14) = 5
    c: Diameter(g15) = 3.2
    c: Diameter(g16) = 3.2
    c: Coincident(g17,g2)
    c: Coincident(g18,g17)
    c: Vertical(g18)
    c: Coincident(g19,g18)
    c: Coincident(g5,g19)
FEATURE [Sketcher::SketchObject] Sketch042  label="new-main1-copy"
  ArcFitTolerance = 1e-06
  ExternalGeometry = -> [Hole,Sketch004]
  FullyConstrained = false
  MakeInternals = false
  sketch-geometry (21):
    g0: ArcOfCircle CenterX=27.9007 CenterY=86.6766 CenterZ=0 NormalX=0 NormalY=0 NormalZ=1 AngleXU=0 Radius=46.8342 StartAngle=1.98229 EndAngle=3.61045
    g1: ArcOfCircle CenterX=-18.3286 CenterY=63.2325 CenterZ=0 NormalX=0 NormalY=0 NormalZ=1 AngleXU=0 Radius=5 StartAngle=5.83507 EndAngle=6.75694
    g2: ArcOfCircle CenterX=27.9007 CenterY=86.9341 CenterZ=0 NormalX=0 NormalY=0 NormalZ=1 AngleXU=0 Radius=77.9511 StartAngle=2.04047 EndAngle=2.81723
    g3: LineSegment StartX=0.656673 StartY=156.891 StartZ=0 EndX=19.7284 EndY=149.498 EndZ=0
    g4: ArcOfCircle CenterX=-2.85354 CenterY=147.527 CenterZ=0 NormalX=0 NormalY=0 NormalZ=1 AngleXU=0 Radius=10 StartAngle=1.21213 EndAngle=2.04047
    g5: ArcOfCircle CenterX=-81.389 CenterY=180.564 CenterZ=0 NormalX=0 NormalY=0 NormalZ=1 AngleXU=0 Radius=77.3628 StartAngle=4.75752 EndAngle=5.18772
    g6: ArcOfCircle CenterX=-92.7345 CenterY=-554.217 CenterZ=0 NormalX=0 NormalY=0 NormalZ=1 AngleXU=0 Radius=564.817 StartAngle=1.4751 EndAngle=1.57051
    g7: ArcOfCircle CenterX=31.9393 CenterY=135.651 CenterZ=0 NormalX=0 NormalY=0 NormalZ=1 AngleXU=0 Radius=144.447 StartAngle=4.25504 EndAngle=4.31779
    g8: ArcOfCircle CenterX=-12.0567 CenterY=30.0182 CenterZ=0 NormalX=0 NormalY=0 NormalZ=1 AngleXU=0 Radius=30.0182 StartAngle=4.31799 EndAngle=4.71239
    g9: ArcOfCircle CenterX=-40.6765 CenterY=-11.8744 CenterZ=0 NormalX=0 NormalY=0 NormalZ=1 AngleXU=0 Radius=19.9818 StartAngle=1.11294 EndAngle=1.47501
    g10: ArcOfCircle CenterX=-8.0079 CenterY=31.8587 CenterZ=0 NormalX=0 NormalY=0 NormalZ=1 AngleXU=0 Radius=15 StartAngle=3.19789 EndAngle=4.71239
    g11: LineSegment StartX=-77.8986 StartY=103.28 StartZ=0 EndX=-92.5712 EndY=103.308 EndZ=0
    g12: ArcOfCircle CenterX=-122.339 CenterY=57.7727 CenterZ=0 NormalX=0 NormalY=0 NormalZ=1 AngleXU=0 Radius=169.106 StartAngle=0.499917 EndAngle=0.573308
    g13: ArcOfCircle CenterX=10.468 CenterY=34.4667 CenterZ=0 NormalX=0 NormalY=0 NormalZ=1 AngleXU=0 Radius=33.6298 StartAngle=2.9338 EndAngle=3.24442
    g14: LineSegment StartX=-92.5712 StartY=103.308 StartZ=0 EndX=-92.5712 EndY=10.6001 EndZ=0
    g15: LineSegment StartX=-13.8223 StartY=61.0662 StartZ=0 EndX=-19.2146 EndY=49.9524 EndZ=0
    g16: LineSegment StartX=-19.2146 StartY=49.9524 StartZ=0 EndX=-22.4383 EndY=41.4047 EndZ=0
    g17: LineSegment StartX=9.16812 StartY=129.601 StartZ=0 EndX=26.0717 EndY=138.834 EndZ=0
    g18: LineSegment StartX=-5 StartY=17 StartZ=0 EndX=-8.0079 EndY=16.8587 EndZ=0
    g19: LineSegment StartX=-5 StartY=0 StartZ=0 EndX=-12.0567 EndY=0 EndZ=0
    g20: LineSegment StartX=-5 StartY=17 StartZ=0 EndX=-5 EndY=0 EndZ=0
  constraints (20):
    c: Vertical(g14)
    c: Coincident(g6,g14)
    c: PointOnObject(g11,g14)
    c: Coincident(g15,g1)
    c: Coincident(g16,g15)
    c: Coincident(g16,g13)
    c: Coincident(g6,g9)
    c: Coincident(g11,g5)
    c: Coincident(g5,g2)
    c: Coincident(g17,g0)
    c: Coincident(g12,g3)
    c: Perpendicular(g12,g17) = 4.71239
    c: Coincident(g7,g9)
    c: Coincident(g10,g13)
    c: Coincident(g2,g4)
    c: Coincident(g3,g4)
    c: Coincident(g18,g10)
    c: Tangent(g19,g8) = 1.5708
    c: Coincident(g7,g8)
    c: Coincident(g0,g1)
FEATURE [Sketcher::SketchObject] Sketch043  label="taper"
  ArcFitTolerance = 1e-06
  ExternalGeometry = -> [Hole,Sketch004]
  FullyConstrained = false
  MakeInternals = false
  Placement = pos=(0,0,-12.5) rot=(0,0,1;0rad)
  sketch-geometry (8):
    g0: ArcOfCircle CenterX=31.9393 CenterY=135.651 CenterZ=0 NormalX=0 NormalY=0 NormalZ=1 AngleXU=0 Radius=144.447 StartAngle=4.25504 EndAngle=4.31779
    g1: ArcOfCircle CenterX=-12.0567 CenterY=30.0182 CenterZ=0 NormalX=0 NormalY=0 NormalZ=1 AngleXU=0 Radius=30.0182 StartAngle=4.31799 EndAngle=4.71239
    g2: ArcOfCircle CenterX=-8.0079 CenterY=31.8587 CenterZ=0 NormalX=0 NormalY=0 NormalZ=1 AngleXU=0 Radius=15 StartAngle=3.19789 EndAngle=4.71239
    g3: LineSegment StartX=-5 StartY=17 StartZ=0 EndX=-8.0079 EndY=16.8587 EndZ=0
    g4: LineSegment StartX=-5 StartY=4.47522e-08 StartZ=0 EndX=-12.0567 EndY=0 EndZ=0
    g5: LineSegment StartX=-5.20231 StartY=16.9997 StartZ=0 EndX=-5.11654 EndY=-0.000203808 EndZ=0
    g6: LineSegment StartX=-22.9841 StartY=31.0146 StartZ=0 EndX=-31.844 EndY=6.04929 EndZ=0
    g7: LineSegment StartX=-21.4943 StartY=1.52218 StartZ=0 EndX=-14.6684 EndY=18.4185 EndZ=0
  constraints (8):
    c: Coincident(g3,g2)
    c: Tangent(g4,g1) = 1.5708
    c: Coincident(g0,g1)
    c: Coincident(g6,g2)
    c: Coincident(g6,g0)
    c: DistanceY(g1) = 0
    c: PointOnObject(g7,g2)
    c: PointOnObject(g7,g1)
FEATURE [Sketcher::SketchObject] Sketch044  label="end001"
  ArcFitTolerance = 1e-06
  AttachmentOffset = pos=(0,0,-5) rot=(0,0,1;0rad)
  AttachmentSupport = -> [DatumPlane002]
  FullyConstrained = false
  MakeInternals = false
  MapMode = 5
  Placement = pos=(-5,0,0) rot=(0.57735,0.57735,0.57735;2.0944rad)
  sketch-geometry (5):
    g0: Ellipse CenterX=8.5 CenterY=0 CenterZ=0 NormalX=0 NormalY=0 NormalZ=1 MajorRadius=18 MinorRadius=8.5 AngleXU=1.5708
    g1: LineSegment [constr] StartX=8.5 StartY=18 StartZ=0 EndX=8.5 EndY=-18 EndZ=0
    g2: LineSegment [constr] StartX=0 StartY=0 StartZ=0 EndX=17 EndY=0 EndZ=0
    g3: GeomPoint [constr] X=8.5 Y=15.8666 Z=0
    g4: GeomPoint [constr] X=8.5 Y=-15.8666 Z=0
  constraints (2):
    c: InternalAlignment(g1-g4 -> g0) x4
    c: PointOnObject(g-1,g0)
FEATURE [PartDesign::Plane] DatumPlane016
  Length = 273.909
  MapMode = 5
  Placement = pos=(-30.1887,10.7136,0) rot=(0.707551,0.499685,0.499685;1.91004rad)
  ResizeMode = 0
  Width = 72.4269
FEATURE [Sketcher::SketchObject] Sketch046  label="wirepocket"
  ArcFitTolerance = 1e-06
  AttachmentOffset = pos=(0,0,5) rot=(0,0,1;0rad)
  AttachmentSupport = -> [XY_Plane001]
  FullyConstrained = false
  MakeInternals = false
  MapMode = 5
  Placement = pos=(0,0,5) rot=(0,0,1;0rad)
  sketch-geometry (16):
    g0: LineSegment StartX=-12.2848 StartY=154.45 StartZ=0 EndX=-3.6e-15 EndY=135.833 EndZ=0
    g1: LineSegment StartX=-3.6e-15 StartY=135.833 StartZ=0 EndX=-8.34636 EndY=129.813 EndZ=0
    g2: LineSegment StartX=-8.34636 StartY=129.813 StartZ=0 EndX=-20.7548 EndY=148.733 EndZ=0
    g3: LineSegment StartX=-20.7548 StartY=148.733 StartZ=0 EndX=-12.2848 EndY=154.45 EndZ=0
    g4: LineSegment StartX=-36.9312 StartY=132.4 StartZ=0 EndX=-16.7829 EndY=119.746 EndZ=0
    g5: LineSegment StartX=-16.7829 StartY=119.746 StartZ=0 EndX=-22.8029 EndY=110.9 EndZ=0
    g6: LineSegment StartX=-22.8029 StartY=110.9 StartZ=0 EndX=-42.4597 EndY=123.186 EndZ=0
    g7: LineSegment StartX=-42.4597 StartY=123.186 StartZ=0 EndX=-36.9312 EndY=132.4 EndZ=0
    g8: LineSegment StartX=-50.691 StartY=102.301 StartZ=0 EndX=-26.4885 EndY=98.9835 EndZ=0
    g9: LineSegment StartX=-26.4885 StartY=98.9835 StartZ=0 EndX=-27.9628 EndY=88.1722 EndZ=0
    g10: LineSegment StartX=-27.9628 StartY=88.1722 StartZ=0 EndX=-52.0424 EndY=92.1036 EndZ=0
    g11: LineSegment StartX=-52.0424 StartY=92.1036 StartZ=0 EndX=-50.691 EndY=102.301 EndZ=0
    g12: LineSegment StartX=-49.8188 StartY=68.6873 StartZ=0 EndX=-27.5819 EndY=75.9358 EndZ=0
    g13: LineSegment StartX=-27.5819 StartY=75.9358 StartZ=0 EndX=-24.3877 EndY=65.4931 EndZ=0
    g14: LineSegment StartX=-24.3877 StartY=65.4931 StartZ=0 EndX=-47.3616 EndY=58.3675 EndZ=0
    g15: LineSegment StartX=-47.3616 StartY=58.3675 StartZ=0 EndX=-49.8188 EndY=68.6873 EndZ=0
  constraints (17):
    c: PointOnObject(g0,g-2)
    c: Coincident(g0,g1)
    c: Coincident(g1,g2)
    c: Coincident(g2,g3)
    c: Coincident(g3,g0)
    c: Coincident(g4,g5)
    c: Coincident(g5,g6)
    c: Coincident(g6,g7)
    c: Coincident(g7,g4)
    c: Coincident(g8,g9)
    c: Coincident(g9,g10)
    c: Coincident(g10,g11)
    c: Coincident(g11,g8)
    c: Coincident(g12,g13)
    c: Coincident(g13,g14)
    c: Coincident(g14,g15)
    c: Coincident(g15,g12)
FEATURE [Sketcher::SketchObject] Sketch047
  ArcFitTolerance = 1e-06
  AttachmentSupport = -> [DatumPlane016]
  ExternalGeometry = -> [Sketch043]
  FullyConstrained = true
  MakeInternals = false
  MapMode = 5
  Placement = pos=(-30.1887,10.7136,0) rot=(0.707551,0.499685,0.499685;1.91004rad)
  sketch-geometry (4):
    g0: LineSegment StartX=-4.94934 StartY=-12.5 StartZ=0 EndX=21.5415 EndY=-12.5 EndZ=0
    g1: LineSegment StartX=21.5415 StartY=-12.5 StartZ=0 EndX=21.5415 EndY=5 EndZ=0
    g2: LineSegment StartX=21.5415 StartY=5 StartZ=0 EndX=-4.94934 EndY=5 EndZ=0
    g3: LineSegment StartX=-4.94934 StartY=5 StartZ=0 EndX=-4.94934 EndY=-12.5 EndZ=0
  constraints (10):
    c: Coincident(g0,g1)
    c: Coincident(g1,g2)
    c: Coincident(g2,g3)
    c: Coincident(g3,g0)
    c: Horizontal(g0)
    c: Horizontal(g2)
    c: Vertical(g1)
    c: Vertical(g3)
    c: Coincident(g0,g-3)
    c: Coincident(g1,g-4)
FEATURE [Part::Feature] AdditiveLoft_cs
  shape: bbox 1e-05 x 21.75 x 26.75 mm, 0 faces, 0 solids (baked)
FEATURE [PartDesign::Plane] DatumPlane018
  AttachmentOffset = pos=(0,0,0) rot=(0,1,0;1.5708rad)
  AttachmentSupport = -> [Sketch043]
  Length = 280.965
  MapMode = 7
  Placement = pos=(-21.4943,1.52218,-12.5) rot=(0.723578,0.488076,0.488076;1.88884rad)
  ResizeMode = 0
  Width = 72.7262
FEATURE [Sketcher::SketchObject] Sketch052
  ArcFitTolerance = 1e-06
  AttachmentOffset = pos=(0,12.5,0) rot=(0,0,1;1.5708rad)
  AttachmentSupport = -> [DatumPlane018]
  FullyConstrained = false
  MakeInternals = false
  MapMode = 5
  Placement = pos=(-21.4943,1.52218,0) rot=(0.700522,-0.136156,0.700522;2.87094rad)
  sketch-geometry (4):
    g0: ArcOfCircle CenterX=-0.683601 CenterY=-9.30284 CenterZ=0 NormalX=0 NormalY=0 NormalZ=1 AngleXU=0 Radius=10.8341 StartAngle=5.2843 EndAngle=7.28207
    g1: ArcOfCircle CenterX=-3.06709 CenterY=-9.30289 CenterZ=0 NormalX=0 NormalY=0 NormalZ=1 AngleXU=0 Radius=10.8341 StartAngle=2.14272 EndAngle=4.14047
    g2: ArcOfCircle CenterX=-1.87496 CenterY=-120.042 CenterZ=0 NormalX=0 NormalY=0 NormalZ=1 AngleXU=0 Radius=120.057 StartAngle=1.512 EndAngle=1.6296
    g3: ArcOfCircle CenterX=-1.8758 CenterY=82.8675 CenterZ=0 NormalX=0 NormalY=0 NormalZ=1 AngleXU=0 Radius=101.526 StartAngle=4.64284 EndAngle=4.78195
  constraints (6):
    c: Vertical(g1,g1)
    c: Coincident(g2,g1)
    c: Coincident(g2,g0)
    c: PointOnObject(g-1,g2)
    c: Coincident(g3,g1) = -1.5708
    c: Coincident(g3,g0)
FEATURE [Sketcher::SketchObject] Sketch053
  ArcFitTolerance = 1e-06
  AttachmentSupport = -> [DatumPlane018]
  FullyConstrained = true
  MakeInternals = false
  MapMode = 5
  Placement = pos=(-21.4943,1.52218,-12.5) rot=(0.723578,0.488076,0.488076;1.88884rad)
FEATURE [Sketcher::SketchObject] Sketch041  label="mainbodyfull"
  ArcFitTolerance = 1e-06
  ExternalGeometry = -> [Sketch038,Sketch037]
  FullyConstrained = false
  MakeInternals = false
  sketch-geometry (43):
    g0: LineSegment StartX=-77.8986 StartY=103.308 StartZ=0 EndX=-92.7345 EndY=103.308 EndZ=0
    g1: ArcOfCircle CenterX=27.9007 CenterY=86.9341 CenterZ=0 NormalX=0 NormalY=0 NormalZ=1 AngleXU=0 Radius=77.9511 StartAngle=2.04047 EndAngle=2.81723
    g2: ArcOfCircle CenterX=-2.85354 CenterY=147.527 CenterZ=0 NormalX=0 NormalY=0 NormalZ=1 AngleXU=0 Radius=10 StartAngle=1.21213 EndAngle=2.04047
    g3: LineSegment StartX=0.656673 StartY=156.891 StartZ=0 EndX=19.7284 EndY=149.498 EndZ=0
    g4: LineSegment StartX=26.0717 StartY=138.834 StartZ=0 EndX=9.16812 EndY=129.601 EndZ=0
    g5: ArcOfCircle CenterX=27.9007 CenterY=86.6766 CenterZ=0 NormalX=0 NormalY=0 NormalZ=1 AngleXU=0 Radius=46.8342 StartAngle=1.98229 EndAngle=3.61045
    g6: ArcOfCircle CenterX=-18.3286 CenterY=63.2325 CenterZ=0 NormalX=0 NormalY=0 NormalZ=1 AngleXU=0 Radius=5 StartAngle=5.83507 EndAngle=6.75694
    g7: LineSegment StartX=-13.8223 StartY=61.0662 StartZ=0 EndX=-19.2146 EndY=49.9524 EndZ=0
    g8: LineSegment StartX=-19.2146 StartY=49.9524 StartZ=0 EndX=-22.4383 EndY=41.4047 EndZ=0
    g9: ArcOfCircle CenterX=10.468 CenterY=34.4667 CenterZ=0 NormalX=0 NormalY=0 NormalZ=1 AngleXU=0 Radius=33.6298 StartAngle=2.9338 EndAngle=3.24442
    g10: ArcOfCircle CenterX=-40.6765 CenterY=-11.8744 CenterZ=0 NormalX=0 NormalY=0 NormalZ=1 AngleXU=0 Radius=19.9818 StartAngle=1.11294 EndAngle=1.47501
    g11: ArcOfCircle CenterX=-92.7345 CenterY=-530.605 CenterZ=0 NormalX=0 NormalY=0 NormalZ=1 AngleXU=0 Radius=541.223 StartAngle=1.50956 EndAngle=1.5708
    g12: LineSegment StartX=-59.6127 StartY=9.60385 StartZ=0 EndX=-38.7656 EndY=8.01579 EndZ=0
    g13: ArcOfCircle CenterX=-81.3778 CenterY=180.778 CenterZ=0 NormalX=0 NormalY=0 NormalZ=1 AngleXU=0 Radius=77.548 StartAngle=4.75727 EndAngle=5.18633
    g14: LineSegment StartX=-107.57 StartY=103.308 StartZ=0 EndX=-92.7345 EndY=103.308 EndZ=0
    g15: ArcOfCircle CenterX=-213.37 CenterY=86.9341 CenterZ=0 NormalX=0 NormalY=0 NormalZ=1 AngleXU=0 Radius=77.9511 StartAngle=0.324367 EndAngle=1.10112
    g16: ArcOfCircle CenterX=-182.615 CenterY=147.527 CenterZ=0 NormalX=0 NormalY=0 NormalZ=1 AngleXU=0 Radius=10 StartAngle=1.10112 EndAngle=1.92946
    g17: LineSegment StartX=-186.126 StartY=156.891 StartZ=0 EndX=-205.197 EndY=149.498 EndZ=0
    g18: LineSegment StartX=-205.197 StartY=149.498 StartZ=0 EndX=-211.541 EndY=138.834 EndZ=0
    g19: LineSegment StartX=-211.541 StartY=138.834 StartZ=0 EndX=-194.637 EndY=129.601 EndZ=0
    g20: ArcOfCircle CenterX=-213.37 CenterY=86.6766 CenterZ=0 NormalX=0 NormalY=0 NormalZ=1 AngleXU=0 Radius=46.8342 StartAngle=5.81433 EndAngle=7.44249
    g21: ArcOfCircle CenterX=-167.14 CenterY=63.2325 CenterZ=0 NormalX=0 NormalY=0 NormalZ=1 AngleXU=0 Radius=5 StartAngle=2.66784 EndAngle=3.58971
    g22: LineSegment StartX=-171.647 StartY=61.0662 StartZ=0 EndX=-166.254 EndY=49.9524 EndZ=0
    g23: LineSegment StartX=-166.254 StartY=49.9524 StartZ=0 EndX=-163.031 EndY=41.4047 EndZ=0
    g24: ArcOfCircle CenterX=-195.937 CenterY=34.4667 CenterZ=0 NormalX=0 NormalY=0 NormalZ=1 AngleXU=0 Radius=33.6298 StartAngle=6.18035 EndAngle=6.49098
    g25: LineSegment StartX=-162.485 StartY=31.0146 StartZ=0 EndX=-153.625 EndY=6.04929 EndZ=0
    g26: ArcOfCircle CenterX=-144.792 CenterY=-11.8744 CenterZ=0 NormalX=0 NormalY=0 NormalZ=1 AngleXU=0 Radius=19.9818 StartAngle=1.66658 EndAngle=2.02865
    g27: ArcOfCircle CenterX=-92.7345 CenterY=-530.605 CenterZ=0 NormalX=0 NormalY=0 NormalZ=1 AngleXU=0 Radius=541.223 StartAngle=1.5708 EndAngle=1.63203
    g28: LineSegment StartX=-125.856 StartY=9.60386 StartZ=0 EndX=-146.703 EndY=8.01579 EndZ=0
    g29: ArcOfCircle CenterX=-104.091 CenterY=180.778 CenterZ=0 NormalX=0 NormalY=0 NormalZ=1 AngleXU=0 Radius=77.548 StartAngle=4.23845 EndAngle=4.66751
    g30: ArcOfCircle CenterX=-122.339 CenterY=57.7726 CenterZ=0 NormalX=0 NormalY=0 NormalZ=1 AngleXU=0 Radius=169.106 StartAngle=0.499917 EndAngle=0.573308
    g31: LineSegment StartX=-22.9841 StartY=31.0146 StartZ=0 EndX=-31.844 EndY=6.04929 EndZ=0
    g32: Circle CenterX=-24.8924 CenterY=54.4937 CenterZ=0 NormalX=0 NormalY=0 NormalZ=1 AngleXU=0 Radius=1.6
    g33: Circle CenterX=12.779 CenterY=147.001 CenterZ=0 NormalX=0 NormalY=0 NormalZ=1 AngleXU=0 Radius=1.6
    g34: Circle CenterX=-68.4703 CenterY=62.8597 CenterZ=0 NormalX=0 NormalY=0 NormalZ=1 AngleXU=0 Radius=2.5
    g35: Circle CenterX=-68.4603 CenterY=34.8426 CenterZ=0 NormalX=0 NormalY=0 NormalZ=1 AngleXU=0 Radius=2.5
    g36: Circle CenterX=-92.7345 CenterY=76.8363 CenterZ=0 NormalX=0 NormalY=0 NormalZ=1 AngleXU=0 Radius=2.5
    g37: Circle CenterX=-116.983 CenterY=62.8363 CenterZ=0 NormalX=0 NormalY=0 NormalZ=1 AngleXU=0 Radius=2.5
    g38: Circle CenterX=-116.983 CenterY=34.8363 CenterZ=0 NormalX=0 NormalY=0 NormalZ=1 AngleXU=0 Radius=2.5
    g39: Circle CenterX=-92.7345 CenterY=20.8363 CenterZ=0 NormalX=0 NormalY=0 NormalZ=1 AngleXU=0 Radius=2.5
    g40: Circle CenterX=-92.7345 CenterY=48.8363 CenterZ=0 NormalX=0 NormalY=0 NormalZ=1 AngleXU=0 Radius=14.3449
    g41: Circle CenterX=-198.248 CenterY=147.001 CenterZ=0 NormalX=0 NormalY=0 NormalZ=1 AngleXU=0 Radius=1.6
    g42: Circle CenterX=-160.577 CenterY=54.4937 CenterZ=0 NormalX=0 NormalY=0 NormalZ=1 AngleXU=0 Radius=1.6
  constraints (61):
    c: Tangent(g1,g-4) = -1.5708
    c: Coincident(g1,g-4)
    c: Coincident(g2,g1)
    c: Coincident(g2,g-5)
    c: Tangent(g2,g-3)
    c: Coincident(g3,g2)
    c: Coincident(g3,g-6)
    c: Coincident(g4,g-9)
    c: Coincident(g5,g4)
    c: Coincident(g5,g-10)
    c: Tangent(g5,g-9)
    c: Coincident(g6,g-10)
    c: Coincident(g6,g5)
    c: Coincident(g7,g6)
    c: Coincident(g7,g-15)
    c: Coincident(g8,g7)
    c: Coincident(g8,g-16)
    c: Coincident(g9,g-16)
    c: Coincident(g10,g-17)
    c: Coincident(g10,g-17)
    c: Coincident(g12,g10)
    c: Coincident(g13,g0)
    c: Coincident(g13,g1)
    c: Coincident(g16,g15)
    c: Coincident(g17,g16)
    c: Coincident(g19,g18)
    c: Coincident(g20,g19)
    c: Coincident(g21,g20)
    c: Coincident(g22,g21)
    c: Coincident(g23,g22)
    c: Coincident(g25,g24)
    c: Coincident(g28,g26)
    c: Coincident(g29,g14)
    c: Coincident(g29,g15)
    c: Coincident(g17,g18)
    c: Coincident(g23,g24)
    c: Coincident(g25,g26)
    c: Coincident(g0,g14)
    c: Coincident(g30,g3)
    c: Coincident(g30,g4)
    c: Tangent(g30,g-6)
    c: Coincident(g31,g9)
    c: Coincident(g31,g10)
    c: Coincident(g32,g-12)
    c: PointOnObject(g-11,g32)
    c: Coincident(g33,g-8)
    c: Equal(g33,g-8)
    c: Coincident(g34,g-18)
    c: Equal(g34,g-18)
    c: Coincident(g35,g-19)
    c: Equal(g35,g-19)
    c: Coincident(g36,g-20)
    c: Equal(g36,g-20)
    c: Coincident(g37,g-22)
    c: Equal(g37,g-22)
    c: Coincident(g38,g-23)
    c: Equal(g38,g-23)
    c: Coincident(g39,g-25)
    c: Equal(g39,g-25)
    c: Coincident(g40,g-21)
    c: Equal(g40,g-21)
FEATURE [PartDesign::Pad] Pad001
  Direction = (0,0,1)
  Length = 5
  Length2 = 12.5
  Profile = -> Sketch041
  ReferenceAxis = -> Sketch041 [N_Axis]
  Refine = true
  Suppressed = false
  Type = 4
FEATURE [PartDesign::Pocket] Pocket
  BaseFeature = -> Pad001
  Direction = (0,0,-1)
  Length = 3
  Length2 = 5
  Profile = -> Sketch046
  ReferenceAxis = -> Sketch046 [N_Axis]
  Refine = true
  Suppressed = false
  Type = 0
FEATURE [PartDesign::AdditivePipe] AdditivePipe003
  AuxilleryCurvelinear = true
  AuxillerySpine = -> Sketch043 [Edge4,Edge5,Edge6]
  AuxillerySpineTangent = false
  BaseFeature = -> Pocket
  Binormal = (0,0,0)
  Mode = 3
  Profile = -> Sketch047
  Refine = true
  Sections = -> [Sketch052,Sketch044]
  Spine = -> Sketch043 [Edge2,Edge1]
  SpineTangent = false
  Suppressed = false
  Transformation = 1
  Transition = 0
FEATURE [PartDesign::Body] Body001
  AllowCompound = false
  Group = -> [Pad001,Sketch035,Sketch038,Sketch043,Sketch044,DatumPlane016,Sketch046,Pocket,Sketch047,Sketch052,DatumPlane018,Sketch053,AdditivePipe003,Sketch041,Sketch037]
  Origin = -> Origin001
  Tip = -> AdditivePipe003
FEATURE [Sketcher::SketchObject] Sketch054  label="mainbodyfull001"
  ArcFitTolerance = 1e-06
  ExternalGeometry = -> [Sketch038,Sketch037]
  FullyConstrained = false
  MakeInternals = false
  sketch-geometry (56):
    g0: LineSegment StartX=-77.8986 StartY=103.308 StartZ=0 EndX=-92.7345 EndY=103.308 EndZ=0
    g1: ArcOfCircle CenterX=27.9007 CenterY=86.9341 CenterZ=0 NormalX=0 NormalY=0 NormalZ=1 AngleXU=0 Radius=77.9511 StartAngle=2.04047 EndAngle=2.81723
    g2: ArcOfCircle CenterX=-2.85354 CenterY=147.527 CenterZ=0 NormalX=0 NormalY=0 NormalZ=1 AngleXU=0 Radius=10 StartAngle=1.21213 EndAngle=2.04047
    g3: LineSegment StartX=0.656673 StartY=156.891 StartZ=0 EndX=19.7284 EndY=149.498 EndZ=0
    g4: LineSegment StartX=26.0717 StartY=138.834 StartZ=0 EndX=9.16812 EndY=129.601 EndZ=0
    g5: ArcOfCircle CenterX=27.9007 CenterY=86.6766 CenterZ=0 NormalX=0 NormalY=0 NormalZ=1 AngleXU=0 Radius=46.8342 StartAngle=1.98229 EndAngle=3.61045
    g6: ArcOfCircle CenterX=-18.3286 CenterY=63.2325 CenterZ=0 NormalX=0 NormalY=0 NormalZ=1 AngleXU=0 Radius=5 StartAngle=5.83507 EndAngle=6.75694
    g7: LineSegment StartX=-13.8223 StartY=61.0662 StartZ=0 EndX=-19.2146 EndY=49.9524 EndZ=0
    g8: LineSegment StartX=-19.2146 StartY=49.9524 StartZ=0 EndX=-22.4383 EndY=41.4047 EndZ=0
    g9: ArcOfCircle CenterX=10.468 CenterY=34.4667 CenterZ=0 NormalX=0 NormalY=0 NormalZ=1 AngleXU=0 Radius=33.6298 StartAngle=2.9338 EndAngle=3.24442
    g10: ArcOfCircle CenterX=-40.6765 CenterY=-11.8744 CenterZ=0 NormalX=0 NormalY=0 NormalZ=1 AngleXU=0 Radius=19.9818 StartAngle=1.11294 EndAngle=1.47501
    g11: ArcOfCircle CenterX=-92.7345 CenterY=-530.605 CenterZ=0 NormalX=0 NormalY=0 NormalZ=1 AngleXU=0 Radius=541.223 StartAngle=1.50956 EndAngle=1.5708
    g12: LineSegment StartX=-59.6127 StartY=9.60385 StartZ=0 EndX=-38.7656 EndY=8.01579 EndZ=0
    g13: ArcOfCircle CenterX=-81.3778 CenterY=180.778 CenterZ=0 NormalX=0 NormalY=0 NormalZ=1 AngleXU=0 Radius=77.548 StartAngle=4.75727 EndAngle=5.18633
    g14: LineSegment StartX=-107.57 StartY=103.308 StartZ=0 EndX=-92.7345 EndY=103.308 EndZ=0
    g15: ArcOfCircle CenterX=-213.37 CenterY=86.9341 CenterZ=0 NormalX=0 NormalY=0 NormalZ=1 AngleXU=0 Radius=77.9511 StartAngle=0.324367 EndAngle=1.10112
    g16: ArcOfCircle CenterX=-182.615 CenterY=147.527 CenterZ=0 NormalX=0 NormalY=0 NormalZ=1 AngleXU=0 Radius=10 StartAngle=1.10112 EndAngle=1.92946
    g17: LineSegment StartX=-186.126 StartY=156.891 StartZ=0 EndX=-205.197 EndY=149.498 EndZ=0
    g18: LineSegment StartX=-205.197 StartY=149.498 StartZ=0 EndX=-211.541 EndY=138.834 EndZ=0
    g19: LineSegment StartX=-211.541 StartY=138.834 StartZ=0 EndX=-194.637 EndY=129.601 EndZ=0
    g20: ArcOfCircle CenterX=-213.37 CenterY=86.6766 CenterZ=0 NormalX=0 NormalY=0 NormalZ=1 AngleXU=0 Radius=46.8342 StartAngle=5.81433 EndAngle=7.44249
    g21: ArcOfCircle CenterX=-167.14 CenterY=63.2325 CenterZ=0 NormalX=0 NormalY=0 NormalZ=1 AngleXU=0 Radius=5 StartAngle=2.66784 EndAngle=3.58971
    g22: LineSegment StartX=-171.647 StartY=61.0662 StartZ=0 EndX=-166.254 EndY=49.9524 EndZ=0
    g23: LineSegment StartX=-166.254 StartY=49.9524 StartZ=0 EndX=-163.031 EndY=41.4047 EndZ=0
    g24: ArcOfCircle CenterX=-195.937 CenterY=34.4667 CenterZ=0 NormalX=0 NormalY=0 NormalZ=1 AngleXU=0 Radius=33.6298 StartAngle=6.18035 EndAngle=6.49098
    g25: LineSegment StartX=-162.485 StartY=31.0146 StartZ=0 EndX=-153.625 EndY=6.04929 EndZ=0
    g26: ArcOfCircle CenterX=-144.792 CenterY=-11.8744 CenterZ=0 NormalX=0 NormalY=0 NormalZ=1 AngleXU=0 Radius=19.9818 StartAngle=1.66658 EndAngle=2.02865
    g27: ArcOfCircle CenterX=-92.7345 CenterY=-530.605 CenterZ=0 NormalX=0 NormalY=0 NormalZ=1 AngleXU=0 Radius=541.223 StartAngle=1.5708 EndAngle=1.63203
    g28: LineSegment StartX=-125.856 StartY=9.60386 StartZ=0 EndX=-146.703 EndY=8.01579 EndZ=0
    g29: ArcOfCircle CenterX=-104.091 CenterY=180.778 CenterZ=0 NormalX=0 NormalY=0 NormalZ=1 AngleXU=0 Radius=77.548 StartAngle=4.23845 EndAngle=4.66751
    g30: ArcOfCircle CenterX=-122.339 CenterY=57.7726 CenterZ=0 NormalX=0 NormalY=0 NormalZ=1 AngleXU=0 Radius=169.106 StartAngle=0.499917 EndAngle=0.573308
    g31: LineSegment StartX=-22.9841 StartY=31.0146 StartZ=0 EndX=-31.844 EndY=6.04929 EndZ=0
    g32: Circle CenterX=-24.8924 CenterY=54.4937 CenterZ=0 NormalX=0 NormalY=0 NormalZ=1 AngleXU=0 Radius=1.6
    g33: Circle CenterX=12.779 CenterY=147.001 CenterZ=0 NormalX=0 NormalY=0 NormalZ=1 AngleXU=0 Radius=1.6
    g34: Circle CenterX=-68.4703 CenterY=62.8597 CenterZ=0 NormalX=0 NormalY=0 NormalZ=1 AngleXU=0 Radius=2.5
    g35: Circle CenterX=-68.4603 CenterY=34.8426 CenterZ=0 NormalX=0 NormalY=0 NormalZ=1 AngleXU=0 Radius=2.5
    g36: Circle CenterX=-92.7345 CenterY=76.8363 CenterZ=0 NormalX=0 NormalY=0 NormalZ=1 AngleXU=0 Radius=2.5
    g37: Circle CenterX=-116.983 CenterY=62.8363 CenterZ=0 NormalX=0 NormalY=0 NormalZ=1 AngleXU=0 Radius=2.5
    g38: Circle CenterX=-116.983 CenterY=34.8363 CenterZ=0 NormalX=0 NormalY=0 NormalZ=1 AngleXU=0 Radius=2.5
    g39: Circle CenterX=-92.7345 CenterY=20.8363 CenterZ=0 NormalX=0 NormalY=0 NormalZ=1 AngleXU=0 Radius=2.5
    g40: Circle CenterX=-92.7345 CenterY=48.8363 CenterZ=0 NormalX=0 NormalY=0 NormalZ=1 AngleXU=0 Radius=14.3449
    g41: Circle CenterX=-198.248 CenterY=147.001 CenterZ=0 NormalX=0 NormalY=0 NormalZ=1 AngleXU=0 Radius=1.6
    g42: Circle CenterX=-160.577 CenterY=54.4937 CenterZ=0 NormalX=0 NormalY=0 NormalZ=1 AngleXU=0 Radius=1.6
    g43: ArcOfCircle CenterX=27.9007 CenterY=86.6766 CenterZ=0 NormalX=0 NormalY=0 NormalZ=1 AngleXU=0 Radius=48.8342 StartAngle=2.52501 EndAngle=3.61045
    g44: ArcOfCircle CenterX=27.9007 CenterY=86.6766 CenterZ=0 NormalX=0 NormalY=0 NormalZ=1 AngleXU=0 Radius=48.8342 StartAngle=1.98229 EndAngle=2.52501
    g45: ArcOfCircle CenterX=-18.3286 CenterY=63.2325 CenterZ=0 NormalX=0 NormalY=0 NormalZ=1 AngleXU=0 Radius=3 StartAngle=5.83507 EndAngle=6.14236
    g46: ArcOfCircle CenterX=-18.3286 CenterY=63.2325 CenterZ=0 NormalX=0 NormalY=0 NormalZ=1 AngleXU=0 Radius=3 StartAngle=6.14236 EndAngle=6.75694
    g47: ArcOfCircle CenterX=10.468 CenterY=34.4667 CenterZ=0 NormalX=0 NormalY=0 NormalZ=1 AngleXU=0 Radius=35.6298 StartAngle=2.9338 EndAngle=3.24442
    g48: ArcOfCircle CenterX=-22.4383 CenterY=41.4047 CenterZ=0 NormalX=0 NormalY=0 NormalZ=-1 AngleXU=-1.363 Radius=2 StartAngle=1.5708 EndAngle=1.72365
    g49: LineSegment StartX=-21.086 StartY=50.6582 StartZ=0 EndX=-24.3097 EndY=42.1104 EndZ=0
    g50: ArcOfCircle CenterX=-19.2146 CenterY=49.9524 CenterZ=0 NormalX=0 NormalY=0 NormalZ=-1 AngleXU=-1.21015 Radius=2 StartAngle=1.5708 EndAngle=1.66188
    g51: LineSegment StartX=-15.6217 StartY=61.9392 StartZ=0 EndX=-21.014 EndY=50.8255 EndZ=0
    g52: ArcOfCircle CenterX=0.656673 CenterY=156.891 CenterZ=0 NormalX=0 NormalY=0 NormalZ=-1 AngleXU=0.358662 Radius=2 StartAngle=1.5708 EndAngle=1.58194
    g53: LineSegment StartX=-0.0552248 StartY=155.022 StartZ=0 EndX=19.0055 EndY=147.633 EndZ=0
    g54: ArcOfCircle CenterX=-2.85354 CenterY=147.527 CenterZ=0 NormalX=0 NormalY=0 NormalZ=1 AngleXU=0 Radius=8 StartAngle=1.21345 EndAngle=2.04047
    g55: ArcOfCircle CenterX=27.9007 CenterY=86.9341 CenterZ=0 NormalX=0 NormalY=0 NormalZ=1 AngleXU=0 Radius=75.9511 StartAngle=2.04047 EndAngle=2.81723
  constraints (69):
    c: Tangent(g1,g-4) = -1.5708
    c: Coincident(g1,g-4)
    c: Coincident(g2,g1)
    c: Coincident(g2,g-5)
    c: Tangent(g2,g-3)
    c: Coincident(g3,g2)
    c: Coincident(g3,g-6)
    c: Coincident(g4,g-9)
    c: Coincident(g5,g4)
    c: Coincident(g5,g-10)
    c: Tangent(g5,g-9)
    c: Coincident(g6,g-10)
    c: Coincident(g6,g5)
    c: Coincident(g7,g6)
    c: Coincident(g7,g-15)
    c: Coincident(g8,g7)
    c: Coincident(g8,g-16)
    c: Coincident(g9,g-16)
    c: Coincident(g10,g-17)
    c: Coincident(g10,g-17)
    c: Coincident(g12,g10)
    c: Coincident(g13,g0)
    c: Coincident(g13,g1)
    c: Coincident(g16,g15)
    c: Coincident(g17,g16)
    c: Coincident(g19,g18)
    c: Coincident(g20,g19)
    c: Coincident(g21,g20)
    c: Coincident(g22,g21)
    c: Coincident(g23,g22)
    c: Coincident(g25,g24)
    c: Coincident(g28,g26)
    c: Coincident(g29,g14)
    c: Coincident(g29,g15)
    c: Coincident(g17,g18)
    c: Coincident(g23,g24)
    c: Coincident(g25,g26)
    c: Coincident(g0,g14)
    c: Coincident(g30,g3)
    c: Coincident(g30,g4)
    c: Tangent(g30,g-6)
    c: Coincident(g31,g9)
    c: Coincident(g31,g10)
    c: Coincident(g32,g-12)
    c: PointOnObject(g-11,g32)
    c: Coincident(g33,g-8)
    c: Equal(g33,g-8)
    c: Coincident(g34,g-18)
    c: Equal(g34,g-18)
    c: Coincident(g35,g-19)
    c: Equal(g35,g-19)
    c: Coincident(g36,g-20)
    c: Equal(g36,g-20)
    c: Coincident(g37,g-22)
    c: Equal(g37,g-22)
    c: Coincident(g38,g-23)
    c: Equal(g38,g-23)
    c: Coincident(g39,g-25)
    c: Equal(g39,g-25)
    c: Coincident(g40,g-21)
    c: Equal(g40,g-21)
    c: Tangent(g43,g44) = -1.5708
    c: Tangent(g45,g46) = -1.5708
    c: Tangent(g47,g48) = -1.5708
    c: Tangent(g48,g49) = -1.5708
    c: Tangent(g49,g50) = -1.5708
    c: Tangent(g50,g51) = -1.5708
    c: Coincident(g53,g54)
    c: Tangent(g54,g55) = -1.5708
FEATURE [Sketcher::SketchObject] Sketch055  label="new-mainoledonly001"
  ArcFitTolerance = 1e-06
  FullyConstrained = false
  MakeInternals = false
  sketch-geometry (32):
    g0: Circle CenterX=12.7717 CenterY=147.009 CenterZ=0 NormalX=0 NormalY=0 NormalZ=-1 AngleXU=0 Radius=1.6
    g1: Circle CenterX=-24.8748 CenterY=54.489 CenterZ=0 NormalX=0 NormalY=0 NormalZ=-1 AngleXU=0 Radius=1.6
    g2: LineSegment StartX=-35.7029 StartY=52.5216 StartZ=0 EndX=-25.238 EndY=51.3215 EndZ=0
    g3: ArcOfCircle CenterX=-24.8748 CenterY=54.489 CenterZ=0 NormalX=0 NormalY=0 NormalZ=1 AngleXU=0 Radius=3.2 StartAngle=4.59821 EndAngle=5.64052
    g4: ArcOfCircle CenterX=-34.7687 CenterY=60.6682 CenterZ=0 NormalX=0 NormalY=0 NormalZ=1 AngleXU=0 Radius=8.2 StartAngle=3.53847 EndAngle=4.59821
    g5: LineSegment StartX=-15.767 StartY=61.3147 StartZ=0 EndX=-22.3132 EndY=52.5712 EndZ=0
    g6: ArcOfCircle CenterX=-18.3286 CenterY=63.2325 CenterZ=0 NormalX=0 NormalY=0 NormalZ=1 AngleXU=0 Radius=3.2 StartAngle=5.64052 EndAngle=6.75694
    g7: ArcOfCircle CenterX=27.9007 CenterY=86.9341 CenterZ=0 NormalX=0 NormalY=0 NormalZ=1 AngleXU=0 Radius=48.7511 StartAngle=1.9825 EndAngle=3.61535
    g8: ArcOfCircle CenterX=27.9007 CenterY=86.9341 CenterZ=0 NormalX=0 NormalY=0 NormalZ=1 AngleXU=0 Radius=76.1511 StartAngle=2.04047 EndAngle=3.53847
    g9: ArcOfCircle CenterX=-2.85354 CenterY=147.527 CenterZ=0 NormalX=0 NormalY=0 NormalZ=1 AngleXU=0 Radius=8.2 StartAngle=1.21213 EndAngle=2.04047
    g10: LineSegment StartX=0.0248341 StartY=155.205 StartZ=0 EndX=13.895 EndY=150.006 EndZ=0
    g11: ArcOfCircle CenterX=12.7717 CenterY=147.009 CenterZ=0 NormalX=0 NormalY=0 NormalZ=1 AngleXU=0 Radius=3.2 StartAngle=5.98426 EndAngle=7.49532
    g12: LineSegment StartX=12.9468 StartY=136.711 StartZ=0 EndX=15.8298 EndY=146.067 EndZ=0
    g13: ArcOfCircle CenterX=5.11046 CenterY=139.126 CenterZ=0 NormalX=0 NormalY=0 NormalZ=1 AngleXU=0 Radius=8.2 StartAngle=5.12409 EndAngle=5.98426
    g14: LineSegment StartX=14.667 StartY=136.181 StartZ=0 EndX=17.55 EndY=145.537 EndZ=0
    g15: ArcOfCircle CenterX=5.11046 CenterY=139.126 CenterZ=0 NormalX=0 NormalY=0 NormalZ=1 AngleXU=0 Radius=10 StartAngle=5.12409 EndAngle=5.98426
    g16: ArcOfCircle CenterX=12.7717 CenterY=147.009 CenterZ=0 NormalX=0 NormalY=0 NormalZ=1 AngleXU=0 Radius=5 StartAngle=5.98426 EndAngle=7.49532
    g17: ArcOfCircle CenterX=27.9007 CenterY=86.9341 CenterZ=0 NormalX=0 NormalY=0 NormalZ=1 AngleXU=0 Radius=46.9511 StartAngle=1.9825 EndAngle=3.61535
    g18: ArcOfCircle CenterX=-24.8748 CenterY=54.489 CenterZ=0 NormalX=0 NormalY=0 NormalZ=1 AngleXU=0 Radius=5 StartAngle=4.59821 EndAngle=5.64052
    g19: LineSegment StartX=-14.3261 StartY=60.2359 StartZ=0 EndX=-20.8723 EndY=51.4924 EndZ=0
    g20: ArcOfCircle CenterX=-18.3286 CenterY=63.2325 CenterZ=0 NormalX=0 NormalY=0 NormalZ=1 AngleXU=0 Radius=5 StartAngle=5.64052 EndAngle=6.75694
    g21: ArcOfCircle CenterX=27.9007 CenterY=86.9341 CenterZ=0 NormalX=0 NormalY=0 NormalZ=1 AngleXU=0 Radius=77.9511 StartAngle=2.04047 EndAngle=3.53847
    g22: LineSegment StartX=0.656673 StartY=156.891 StartZ=0 EndX=14.5268 EndY=151.691 EndZ=0
    g23: ArcOfCircle CenterX=-2.85354 CenterY=147.527 CenterZ=0 NormalX=0 NormalY=0 NormalZ=1 AngleXU=0 Radius=10 StartAngle=1.21213 EndAngle=2.04047
    g24: LineSegment StartX=-35.908 StartY=50.7333 StartZ=0 EndX=-25.4431 EndY=49.5332 EndZ=0
    g25: ArcOfCircle CenterX=-34.7687 CenterY=60.6682 CenterZ=0 NormalX=0 NormalY=0 NormalZ=1 AngleXU=0 Radius=10 StartAngle=3.53847 EndAngle=4.59821
    g26: LineSegment StartX=14.667 StartY=136.181 StartZ=0 EndX=17.55 EndY=145.537 EndZ=0
    g27: ArcOfCircle CenterX=5.11046 CenterY=139.126 CenterZ=0 NormalX=0 NormalY=0 NormalZ=1 AngleXU=0 Radius=10 StartAngle=5.12409 EndAngle=5.98426
    g28: ArcOfCircle CenterX=27.9007 CenterY=86.9341 CenterZ=0 NormalX=0 NormalY=0 NormalZ=1 AngleXU=0 Radius=46.9511 StartAngle=1.9825 EndAngle=3.61535
    g29: LineSegment StartX=-14.3261 StartY=60.2359 StartZ=0 EndX=-20.8723 EndY=51.4924 EndZ=0
    g30: ArcOfCircle CenterX=-18.3286 CenterY=63.2325 CenterZ=0 NormalX=0 NormalY=0 NormalZ=1 AngleXU=0 Radius=5 StartAngle=5.64052 EndAngle=6.75694
    g31: LineSegment StartX=12.7717 StartY=147.009 StartZ=0 EndX=-24.8748 EndY=54.489 EndZ=0
  constraints (11):
    c: Coincident(g22,g23)
    c: Coincident(g9,g10)
    c: Coincident(g21,g23)
    c: Coincident(g8,g9)
    c: Coincident(g16,g22)
    c: Coincident(g10,g11)
    c: Coincident(g11,g12)
    c: Coincident(g14,g16)
    c: Coincident(g14,g26)
    c: Coincident(g31,g0)
    c: Coincident(g31,g1)
